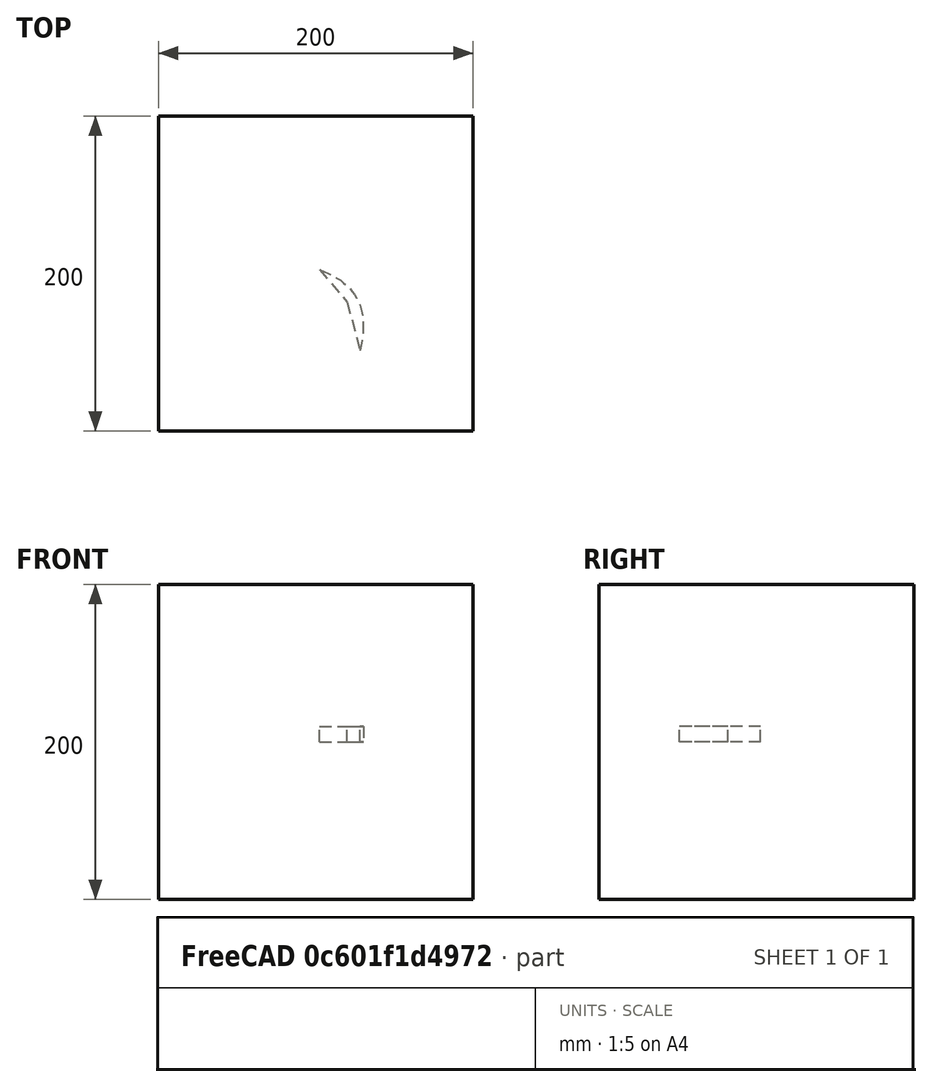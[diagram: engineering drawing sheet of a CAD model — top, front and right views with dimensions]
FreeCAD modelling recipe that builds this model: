
FCSTD DOCUMENT  (FreeCAD 1.0R39109 (Git))
Label: extrudedParabola-2
License: All rights reserved
LicenseURL: http://en.wikipedia.org/wiki/All_rights_reserved
objects: App::DocumentObjectGroupPython×1248, App::Part×2, Part::FeaturePython×1, Sketcher::SketchObject×1, Part::Extrusion×1
note: 4 computed .brp shape members not serialized (recipe doc carries the construction recipe); baked Part::Feature solids carry a one-line shape summary decoded from their .brp

FEATURE [App::DocumentObjectGroupPython] HALFPI  # scripted group (container) (typed FeaturePython)
  name = HALFPI
  value = pi/2.
FEATURE [App::DocumentObjectGroupPython] PI  # scripted group (container) (typed FeaturePython)
  name = PI
  value = 1.*pi
FEATURE [App::DocumentObjectGroupPython] TWOPI  # scripted group (container) (typed FeaturePython)
  name = TWOPI
  value = 2.*pi
FEATURE [App::DocumentObjectGroupPython] Constants  # scripted group (container) (typed FeaturePython)
  Group = -> [HALFPI,PI,TWOPI]
FEATURE [App::DocumentObjectGroupPython] Variables  # scripted group (container) (typed FeaturePython)
FEATURE [App::DocumentObjectGroupPython] Quantities  # scripted group (container) (typed FeaturePython)
FEATURE [App::DocumentObjectGroupPython] Isotopes  # scripted group (container) (typed FeaturePython)
FEATURE [App::DocumentObjectGroupPython] Elements  # scripted group (container) (typed FeaturePython)
FEATURE [App::DocumentObjectGroupPython] G4Isotopes  # scripted group (container) (typed FeaturePython)
FEATURE [App::DocumentObjectGroupPython] H_element  # scripted group (container) (typed FeaturePython)
  Z = 1
  atom_value = 1.008
  formula = H
  name = H_element
FEATURE [App::DocumentObjectGroupPython] He_element  # scripted group (container) (typed FeaturePython)
  Z = 2
  atom_value = 4.0026
  formula = He
  name = He_element
FEATURE [App::DocumentObjectGroupPython] Li_element  # scripted group (container) (typed FeaturePython)
  Z = 3
  atom_value = 6.94
  formula = Li
  name = Li_element
FEATURE [App::DocumentObjectGroupPython] Be_element  # scripted group (container) (typed FeaturePython)
  Z = 4
  atom_value = 9.01218
  formula = Be
  name = Be_element
FEATURE [App::DocumentObjectGroupPython] B_element  # scripted group (container) (typed FeaturePython)
  Z = 5
  atom_value = 10.81
  formula = B
  name = B_element
FEATURE [App::DocumentObjectGroupPython] C_element  # scripted group (container) (typed FeaturePython)
  Z = 6
  atom_value = 12.011
  formula = C
  name = C_element
FEATURE [App::DocumentObjectGroupPython] N_element  # scripted group (container) (typed FeaturePython)
  Z = 7
  atom_value = 14.007
  formula = N
  name = N_element
FEATURE [App::DocumentObjectGroupPython] O_element  # scripted group (container) (typed FeaturePython)
  Z = 8
  atom_value = 15.999
  formula = O
  name = O_element
FEATURE [App::DocumentObjectGroupPython] F_element  # scripted group (container) (typed FeaturePython)
  Z = 9
  atom_value = 18.9984
  formula = F
  name = F_element
FEATURE [App::DocumentObjectGroupPython] Ne_element  # scripted group (container) (typed FeaturePython)
  Z = 10
  atom_value = 20.1797
  formula = Ne
  name = Ne_element
FEATURE [App::DocumentObjectGroupPython] Na_element  # scripted group (container) (typed FeaturePython)
  Z = 11
  atom_value = 22.9898
  formula = Na
  name = Na_element
FEATURE [App::DocumentObjectGroupPython] Mg_element  # scripted group (container) (typed FeaturePython)
  Z = 12
  atom_value = 24.305
  formula = Mg
  name = Mg_element
FEATURE [App::DocumentObjectGroupPython] Al_element  # scripted group (container) (typed FeaturePython)
  Z = 13
  atom_value = 26.9815
  formula = Al
  name = Al_element
FEATURE [App::DocumentObjectGroupPython] Si_element  # scripted group (container) (typed FeaturePython)
  Z = 14
  atom_value = 28.085
  formula = Si
  name = Si_element
FEATURE [App::DocumentObjectGroupPython] P_element  # scripted group (container) (typed FeaturePython)
  Z = 15
  atom_value = 30.9738
  formula = P
  name = P_element
FEATURE [App::DocumentObjectGroupPython] S_element  # scripted group (container) (typed FeaturePython)
  Z = 16
  atom_value = 32.06
  formula = S
  name = S_element
FEATURE [App::DocumentObjectGroupPython] Cl_element  # scripted group (container) (typed FeaturePython)
  Z = 17
  atom_value = 35.45
  formula = Cl
  name = Cl_element
FEATURE [App::DocumentObjectGroupPython] Ar_element  # scripted group (container) (typed FeaturePython)
  Z = 18
  atom_value = 39.95
  formula = Ar
  name = Ar_element
FEATURE [App::DocumentObjectGroupPython] K_element  # scripted group (container) (typed FeaturePython)
  Z = 19
  atom_value = 39.0983
  formula = K
  name = K_element
FEATURE [App::DocumentObjectGroupPython] Ca_element  # scripted group (container) (typed FeaturePython)
  Z = 20
  atom_value = 40.078
  formula = Ca
  name = Ca_element
FEATURE [App::DocumentObjectGroupPython] Sc_element  # scripted group (container) (typed FeaturePython)
  Z = 21
  atom_value = 44.9559
  formula = Sc
  name = Sc_element
FEATURE [App::DocumentObjectGroupPython] Ti_element  # scripted group (container) (typed FeaturePython)
  Z = 22
  atom_value = 47.867
  formula = Ti
  name = Ti_element
FEATURE [App::DocumentObjectGroupPython] V_element  # scripted group (container) (typed FeaturePython)
  Z = 23
  atom_value = 50.9415
  formula = V
  name = V_element
FEATURE [App::DocumentObjectGroupPython] Cr_element  # scripted group (container) (typed FeaturePython)
  Z = 24
  atom_value = 51.9961
  formula = Cr
  name = Cr_element
FEATURE [App::DocumentObjectGroupPython] Mn_element  # scripted group (container) (typed FeaturePython)
  Z = 25
  atom_value = 54.938
  formula = Mn
  name = Mn_element
FEATURE [App::DocumentObjectGroupPython] Fe_element  # scripted group (container) (typed FeaturePython)
  Z = 26
  atom_value = 55.845
  formula = Fe
  name = Fe_element
FEATURE [App::DocumentObjectGroupPython] Co_element  # scripted group (container) (typed FeaturePython)
  Z = 27
  atom_value = 58.9332
  formula = Co
  name = Co_element
FEATURE [App::DocumentObjectGroupPython] Ni_element  # scripted group (container) (typed FeaturePython)
  Z = 28
  atom_value = 58.6934
  formula = Ni
  name = Ni_element
FEATURE [App::DocumentObjectGroupPython] Cu_element  # scripted group (container) (typed FeaturePython)
  Z = 29
  atom_value = 63.546
  formula = Cu
  name = Cu_element
FEATURE [App::DocumentObjectGroupPython] Zn_element  # scripted group (container) (typed FeaturePython)
  Z = 30
  atom_value = 65.38
  formula = Zn
  name = Zn_element
FEATURE [App::DocumentObjectGroupPython] Ga_element  # scripted group (container) (typed FeaturePython)
  Z = 31
  atom_value = 69.723
  formula = Ga
  name = Ga_element
FEATURE [App::DocumentObjectGroupPython] Ge_element  # scripted group (container) (typed FeaturePython)
  Z = 32
  atom_value = 72.63
  formula = Ge
  name = Ge_element
FEATURE [App::DocumentObjectGroupPython] As_element  # scripted group (container) (typed FeaturePython)
  Z = 33
  atom_value = 74.9216
  formula = As
  name = As_element
FEATURE [App::DocumentObjectGroupPython] Se_element  # scripted group (container) (typed FeaturePython)
  Z = 34
  atom_value = 78.971
  formula = Se
  name = Se_element
FEATURE [App::DocumentObjectGroupPython] Br_element  # scripted group (container) (typed FeaturePython)
  Z = 35
  atom_value = 79.904
  formula = Br
  name = Br_element
FEATURE [App::DocumentObjectGroupPython] Kr_element  # scripted group (container) (typed FeaturePython)
  Z = 36
  atom_value = 83.798
  formula = Kr
  name = Kr_element
FEATURE [App::DocumentObjectGroupPython] Rb_element  # scripted group (container) (typed FeaturePython)
  Z = 37
  atom_value = 85.4678
  formula = Rb
  name = Rb_element
FEATURE [App::DocumentObjectGroupPython] Sr_element  # scripted group (container) (typed FeaturePython)
  Z = 38
  atom_value = 87.62
  formula = Sr
  name = Sr_element
FEATURE [App::DocumentObjectGroupPython] Y_element  # scripted group (container) (typed FeaturePython)
  Z = 39
  atom_value = 88.9058
  formula = Y
  name = Y_element
FEATURE [App::DocumentObjectGroupPython] Zr_element  # scripted group (container) (typed FeaturePython)
  Z = 40
  atom_value = 91.224
  formula = Zr
  name = Zr_element
FEATURE [App::DocumentObjectGroupPython] Nb_element  # scripted group (container) (typed FeaturePython)
  Z = 41
  atom_value = 92.9064
  formula = Nb
  name = Nb_element
FEATURE [App::DocumentObjectGroupPython] Mo_element  # scripted group (container) (typed FeaturePython)
  Z = 42
  atom_value = 95.95
  formula = Mo
  name = Mo_element
FEATURE [App::DocumentObjectGroupPython] Tc_element  # scripted group (container) (typed FeaturePython)
  Z = 43
  atom_value = 97
  formula = Tc
  name = Tc_element
FEATURE [App::DocumentObjectGroupPython] Ru_element  # scripted group (container) (typed FeaturePython)
  Z = 44
  atom_value = 101.07
  formula = Ru
  name = Ru_element
FEATURE [App::DocumentObjectGroupPython] Rh_element  # scripted group (container) (typed FeaturePython)
  Z = 45
  atom_value = 102.905
  formula = Rh
  name = Rh_element
FEATURE [App::DocumentObjectGroupPython] Pd_element  # scripted group (container) (typed FeaturePython)
  Z = 46
  atom_value = 106.42
  formula = Pd
  name = Pd_element
FEATURE [App::DocumentObjectGroupPython] Ag_element  # scripted group (container) (typed FeaturePython)
  Z = 47
  atom_value = 107.868
  formula = Ag
  name = Ag_element
FEATURE [App::DocumentObjectGroupPython] Cd_element  # scripted group (container) (typed FeaturePython)
  Z = 48
  atom_value = 112.414
  formula = Cd
  name = Cd_element
FEATURE [App::DocumentObjectGroupPython] In_element  # scripted group (container) (typed FeaturePython)
  Z = 49
  atom_value = 114.818
  formula = In
  name = In_element
FEATURE [App::DocumentObjectGroupPython] Sn_element  # scripted group (container) (typed FeaturePython)
  Z = 50
  atom_value = 118.71
  formula = Sn
  name = Sn_element
FEATURE [App::DocumentObjectGroupPython] Sb_element  # scripted group (container) (typed FeaturePython)
  Z = 51
  atom_value = 121.76
  formula = Sb
  name = Sb_element
FEATURE [App::DocumentObjectGroupPython] Te_element  # scripted group (container) (typed FeaturePython)
  Z = 52
  atom_value = 127.6
  formula = Te
  name = Te_element
FEATURE [App::DocumentObjectGroupPython] I_element  # scripted group (container) (typed FeaturePython)
  Z = 53
  atom_value = 126.904
  formula = I
  name = I_element
FEATURE [App::DocumentObjectGroupPython] Xe_element  # scripted group (container) (typed FeaturePython)
  Z = 54
  atom_value = 131.293
  formula = Xe
  name = Xe_element
FEATURE [App::DocumentObjectGroupPython] Cs_element  # scripted group (container) (typed FeaturePython)
  Z = 55
  atom_value = 132.905
  formula = Cs
  name = Cs_element
FEATURE [App::DocumentObjectGroupPython] Ba_element  # scripted group (container) (typed FeaturePython)
  Z = 56
  atom_value = 137.327
  formula = Ba
  name = Ba_element
FEATURE [App::DocumentObjectGroupPython] La_element  # scripted group (container) (typed FeaturePython)
  Z = 57
  atom_value = 138.905
  formula = La
  name = La_element
FEATURE [App::DocumentObjectGroupPython] Ce_element  # scripted group (container) (typed FeaturePython)
  Z = 58
  atom_value = 140.116
  formula = Ce
  name = Ce_element
FEATURE [App::DocumentObjectGroupPython] Pr_element  # scripted group (container) (typed FeaturePython)
  Z = 59
  atom_value = 140.908
  formula = Pr
  name = Pr_element
FEATURE [App::DocumentObjectGroupPython] Nd_element  # scripted group (container) (typed FeaturePython)
  Z = 60
  atom_value = 144.242
  formula = Nd
  name = Nd_element
FEATURE [App::DocumentObjectGroupPython] Pm_element  # scripted group (container) (typed FeaturePython)
  Z = 61
  atom_value = 145
  formula = Pm
  name = Pm_element
FEATURE [App::DocumentObjectGroupPython] Sm_element  # scripted group (container) (typed FeaturePython)
  Z = 62
  atom_value = 150.36
  formula = Sm
  name = Sm_element
FEATURE [App::DocumentObjectGroupPython] Eu_element  # scripted group (container) (typed FeaturePython)
  Z = 63
  atom_value = 151.964
  formula = Eu
  name = Eu_element
FEATURE [App::DocumentObjectGroupPython] Gd_element  # scripted group (container) (typed FeaturePython)
  Z = 64
  atom_value = 157.25
  formula = Gd
  name = Gd_element
FEATURE [App::DocumentObjectGroupPython] Tb_element  # scripted group (container) (typed FeaturePython)
  Z = 65
  atom_value = 158.925
  formula = Tb
  name = Tb_element
FEATURE [App::DocumentObjectGroupPython] Dy_element  # scripted group (container) (typed FeaturePython)
  Z = 66
  atom_value = 162.5
  formula = Dy
  name = Dy_element
FEATURE [App::DocumentObjectGroupPython] Ho_element  # scripted group (container) (typed FeaturePython)
  Z = 67
  atom_value = 164.93
  formula = Ho
  name = Ho_element
FEATURE [App::DocumentObjectGroupPython] Er_element  # scripted group (container) (typed FeaturePython)
  Z = 68
  atom_value = 167.259
  formula = Er
  name = Er_element
FEATURE [App::DocumentObjectGroupPython] Tm_element  # scripted group (container) (typed FeaturePython)
  Z = 69
  atom_value = 168.934
  formula = Tm
  name = Tm_element
FEATURE [App::DocumentObjectGroupPython] Yb_element  # scripted group (container) (typed FeaturePython)
  Z = 70
  atom_value = 173.045
  formula = Yb
  name = Yb_element
FEATURE [App::DocumentObjectGroupPython] Lu_element  # scripted group (container) (typed FeaturePython)
  Z = 71
  atom_value = 174.967
  formula = Lu
  name = Lu_element
FEATURE [App::DocumentObjectGroupPython] Hf_element  # scripted group (container) (typed FeaturePython)
  Z = 72
  atom_value = 178.49
  formula = Hf
  name = Hf_element
FEATURE [App::DocumentObjectGroupPython] Ta_element  # scripted group (container) (typed FeaturePython)
  Z = 73
  atom_value = 180.948
  formula = Ta
  name = Ta_element
FEATURE [App::DocumentObjectGroupPython] W_element  # scripted group (container) (typed FeaturePython)
  Z = 74
  atom_value = 183.84
  formula = W
  name = W_element
FEATURE [App::DocumentObjectGroupPython] Re_element  # scripted group (container) (typed FeaturePython)
  Z = 75
  atom_value = 186.207
  formula = Re
  name = Re_element
FEATURE [App::DocumentObjectGroupPython] Os_element  # scripted group (container) (typed FeaturePython)
  Z = 76
  atom_value = 190.23
  formula = Os
  name = Os_element
FEATURE [App::DocumentObjectGroupPython] Ir_element  # scripted group (container) (typed FeaturePython)
  Z = 77
  atom_value = 192.217
  formula = Ir
  name = Ir_element
FEATURE [App::DocumentObjectGroupPython] Pt_element  # scripted group (container) (typed FeaturePython)
  Z = 78
  atom_value = 195.084
  formula = Pt
  name = Pt_element
FEATURE [App::DocumentObjectGroupPython] Au_element  # scripted group (container) (typed FeaturePython)
  Z = 79
  atom_value = 196.967
  formula = Au
  name = Au_element
FEATURE [App::DocumentObjectGroupPython] Hg_element  # scripted group (container) (typed FeaturePython)
  Z = 80
  atom_value = 200.592
  formula = Hg
  name = Hg_element
FEATURE [App::DocumentObjectGroupPython] Tl_element  # scripted group (container) (typed FeaturePython)
  Z = 81
  atom_value = 204.38
  formula = Tl
  name = Tl_element
FEATURE [App::DocumentObjectGroupPython] Pb_element  # scripted group (container) (typed FeaturePython)
  Z = 82
  atom_value = 207.2
  formula = Pb
  name = Pb_element
FEATURE [App::DocumentObjectGroupPython] Bi_element  # scripted group (container) (typed FeaturePython)
  Z = 83
  atom_value = 208.98
  formula = Bi
  name = Bi_element
FEATURE [App::DocumentObjectGroupPython] Po_element  # scripted group (container) (typed FeaturePython)
  Z = 84
  atom_value = 209
  formula = Po
  name = Po_element
FEATURE [App::DocumentObjectGroupPython] At_element  # scripted group (container) (typed FeaturePython)
  Z = 85
  atom_value = 210
  formula = At
  name = At_element
FEATURE [App::DocumentObjectGroupPython] Rn_element  # scripted group (container) (typed FeaturePython)
  Z = 86
  atom_value = 222
  formula = Rn
  name = Rn_element
FEATURE [App::DocumentObjectGroupPython] Fr_element  # scripted group (container) (typed FeaturePython)
  Z = 87
  atom_value = 223
  formula = Fr
  name = Fr_element
FEATURE [App::DocumentObjectGroupPython] Ra_element  # scripted group (container) (typed FeaturePython)
  Z = 88
  atom_value = 226
  formula = Ra
  name = Ra_element
FEATURE [App::DocumentObjectGroupPython] Ac_element  # scripted group (container) (typed FeaturePython)
  Z = 89
  atom_value = 227
  formula = Ac
  name = Ac_element
FEATURE [App::DocumentObjectGroupPython] Th_element  # scripted group (container) (typed FeaturePython)
  Z = 90
  atom_value = 232.038
  formula = Th
  name = Th_element
FEATURE [App::DocumentObjectGroupPython] Pa_element  # scripted group (container) (typed FeaturePython)
  Z = 91
  atom_value = 231.036
  formula = Pa
  name = Pa_element
FEATURE [App::DocumentObjectGroupPython] U_element  # scripted group (container) (typed FeaturePython)
  Z = 92
  atom_value = 238.029
  formula = U
  name = U_element
FEATURE [App::DocumentObjectGroupPython] Np_element  # scripted group (container) (typed FeaturePython)
  Z = 93
  atom_value = 237
  formula = Np
  name = Np_element
FEATURE [App::DocumentObjectGroupPython] Pu_element  # scripted group (container) (typed FeaturePython)
  Z = 94
  atom_value = 244
  formula = Pu
  name = Pu_element
FEATURE [App::DocumentObjectGroupPython] Am_element  # scripted group (container) (typed FeaturePython)
  Z = 95
  atom_value = 243
  formula = Am
  name = Am_element
FEATURE [App::DocumentObjectGroupPython] Cm_element  # scripted group (container) (typed FeaturePython)
  Z = 96
  atom_value = 247
  formula = Cm
  name = Cm_element
FEATURE [App::DocumentObjectGroupPython] Bk_element  # scripted group (container) (typed FeaturePython)
  Z = 97
  atom_value = 247
  formula = Bk
  name = Bk_element
FEATURE [App::DocumentObjectGroupPython] Cf_element  # scripted group (container) (typed FeaturePython)
  Z = 98
  atom_value = 251
  formula = Cf
  name = Cf_element
FEATURE [App::DocumentObjectGroupPython] G4Elements  # scripted group (container) (typed FeaturePython)
  Group = -> [H_element,He_element,Li_element,Be_element,B_element,C_element,N_element,O_element,F_element,Ne_element,Na_element,Mg_element,Al_element,Si_element,P_element,S_element,Cl_element,Ar_element,K_element,Ca_element,Sc_element,Ti_element,V_element,Cr_element,Mn_element,Fe_element,Co_element,Ni_element,Cu_element,Zn_element,Ga_element,Ge_element,As_element,Se_element,Br_element,Kr_element,Rb_element,+61 more]
FEATURE [App::DocumentObjectGroupPython] H_element001  label="H_element : 0.101"  # scripted group (container) (typed FeaturePython)
  n = 0.101327
FEATURE [App::DocumentObjectGroupPython] C_element001  label="C_element : 0.775"  # scripted group (container) (typed FeaturePython)
  n = 0.7755
FEATURE [App::DocumentObjectGroupPython] N_element001  label="N_element : 0.035"  # scripted group (container) (typed FeaturePython)
  n = 0.035057
FEATURE [App::DocumentObjectGroupPython] O_element001  label="O_element : 0.052"  # scripted group (container) (typed FeaturePython)
  n = 0.0523159
FEATURE [App::DocumentObjectGroupPython] F_element001  label="F_element : 0.017"  # scripted group (container) (typed FeaturePython)
  n = 0.017422
FEATURE [App::DocumentObjectGroupPython] Ca_element001  label="Ca_element : 0.018"  # scripted group (container) (typed FeaturePython)
  n = 0.018378
FEATURE [App::DocumentObjectGroupPython] G4_A_150_TISSUE  label="G4_A-150_TISSUE"  # scripted group (container) (typed FeaturePython)
  Dunit = g/cm3
  Dvalue = 1.127
  Group = -> [H_element001,C_element001,N_element001,O_element001,F_element001,Ca_element001]
  conduct = 2
  density = 1
  expand = 3
  formula = G4_A-150_TISSUE
  name = G4_A-150_TISSUE
  specific = 4
FEATURE [App::DocumentObjectGroupPython] C_element002  label="C_element : 3"  # scripted group (container) (typed FeaturePython)
  n = 3
  ref = C_element
FEATURE [App::DocumentObjectGroupPython] H_element002  label="H_element : 6"  # scripted group (container) (typed FeaturePython)
  n = 6
  ref = H_element
FEATURE [App::DocumentObjectGroupPython] O_element002  label="O_element : 1"  # scripted group (container) (typed FeaturePython)
  n = 1
  ref = O_element
FEATURE [App::DocumentObjectGroupPython] G4_ACETONE  # scripted group (container) (typed FeaturePython)
  Dunit = g/cm3
  Dvalue = 0.7899
  Group = -> [C_element002,H_element002,O_element002]
  conduct = 2
  density = 1
  expand = 3
  formula = G4_ACETONE
  name = G4_ACETONE
  specific = 4
FEATURE [App::DocumentObjectGroupPython] C_element003  label="C_element : 2"  # scripted group (container) (typed FeaturePython)
  n = 2
  ref = C_element
FEATURE [App::DocumentObjectGroupPython] H_element003  label="H_element : 2"  # scripted group (container) (typed FeaturePython)
  n = 2
  ref = H_element
FEATURE [App::DocumentObjectGroupPython] G4_ACETYLENE  # scripted group (container) (typed FeaturePython)
  Dunit = g/cm3
  Dvalue = 0.0010967
  Group = -> [C_element003,H_element003]
  conduct = 2
  density = 1
  expand = 3
  formula = G4_ACETYLENE
  name = G4_ACETYLENE
  specific = 4
FEATURE [App::DocumentObjectGroupPython] C_element004  label="C_element : 5"  # scripted group (container) (typed FeaturePython)
  n = 5
  ref = C_element
FEATURE [App::DocumentObjectGroupPython] H_element004  label="H_element : 5"  # scripted group (container) (typed FeaturePython)
  n = 5
  ref = H_element
FEATURE [App::DocumentObjectGroupPython] N_element002  label="N_element : 5"  # scripted group (container) (typed FeaturePython)
  n = 5
  ref = N_element
FEATURE [App::DocumentObjectGroupPython] G4_ADENINE  # scripted group (container) (typed FeaturePython)
  Dunit = g/cm3
  Dvalue = 1.6
  Group = -> [C_element004,H_element004,N_element002]
  conduct = 2
  density = 1
  expand = 3
  formula = G4_ADENINE
  name = G4_ADENINE
  specific = 4
FEATURE [App::DocumentObjectGroupPython] H_element005  label="H_element : 0.114"  # scripted group (container) (typed FeaturePython)
  n = 0.114
FEATURE [App::DocumentObjectGroupPython] C_element005  label="C_element : 0.598"  # scripted group (container) (typed FeaturePython)
  n = 0.598
FEATURE [App::DocumentObjectGroupPython] N_element003  label="N_element : 0.007"  # scripted group (container) (typed FeaturePython)
  n = 0.007
FEATURE [App::DocumentObjectGroupPython] O_element003  label="O_element : 0.278"  # scripted group (container) (typed FeaturePython)
  n = 0.278
FEATURE [App::DocumentObjectGroupPython] Na_element001  label="Na_element : 0.001"  # scripted group (container) (typed FeaturePython)
  n = 0.001
FEATURE [App::DocumentObjectGroupPython] S_element001  label="S_element : 0.001"  # scripted group (container) (typed FeaturePython)
  n = 0.001
FEATURE [App::DocumentObjectGroupPython] Cl_element001  label="Cl_element : 0.001"  # scripted group (container) (typed FeaturePython)
  n = 0.001
FEATURE [App::DocumentObjectGroupPython] G4_ADIPOSE_TISSUE_ICRP  # scripted group (container) (typed FeaturePython)
  Dunit = g/cm3
  Dvalue = 0.95
  Group = -> [H_element005,C_element005,N_element003,O_element003,Na_element001,S_element001,Cl_element001]
  conduct = 2
  density = 1
  expand = 3
  formula = G4_ADIPOSE_TISSUE_ICRP
  name = G4_ADIPOSE_TISSUE_ICRP
  specific = 4
FEATURE [App::DocumentObjectGroupPython] C_element006  label="C_element : 0.000"  # scripted group (container) (typed FeaturePython)
  n = 0.000124
FEATURE [App::DocumentObjectGroupPython] N_element004  label="N_element : 0.755"  # scripted group (container) (typed FeaturePython)
  n = 0.755268
FEATURE [App::DocumentObjectGroupPython] O_element004  label="O_element : 0.232"  # scripted group (container) (typed FeaturePython)
  n = 0.231781
FEATURE [App::DocumentObjectGroupPython] Ar_element001  label="Ar_element : 0.013"  # scripted group (container) (typed FeaturePython)
  n = 0.012827
FEATURE [App::DocumentObjectGroupPython] G4_AIR  # scripted group (container) (typed FeaturePython)
  Dunit = g/cm3
  Dvalue = 0.00120479
  Group = -> [C_element006,N_element004,O_element004,Ar_element001]
  conduct = 2
  density = 1
  expand = 3
  formula = G4_AIR
  name = G4_AIR
  specific = 4
FEATURE [App::DocumentObjectGroupPython] C_element007  label="C_element : 006"  # scripted group (container) (typed FeaturePython)
  n = 3
  ref = C_element
FEATURE [App::DocumentObjectGroupPython] H_element006  label="H_element : 7"  # scripted group (container) (typed FeaturePython)
  n = 7
  ref = H_element
FEATURE [App::DocumentObjectGroupPython] N_element005  label="N_element : 1"  # scripted group (container) (typed FeaturePython)
  n = 1
  ref = N_element
FEATURE [App::DocumentObjectGroupPython] O_element005  label="O_element : 2"  # scripted group (container) (typed FeaturePython)
  n = 2
  ref = O_element
FEATURE [App::DocumentObjectGroupPython] G4_ALANINE  # scripted group (container) (typed FeaturePython)
  Dunit = g/cm3
  Dvalue = 1.42
  Group = -> [C_element007,H_element006,N_element005,O_element005]
  conduct = 2
  density = 1
  expand = 3
  formula = G4_ALANINE
  name = G4_ALANINE
  specific = 4
FEATURE [App::DocumentObjectGroupPython] Al_element001  label="Al_element : 2"  # scripted group (container) (typed FeaturePython)
  n = 2
  ref = Al_element
FEATURE [App::DocumentObjectGroupPython] O_element006  label="O_element : 3"  # scripted group (container) (typed FeaturePython)
  n = 3
  ref = O_element
FEATURE [App::DocumentObjectGroupPython] G4_ALUMINUM_OXIDE  # scripted group (container) (typed FeaturePython)
  Dunit = g/cm3
  Dvalue = 3.97
  Group = -> [Al_element001,O_element006]
  conduct = 2
  density = 1
  expand = 3
  formula = G4_ALUMINUM_OXIDE
  name = G4_ALUMINUM_OXIDE
  specific = 4
FEATURE [App::DocumentObjectGroupPython] H_element007  label="H_element : 0.106"  # scripted group (container) (typed FeaturePython)
  n = 0.10593
FEATURE [App::DocumentObjectGroupPython] C_element008  label="C_element : 0.789"  # scripted group (container) (typed FeaturePython)
  n = 0.788974
FEATURE [App::DocumentObjectGroupPython] O_element007  label="O_element : 0.105"  # scripted group (container) (typed FeaturePython)
  n = 0.105096
FEATURE [App::DocumentObjectGroupPython] G4_AMBER  # scripted group (container) (typed FeaturePython)
  Dunit = g/cm3
  Dvalue = 1.1
  Group = -> [H_element007,C_element008,O_element007]
  conduct = 2
  density = 1
  expand = 3
  formula = G4_AMBER
  name = G4_AMBER
  specific = 4
FEATURE [App::DocumentObjectGroupPython] N_element006  label="N_element : 006"  # scripted group (container) (typed FeaturePython)
  n = 1
  ref = N_element
FEATURE [App::DocumentObjectGroupPython] H_element008  label="H_element : 3"  # scripted group (container) (typed FeaturePython)
  n = 3
  ref = H_element
FEATURE [App::DocumentObjectGroupPython] G4_AMMONIA  # scripted group (container) (typed FeaturePython)
  Dunit = g/cm3
  Dvalue = 0.000826019
  Group = -> [N_element006,H_element008]
  conduct = 2
  density = 1
  expand = 3
  formula = G4_AMMONIA
  name = G4_AMMONIA
  specific = 4
FEATURE [App::DocumentObjectGroupPython] C_element009  label="C_element : 6"  # scripted group (container) (typed FeaturePython)
  n = 6
  ref = C_element
FEATURE [App::DocumentObjectGroupPython] H_element009  label="H_element : 008"  # scripted group (container) (typed FeaturePython)
  n = 7
  ref = H_element
FEATURE [App::DocumentObjectGroupPython] N_element007  label="N_element : 007"  # scripted group (container) (typed FeaturePython)
  n = 1
  ref = N_element
FEATURE [App::DocumentObjectGroupPython] G4_ANILINE  # scripted group (container) (typed FeaturePython)
  Dunit = g/cm3
  Dvalue = 1.0235
  Group = -> [C_element009,H_element009,N_element007]
  conduct = 2
  density = 1
  expand = 3
  formula = G4_ANILINE
  name = G4_ANILINE
  specific = 4
FEATURE [App::DocumentObjectGroupPython] C_element010  label="C_element : 14"  # scripted group (container) (typed FeaturePython)
  n = 14
  ref = C_element
FEATURE [App::DocumentObjectGroupPython] H_element010  label="H_element : 10"  # scripted group (container) (typed FeaturePython)
  n = 10
  ref = H_element
FEATURE [App::DocumentObjectGroupPython] G4_ANTHRACENE  # scripted group (container) (typed FeaturePython)
  Dunit = g/cm3
  Dvalue = 1.283
  Group = -> [C_element010,H_element010]
  conduct = 2
  density = 1
  expand = 3
  formula = G4_ANTHRACENE
  name = G4_ANTHRACENE
  specific = 4
FEATURE [App::DocumentObjectGroupPython] H_element011  label="H_element : 0.065"  # scripted group (container) (typed FeaturePython)
  n = 0.0654709
FEATURE [App::DocumentObjectGroupPython] C_element011  label="C_element : 0.537"  # scripted group (container) (typed FeaturePython)
  n = 0.536944
FEATURE [App::DocumentObjectGroupPython] N_element008  label="N_element : 0.021"  # scripted group (container) (typed FeaturePython)
  n = 0.0215
FEATURE [App::DocumentObjectGroupPython] O_element008  label="O_element : 0.032"  # scripted group (container) (typed FeaturePython)
  n = 0.032085
FEATURE [App::DocumentObjectGroupPython] F_element002  label="F_element : 0.167"  # scripted group (container) (typed FeaturePython)
  n = 0.167411
FEATURE [App::DocumentObjectGroupPython] Ca_element002  label="Ca_element : 0.177"  # scripted group (container) (typed FeaturePython)
  n = 0.176589
FEATURE [App::DocumentObjectGroupPython] G4_B_100_BONE  label="G4_B-100_BONE"  # scripted group (container) (typed FeaturePython)
  Dunit = g/cm3
  Dvalue = 1.45
  Group = -> [H_element011,C_element011,N_element008,O_element008,F_element002,Ca_element002]
  conduct = 2
  density = 1
  expand = 3
  formula = G4_B-100_BONE
  name = G4_B-100_BONE
  specific = 4
FEATURE [App::DocumentObjectGroupPython] H_element012  label="H_element : 0.057"  # scripted group (container) (typed FeaturePython)
  n = 0.057441
FEATURE [App::DocumentObjectGroupPython] C_element012  label="C_element : 0.790"  # scripted group (container) (typed FeaturePython)
  n = 0.774591
FEATURE [App::DocumentObjectGroupPython] O_element009  label="O_element : 0.168"  # scripted group (container) (typed FeaturePython)
  n = 0.167968
FEATURE [App::DocumentObjectGroupPython] G4_BAKELITE  # scripted group (container) (typed FeaturePython)
  Dunit = g/cm3
  Dvalue = 1.25
  Group = -> [H_element012,C_element012,O_element009]
  conduct = 2
  density = 1
  expand = 3
  formula = G4_BAKELITE
  name = G4_BAKELITE
  specific = 4
FEATURE [App::DocumentObjectGroupPython] Ba_element001  label="Ba_element : 1"  # scripted group (container) (typed FeaturePython)
  n = 1
  ref = Ba_element
FEATURE [App::DocumentObjectGroupPython] F_element003  label="F_element : 2"  # scripted group (container) (typed FeaturePython)
  n = 2
  ref = F_element
FEATURE [App::DocumentObjectGroupPython] G4_BARIUM_FLUORIDE  # scripted group (container) (typed FeaturePython)
  Dunit = g/cm3
  Dvalue = 4.89
  Group = -> [Ba_element001,F_element003]
  conduct = 2
  density = 1
  expand = 3
  formula = G4_BARIUM_FLUORIDE
  name = G4_BARIUM_FLUORIDE
  specific = 4
FEATURE [App::DocumentObjectGroupPython] Ba_element002  label="Ba_element : 002"  # scripted group (container) (typed FeaturePython)
  n = 1
  ref = Ba_element
FEATURE [App::DocumentObjectGroupPython] S_element002  label="S_element : 1"  # scripted group (container) (typed FeaturePython)
  n = 1
  ref = S_element
FEATURE [App::DocumentObjectGroupPython] O_element010  label="O_element : 4"  # scripted group (container) (typed FeaturePython)
  n = 4
  ref = O_element
FEATURE [App::DocumentObjectGroupPython] G4_BARIUM_SULFATE  # scripted group (container) (typed FeaturePython)
  Dunit = g/cm3
  Dvalue = 4.5
  Group = -> [Ba_element002,S_element002,O_element010]
  conduct = 2
  density = 1
  expand = 3
  formula = G4_BARIUM_SULFATE
  name = G4_BARIUM_SULFATE
  specific = 4
FEATURE [App::DocumentObjectGroupPython] C_element013  label="C_element : 007"  # scripted group (container) (typed FeaturePython)
  n = 6
  ref = C_element
FEATURE [App::DocumentObjectGroupPython] H_element013  label="H_element : 009"  # scripted group (container) (typed FeaturePython)
  n = 6
  ref = H_element
FEATURE [App::DocumentObjectGroupPython] G4_BENZENE  # scripted group (container) (typed FeaturePython)
  Dunit = g/cm3
  Dvalue = 0.87865
  Group = -> [C_element013,H_element013]
  conduct = 2
  density = 1
  expand = 3
  formula = G4_BENZENE
  name = G4_BENZENE
  specific = 4
FEATURE [App::DocumentObjectGroupPython] Be_element001  label="Be_element : 1"  # scripted group (container) (typed FeaturePython)
  n = 1
  ref = Be_element
FEATURE [App::DocumentObjectGroupPython] O_element011  label="O_element : 005"  # scripted group (container) (typed FeaturePython)
  n = 1
  ref = O_element
FEATURE [App::DocumentObjectGroupPython] G4_BERYLLIUM_OXIDE  # scripted group (container) (typed FeaturePython)
  Dunit = g/cm3
  Dvalue = 3.01
  Group = -> [Be_element001,O_element011]
  conduct = 2
  density = 1
  expand = 3
  formula = G4_BERYLLIUM_OXIDE
  name = G4_BERYLLIUM_OXIDE
  specific = 4
FEATURE [App::DocumentObjectGroupPython] Bi_element001  label="Bi_element : 4"  # scripted group (container) (typed FeaturePython)
  n = 4
  ref = Bi_element
FEATURE [App::DocumentObjectGroupPython] Ge_element001  label="Ge_element : 3"  # scripted group (container) (typed FeaturePython)
  n = 3
  ref = Ge_element
FEATURE [App::DocumentObjectGroupPython] O_element012  label="O_element : 12"  # scripted group (container) (typed FeaturePython)
  n = 12
  ref = O_element
FEATURE [App::DocumentObjectGroupPython] G4_BGO  # scripted group (container) (typed FeaturePython)
  Dunit = g/cm3
  Dvalue = 7.13
  Group = -> [Bi_element001,Ge_element001,O_element012]
  conduct = 2
  density = 1
  expand = 3
  formula = G4_BGO
  name = G4_BGO
  specific = 4
FEATURE [App::DocumentObjectGroupPython] H_element014  label="H_element : 0.102"  # scripted group (container) (typed FeaturePython)
  n = 0.102
FEATURE [App::DocumentObjectGroupPython] C_element014  label="C_element : 0.110"  # scripted group (container) (typed FeaturePython)
  n = 0.11
FEATURE [App::DocumentObjectGroupPython] N_element009  label="N_element : 0.033"  # scripted group (container) (typed FeaturePython)
  n = 0.033
FEATURE [App::DocumentObjectGroupPython] O_element013  label="O_element : 0.745"  # scripted group (container) (typed FeaturePython)
  n = 0.745
FEATURE [App::DocumentObjectGroupPython] Na_element002  label="Na_element : 0.002"  # scripted group (container) (typed FeaturePython)
  n = 0.001
FEATURE [App::DocumentObjectGroupPython] P_element001  label="P_element : 0.001"  # scripted group (container) (typed FeaturePython)
  n = 0.001
FEATURE [App::DocumentObjectGroupPython] S_element003  label="S_element : 0.002"  # scripted group (container) (typed FeaturePython)
  n = 0.002
FEATURE [App::DocumentObjectGroupPython] Cl_element002  label="Cl_element : 0.003"  # scripted group (container) (typed FeaturePython)
  n = 0.003
FEATURE [App::DocumentObjectGroupPython] K_element001  label="K_element : 0.002"  # scripted group (container) (typed FeaturePython)
  n = 0.002
FEATURE [App::DocumentObjectGroupPython] Fe_element001  label="Fe_element : 0.001"  # scripted group (container) (typed FeaturePython)
  n = 0.001
FEATURE [App::DocumentObjectGroupPython] G4_BLOOD_ICRP  # scripted group (container) (typed FeaturePython)
  Dunit = g/cm3
  Dvalue = 1.06
  Group = -> [H_element014,C_element014,N_element009,O_element013,Na_element002,P_element001,S_element003,Cl_element002,K_element001,Fe_element001]
  conduct = 2
  density = 1
  expand = 3
  formula = G4_BLOOD_ICRP
  name = G4_BLOOD_ICRP
  specific = 4
FEATURE [App::DocumentObjectGroupPython] H_element015  label="H_element : 0.064"  # scripted group (container) (typed FeaturePython)
  n = 0.064
FEATURE [App::DocumentObjectGroupPython] C_element015  label="C_element : 0.278"  # scripted group (container) (typed FeaturePython)
  n = 0.278
FEATURE [App::DocumentObjectGroupPython] N_element010  label="N_element : 0.027"  # scripted group (container) (typed FeaturePython)
  n = 0.027
FEATURE [App::DocumentObjectGroupPython] O_element014  label="O_element : 0.410"  # scripted group (container) (typed FeaturePython)
  n = 0.41
FEATURE [App::DocumentObjectGroupPython] Mg_element001  label="Mg_element : 0.002"  # scripted group (container) (typed FeaturePython)
  n = 0.002
FEATURE [App::DocumentObjectGroupPython] P_element002  label="P_element : 0.070"  # scripted group (container) (typed FeaturePython)
  n = 0.07
FEATURE [App::DocumentObjectGroupPython] S_element004  label="S_element : 0.003"  # scripted group (container) (typed FeaturePython)
  n = 0.002
FEATURE [App::DocumentObjectGroupPython] Ca_element003  label="Ca_element : 0.147"  # scripted group (container) (typed FeaturePython)
  n = 0.147
FEATURE [App::DocumentObjectGroupPython] G4_BONE_COMPACT_ICRU  # scripted group (container) (typed FeaturePython)
  Dunit = g/cm3
  Dvalue = 1.85
  Group = -> [H_element015,C_element015,N_element010,O_element014,Mg_element001,P_element002,S_element004,Ca_element003]
  conduct = 2
  density = 1
  expand = 3
  formula = G4_BONE_COMPACT_ICRU
  name = G4_BONE_COMPACT_ICRU
  specific = 4
FEATURE [App::DocumentObjectGroupPython] H_element016  label="H_element : 0.034"  # scripted group (container) (typed FeaturePython)
  n = 0.034
FEATURE [App::DocumentObjectGroupPython] C_element016  label="C_element : 0.155"  # scripted group (container) (typed FeaturePython)
  n = 0.155
FEATURE [App::DocumentObjectGroupPython] N_element011  label="N_element : 0.042"  # scripted group (container) (typed FeaturePython)
  n = 0.042
FEATURE [App::DocumentObjectGroupPython] O_element015  label="O_element : 0.435"  # scripted group (container) (typed FeaturePython)
  n = 0.435
FEATURE [App::DocumentObjectGroupPython] Na_element003  label="Na_element : 0.003"  # scripted group (container) (typed FeaturePython)
  n = 0.001
FEATURE [App::DocumentObjectGroupPython] Mg_element002  label="Mg_element : 0.003"  # scripted group (container) (typed FeaturePython)
  n = 0.002
FEATURE [App::DocumentObjectGroupPython] P_element003  label="P_element : 0.103"  # scripted group (container) (typed FeaturePython)
  n = 0.103
FEATURE [App::DocumentObjectGroupPython] S_element005  label="S_element : 0.004"  # scripted group (container) (typed FeaturePython)
  n = 0.003
FEATURE [App::DocumentObjectGroupPython] Ca_element004  label="Ca_element : 0.225"  # scripted group (container) (typed FeaturePython)
  n = 0.225
FEATURE [App::DocumentObjectGroupPython] G4_BONE_CORTICAL_ICRP  # scripted group (container) (typed FeaturePython)
  Dunit = g/cm3
  Dvalue = 1.92
  Group = -> [H_element016,C_element016,N_element011,O_element015,Na_element003,Mg_element002,P_element003,S_element005,Ca_element004]
  conduct = 2
  density = 1
  expand = 3
  formula = G4_BONE_CORTICAL_ICRP
  name = G4_BONE_CORTICAL_ICRP
  specific = 4
FEATURE [App::DocumentObjectGroupPython] B_element001  label="B_element : 4"  # scripted group (container) (typed FeaturePython)
  n = 4
  ref = B_element
FEATURE [App::DocumentObjectGroupPython] C_element017  label="C_element : 1"  # scripted group (container) (typed FeaturePython)
  n = 1
  ref = C_element
FEATURE [App::DocumentObjectGroupPython] G4_BORON_CARBIDE  # scripted group (container) (typed FeaturePython)
  Dunit = g/cm3
  Dvalue = 2.52
  Group = -> [B_element001,C_element017]
  conduct = 2
  density = 1
  expand = 3
  formula = G4_BORON_CARBIDE
  name = G4_BORON_CARBIDE
  specific = 4
FEATURE [App::DocumentObjectGroupPython] B_element002  label="B_element : 2"  # scripted group (container) (typed FeaturePython)
  n = 2
  ref = B_element
FEATURE [App::DocumentObjectGroupPython] O_element016  label="O_element : 006"  # scripted group (container) (typed FeaturePython)
  n = 3
  ref = O_element
FEATURE [App::DocumentObjectGroupPython] G4_BORON_OXIDE  # scripted group (container) (typed FeaturePython)
  Dunit = g/cm3
  Dvalue = 1.812
  Group = -> [B_element002,O_element016]
  conduct = 2
  density = 1
  expand = 3
  formula = G4_BORON_OXIDE
  name = G4_BORON_OXIDE
  specific = 4
FEATURE [App::DocumentObjectGroupPython] H_element017  label="H_element : 0.107"  # scripted group (container) (typed FeaturePython)
  n = 0.107
FEATURE [App::DocumentObjectGroupPython] C_element018  label="C_element : 0.145"  # scripted group (container) (typed FeaturePython)
  n = 0.145
FEATURE [App::DocumentObjectGroupPython] N_element012  label="N_element : 0.022"  # scripted group (container) (typed FeaturePython)
  n = 0.022
FEATURE [App::DocumentObjectGroupPython] O_element017  label="O_element : 0.712"  # scripted group (container) (typed FeaturePython)
  n = 0.712
FEATURE [App::DocumentObjectGroupPython] Na_element004  label="Na_element : 0.004"  # scripted group (container) (typed FeaturePython)
  n = 0.002
FEATURE [App::DocumentObjectGroupPython] P_element004  label="P_element : 0.004"  # scripted group (container) (typed FeaturePython)
  n = 0.004
FEATURE [App::DocumentObjectGroupPython] S_element006  label="S_element : 0.005"  # scripted group (container) (typed FeaturePython)
  n = 0.002
FEATURE [App::DocumentObjectGroupPython] Cl_element003  label="Cl_element : 0.004"  # scripted group (container) (typed FeaturePython)
  n = 0.003
FEATURE [App::DocumentObjectGroupPython] K_element002  label="K_element : 0.003"  # scripted group (container) (typed FeaturePython)
  n = 0.003
FEATURE [App::DocumentObjectGroupPython] G4_BRAIN_ICRP  # scripted group (container) (typed FeaturePython)
  Dunit = g/cm3
  Dvalue = 1.04
  Group = -> [H_element017,C_element018,N_element012,O_element017,Na_element004,P_element004,S_element006,Cl_element003,K_element002]
  conduct = 2
  density = 1
  expand = 3
  formula = G4_BRAIN_ICRP
  name = G4_BRAIN_ICRP
  specific = 4
FEATURE [App::DocumentObjectGroupPython] C_element019  label="C_element : 4"  # scripted group (container) (typed FeaturePython)
  n = 4
  ref = C_element
FEATURE [App::DocumentObjectGroupPython] H_element018  label="H_element : 010"  # scripted group (container) (typed FeaturePython)
  n = 10
  ref = H_element
FEATURE [App::DocumentObjectGroupPython] G4_BUTANE  # scripted group (container) (typed FeaturePython)
  Dunit = g/cm3
  Dvalue = 0.00249343
  Group = -> [C_element019,H_element018]
  conduct = 2
  density = 1
  expand = 3
  formula = G4_BUTANE
  name = G4_BUTANE
  specific = 4
FEATURE [App::DocumentObjectGroupPython] C_element020  label="C_element : 008"  # scripted group (container) (typed FeaturePython)
  n = 4
  ref = C_element
FEATURE [App::DocumentObjectGroupPython] H_element019  label="H_element : 011"  # scripted group (container) (typed FeaturePython)
  n = 10
  ref = H_element
FEATURE [App::DocumentObjectGroupPython] O_element018  label="O_element : 007"  # scripted group (container) (typed FeaturePython)
  n = 1
  ref = O_element
FEATURE [App::DocumentObjectGroupPython] G4_N_BUTYL_ALCOHOL  label="G4_N-BUTYL_ALCOHOL"  # scripted group (container) (typed FeaturePython)
  Dunit = g/cm3
  Dvalue = 0.8098
  Group = -> [C_element020,H_element019,O_element018]
  conduct = 2
  density = 1
  expand = 3
  formula = G4_N-BUTYL_ALCOHOL
  name = G4_N-BUTYL_ALCOHOL
  specific = 4
FEATURE [App::DocumentObjectGroupPython] H_element020  label="H_element : 0.025"  # scripted group (container) (typed FeaturePython)
  n = 0.02468
FEATURE [App::DocumentObjectGroupPython] C_element021  label="C_element : 0.502"  # scripted group (container) (typed FeaturePython)
  n = 0.501611
FEATURE [App::DocumentObjectGroupPython] O_element019  label="O_element : 0.005"  # scripted group (container) (typed FeaturePython)
  n = 0.004527
FEATURE [App::DocumentObjectGroupPython] F_element004  label="F_element : 0.465"  # scripted group (container) (typed FeaturePython)
  n = 0.465209
FEATURE [App::DocumentObjectGroupPython] Si_element001  label="Si_element : 0.004"  # scripted group (container) (typed FeaturePython)
  n = 0.003973
FEATURE [App::DocumentObjectGroupPython] G4_C_552  label="G4_C-552"  # scripted group (container) (typed FeaturePython)
  Dunit = g/cm3
  Dvalue = 1.76
  Group = -> [H_element020,C_element021,O_element019,F_element004,Si_element001]
  conduct = 2
  density = 1
  expand = 3
  formula = G4_C-552
  name = G4_C-552
  specific = 4
FEATURE [App::DocumentObjectGroupPython] Cd_element001  label="Cd_element : 1"  # scripted group (container) (typed FeaturePython)
  n = 1
  ref = Cd_element
FEATURE [App::DocumentObjectGroupPython] Te_element001  label="Te_element : 1"  # scripted group (container) (typed FeaturePython)
  n = 1
  ref = Te_element
FEATURE [App::DocumentObjectGroupPython] G4_CADMIUM_TELLURIDE  # scripted group (container) (typed FeaturePython)
  Dunit = g/cm3
  Dvalue = 6.2
  Group = -> [Cd_element001,Te_element001]
  conduct = 2
  density = 1
  expand = 3
  formula = G4_CADMIUM_TELLURIDE
  name = G4_CADMIUM_TELLURIDE
  specific = 4
FEATURE [App::DocumentObjectGroupPython] Cd_element002  label="Cd_element : 002"  # scripted group (container) (typed FeaturePython)
  n = 1
  ref = Cd_element
FEATURE [App::DocumentObjectGroupPython] W_element001  label="W_element : 1"  # scripted group (container) (typed FeaturePython)
  n = 1
  ref = W_element
FEATURE [App::DocumentObjectGroupPython] O_element020  label="O_element : 008"  # scripted group (container) (typed FeaturePython)
  n = 4
  ref = O_element
FEATURE [App::DocumentObjectGroupPython] G4_CADMIUM_TUNGSTATE  # scripted group (container) (typed FeaturePython)
  Dunit = g/cm3
  Dvalue = 7.9
  Group = -> [Cd_element002,W_element001,O_element020]
  conduct = 2
  density = 1
  expand = 3
  formula = G4_CADMIUM_TUNGSTATE
  name = G4_CADMIUM_TUNGSTATE
  specific = 4
FEATURE [App::DocumentObjectGroupPython] Ca_element005  label="Ca_element : 1"  # scripted group (container) (typed FeaturePython)
  n = 1
  ref = Ca_element
FEATURE [App::DocumentObjectGroupPython] C_element022  label="C_element : 009"  # scripted group (container) (typed FeaturePython)
  n = 1
  ref = C_element
FEATURE [App::DocumentObjectGroupPython] O_element021  label="O_element : 009"  # scripted group (container) (typed FeaturePython)
  n = 3
  ref = O_element
FEATURE [App::DocumentObjectGroupPython] G4_CALCIUM_CARBONATE  # scripted group (container) (typed FeaturePython)
  Dunit = g/cm3
  Dvalue = 2.8
  Group = -> [Ca_element005,C_element022,O_element021]
  conduct = 2
  density = 1
  expand = 3
  formula = G4_CALCIUM_CARBONATE
  name = G4_CALCIUM_CARBONATE
  specific = 4
FEATURE [App::DocumentObjectGroupPython] Ca_element006  label="Ca_element : 002"  # scripted group (container) (typed FeaturePython)
  n = 1
  ref = Ca_element
FEATURE [App::DocumentObjectGroupPython] F_element005  label="F_element : 003"  # scripted group (container) (typed FeaturePython)
  n = 2
  ref = F_element
FEATURE [App::DocumentObjectGroupPython] G4_CALCIUM_FLUORIDE  # scripted group (container) (typed FeaturePython)
  Dunit = g/cm3
  Dvalue = 3.18
  Group = -> [Ca_element006,F_element005]
  conduct = 2
  density = 1
  expand = 3
  formula = G4_CALCIUM_FLUORIDE
  name = G4_CALCIUM_FLUORIDE
  specific = 4
FEATURE [App::DocumentObjectGroupPython] Ca_element007  label="Ca_element : 003"  # scripted group (container) (typed FeaturePython)
  n = 1
  ref = Ca_element
FEATURE [App::DocumentObjectGroupPython] O_element022  label="O_element : 010"  # scripted group (container) (typed FeaturePython)
  n = 1
  ref = O_element
FEATURE [App::DocumentObjectGroupPython] G4_CALCIUM_OXIDE  # scripted group (container) (typed FeaturePython)
  Dunit = g/cm3
  Dvalue = 3.3
  Group = -> [Ca_element007,O_element022]
  conduct = 2
  density = 1
  expand = 3
  formula = G4_CALCIUM_OXIDE
  name = G4_CALCIUM_OXIDE
  specific = 4
FEATURE [App::DocumentObjectGroupPython] Ca_element008  label="Ca_element : 004"  # scripted group (container) (typed FeaturePython)
  n = 1
  ref = Ca_element
FEATURE [App::DocumentObjectGroupPython] S_element007  label="S_element : 002"  # scripted group (container) (typed FeaturePython)
  n = 1
  ref = S_element
FEATURE [App::DocumentObjectGroupPython] O_element023  label="O_element : 011"  # scripted group (container) (typed FeaturePython)
  n = 4
  ref = O_element
FEATURE [App::DocumentObjectGroupPython] G4_CALCIUM_SULFATE  # scripted group (container) (typed FeaturePython)
  Dunit = g/cm3
  Dvalue = 2.96
  Group = -> [Ca_element008,S_element007,O_element023]
  conduct = 2
  density = 1
  expand = 3
  formula = G4_CALCIUM_SULFATE
  name = G4_CALCIUM_SULFATE
  specific = 4
FEATURE [App::DocumentObjectGroupPython] Ca_element009  label="Ca_element : 005"  # scripted group (container) (typed FeaturePython)
  n = 1
  ref = Ca_element
FEATURE [App::DocumentObjectGroupPython] W_element002  label="W_element : 002"  # scripted group (container) (typed FeaturePython)
  n = 1
  ref = W_element
FEATURE [App::DocumentObjectGroupPython] O_element024  label="O_element : 012"  # scripted group (container) (typed FeaturePython)
  n = 4
  ref = O_element
FEATURE [App::DocumentObjectGroupPython] G4_CALCIUM_TUNGSTATE  # scripted group (container) (typed FeaturePython)
  Dunit = g/cm3
  Dvalue = 6.062
  Group = -> [Ca_element009,W_element002,O_element024]
  conduct = 2
  density = 1
  expand = 3
  formula = G4_CALCIUM_TUNGSTATE
  name = G4_CALCIUM_TUNGSTATE
  specific = 4
FEATURE [App::DocumentObjectGroupPython] C_element023  label="C_element : 010"  # scripted group (container) (typed FeaturePython)
  n = 1
  ref = C_element
FEATURE [App::DocumentObjectGroupPython] O_element025  label="O_element : 013"  # scripted group (container) (typed FeaturePython)
  n = 2
  ref = O_element
FEATURE [App::DocumentObjectGroupPython] G4_CARBON_DIOXIDE  # scripted group (container) (typed FeaturePython)
  Dunit = g/cm3
  Dvalue = 0.00184212
  Group = -> [C_element023,O_element025]
  conduct = 2
  density = 1
  expand = 3
  formula = G4_CARBON_DIOXIDE
  name = G4_CARBON_DIOXIDE
  specific = 4
FEATURE [App::DocumentObjectGroupPython] C_element024  label="C_element : 011"  # scripted group (container) (typed FeaturePython)
  n = 1
  ref = C_element
FEATURE [App::DocumentObjectGroupPython] Cl_element004  label="Cl_element : 4"  # scripted group (container) (typed FeaturePython)
  n = 4
  ref = Cl_element
FEATURE [App::DocumentObjectGroupPython] G4_CARBON_TETRACHLORIDE  # scripted group (container) (typed FeaturePython)
  Dunit = g/cm3
  Dvalue = 1.594
  Group = -> [C_element024,Cl_element004]
  conduct = 2
  density = 1
  expand = 3
  formula = G4_CARBON_TETRACHLORIDE
  name = G4_CARBON_TETRACHLORIDE
  specific = 4
FEATURE [App::DocumentObjectGroupPython] C_element025  label="C_element : 012"  # scripted group (container) (typed FeaturePython)
  n = 6
  ref = C_element
FEATURE [App::DocumentObjectGroupPython] H_element021  label="H_element : 012"  # scripted group (container) (typed FeaturePython)
  n = 10
  ref = H_element
FEATURE [App::DocumentObjectGroupPython] O_element026  label="O_element : 5"  # scripted group (container) (typed FeaturePython)
  n = 5
  ref = O_element
FEATURE [App::DocumentObjectGroupPython] G4_CELLULOSE_CELLOPHANE  # scripted group (container) (typed FeaturePython)
  Dunit = g/cm3
  Dvalue = 1.42
  Group = -> [C_element025,H_element021,O_element026]
  conduct = 2
  density = 1
  expand = 3
  formula = G4_CELLULOSE_CELLOPHANE
  name = G4_CELLULOSE_CELLOPHANE
  specific = 4
FEATURE [App::DocumentObjectGroupPython] H_element022  label="H_element : 0.067"  # scripted group (container) (typed FeaturePython)
  n = 0.067125
FEATURE [App::DocumentObjectGroupPython] C_element026  label="C_element : 0.545"  # scripted group (container) (typed FeaturePython)
  n = 0.545403
FEATURE [App::DocumentObjectGroupPython] O_element027  label="O_element : 0.387"  # scripted group (container) (typed FeaturePython)
  n = 0.387472
FEATURE [App::DocumentObjectGroupPython] G4_CELLULOSE_BUTYRATE  # scripted group (container) (typed FeaturePython)
  Dunit = g/cm3
  Dvalue = 1.2
  Group = -> [H_element022,C_element026,O_element027]
  conduct = 2
  density = 1
  expand = 3
  formula = G4_CELLULOSE_BUTYRATE
  name = G4_CELLULOSE_BUTYRATE
  specific = 4
FEATURE [App::DocumentObjectGroupPython] H_element023  label="H_element : 0.029"  # scripted group (container) (typed FeaturePython)
  n = 0.029216
FEATURE [App::DocumentObjectGroupPython] C_element027  label="C_element : 0.271"  # scripted group (container) (typed FeaturePython)
  n = 0.271296
FEATURE [App::DocumentObjectGroupPython] N_element013  label="N_element : 0.121"  # scripted group (container) (typed FeaturePython)
  n = 0.121276
FEATURE [App::DocumentObjectGroupPython] O_element028  label="O_element : 0.578"  # scripted group (container) (typed FeaturePython)
  n = 0.578212
FEATURE [App::DocumentObjectGroupPython] G4_CELLULOSE_NITRATE  # scripted group (container) (typed FeaturePython)
  Dunit = g/cm3
  Dvalue = 1.49
  Group = -> [H_element023,C_element027,N_element013,O_element028]
  conduct = 2
  density = 1
  expand = 3
  formula = G4_CELLULOSE_NITRATE
  name = G4_CELLULOSE_NITRATE
  specific = 4
FEATURE [App::DocumentObjectGroupPython] H_element024  label="H_element : 0.108"  # scripted group (container) (typed FeaturePython)
  n = 0.107596
FEATURE [App::DocumentObjectGroupPython] N_element014  label="N_element : 0.001"  # scripted group (container) (typed FeaturePython)
  n = 0.0008
FEATURE [App::DocumentObjectGroupPython] O_element029  label="O_element : 0.875"  # scripted group (container) (typed FeaturePython)
  n = 0.874976
FEATURE [App::DocumentObjectGroupPython] S_element008  label="S_element : 0.015"  # scripted group (container) (typed FeaturePython)
  n = 0.014627
FEATURE [App::DocumentObjectGroupPython] Ce_element001  label="Ce_element : 0.002"  # scripted group (container) (typed FeaturePython)
  n = 0.002001
FEATURE [App::DocumentObjectGroupPython] G4_CERIC_SULFATE  # scripted group (container) (typed FeaturePython)
  Dunit = g/cm3
  Dvalue = 1.03
  Group = -> [H_element024,N_element014,O_element029,S_element008,Ce_element001]
  conduct = 2
  density = 1
  expand = 3
  formula = G4_CERIC_SULFATE
  name = G4_CERIC_SULFATE
  specific = 4
FEATURE [App::DocumentObjectGroupPython] Cs_element001  label="Cs_element : 1"  # scripted group (container) (typed FeaturePython)
  n = 1
  ref = Cs_element
FEATURE [App::DocumentObjectGroupPython] F_element006  label="F_element : 1"  # scripted group (container) (typed FeaturePython)
  n = 1
  ref = F_element
FEATURE [App::DocumentObjectGroupPython] G4_CESIUM_FLUORIDE  # scripted group (container) (typed FeaturePython)
  Dunit = g/cm3
  Dvalue = 4.115
  Group = -> [Cs_element001,F_element006]
  conduct = 2
  density = 1
  expand = 3
  formula = G4_CESIUM_FLUORIDE
  name = G4_CESIUM_FLUORIDE
  specific = 4
FEATURE [App::DocumentObjectGroupPython] Cs_element002  label="Cs_element : 002"  # scripted group (container) (typed FeaturePython)
  n = 1
  ref = Cs_element
FEATURE [App::DocumentObjectGroupPython] I_element001  label="I_element : 1"  # scripted group (container) (typed FeaturePython)
  n = 1
  ref = I_element
FEATURE [App::DocumentObjectGroupPython] G4_CESIUM_IODIDE  # scripted group (container) (typed FeaturePython)
  Dunit = g/cm3
  Dvalue = 4.51
  Group = -> [Cs_element002,I_element001]
  conduct = 2
  density = 1
  expand = 3
  formula = G4_CESIUM_IODIDE
  name = G4_CESIUM_IODIDE
  specific = 4
FEATURE [App::DocumentObjectGroupPython] C_element028  label="C_element : 013"  # scripted group (container) (typed FeaturePython)
  n = 6
  ref = C_element
FEATURE [App::DocumentObjectGroupPython] H_element025  label="H_element : 013"  # scripted group (container) (typed FeaturePython)
  n = 5
  ref = H_element
FEATURE [App::DocumentObjectGroupPython] Cl_element005  label="Cl_element : 1"  # scripted group (container) (typed FeaturePython)
  n = 1
  ref = Cl_element
FEATURE [App::DocumentObjectGroupPython] G4_CHLOROBENZENE  # scripted group (container) (typed FeaturePython)
  Dunit = g/cm3
  Dvalue = 1.1058
  Group = -> [C_element028,H_element025,Cl_element005]
  conduct = 2
  density = 1
  expand = 3
  formula = G4_CHLOROBENZENE
  name = G4_CHLOROBENZENE
  specific = 4
FEATURE [App::DocumentObjectGroupPython] C_element029  label="C_element : 014"  # scripted group (container) (typed FeaturePython)
  n = 1
  ref = C_element
FEATURE [App::DocumentObjectGroupPython] H_element026  label="H_element : 1"  # scripted group (container) (typed FeaturePython)
  n = 1
  ref = H_element
FEATURE [App::DocumentObjectGroupPython] Cl_element006  label="Cl_element : 3"  # scripted group (container) (typed FeaturePython)
  n = 3
  ref = Cl_element
FEATURE [App::DocumentObjectGroupPython] G4_CHLOROFORM  # scripted group (container) (typed FeaturePython)
  Dunit = g/cm3
  Dvalue = 1.4832
  Group = -> [C_element029,H_element026,Cl_element006]
  conduct = 2
  density = 1
  expand = 3
  formula = G4_CHLOROFORM
  name = G4_CHLOROFORM
  specific = 4
FEATURE [App::DocumentObjectGroupPython] H_element027  label="H_element : 0.010"  # scripted group (container) (typed FeaturePython)
  n = 0.01
FEATURE [App::DocumentObjectGroupPython] C_element030  label="C_element : 0.001"  # scripted group (container) (typed FeaturePython)
  n = 0.001
FEATURE [App::DocumentObjectGroupPython] O_element030  label="O_element : 0.529"  # scripted group (container) (typed FeaturePython)
  n = 0.529107
FEATURE [App::DocumentObjectGroupPython] Na_element005  label="Na_element : 0.016"  # scripted group (container) (typed FeaturePython)
  n = 0.016
FEATURE [App::DocumentObjectGroupPython] Mg_element003  label="Mg_element : 0.004"  # scripted group (container) (typed FeaturePython)
  n = 0.002
FEATURE [App::DocumentObjectGroupPython] Al_element002  label="Al_element : 0.034"  # scripted group (container) (typed FeaturePython)
  n = 0.033872
FEATURE [App::DocumentObjectGroupPython] Si_element002  label="Si_element : 0.337"  # scripted group (container) (typed FeaturePython)
  n = 0.337021
FEATURE [App::DocumentObjectGroupPython] K_element003  label="K_element : 0.013"  # scripted group (container) (typed FeaturePython)
  n = 0.013
FEATURE [App::DocumentObjectGroupPython] Ca_element010  label="Ca_element : 0.044"  # scripted group (container) (typed FeaturePython)
  n = 0.044
FEATURE [App::DocumentObjectGroupPython] Fe_element002  label="Fe_element : 0.014"  # scripted group (container) (typed FeaturePython)
  n = 0.014
FEATURE [App::DocumentObjectGroupPython] G4_CONCRETE  # scripted group (container) (typed FeaturePython)
  Dunit = g/cm3
  Dvalue = 2.3
  Group = -> [H_element027,C_element030,O_element030,Na_element005,Mg_element003,Al_element002,Si_element002,K_element003,Ca_element010,Fe_element002]
  conduct = 2
  density = 1
  expand = 3
  formula = G4_CONCRETE
  name = G4_CONCRETE
  specific = 4
FEATURE [App::DocumentObjectGroupPython] C_element031  label="C_element : 015"  # scripted group (container) (typed FeaturePython)
  n = 6
  ref = C_element
FEATURE [App::DocumentObjectGroupPython] H_element028  label="H_element : 12"  # scripted group (container) (typed FeaturePython)
  n = 12
  ref = H_element
FEATURE [App::DocumentObjectGroupPython] G4_CYCLOHEXANE  # scripted group (container) (typed FeaturePython)
  Dunit = g/cm3
  Dvalue = 0.779
  Group = -> [C_element031,H_element028]
  conduct = 2
  density = 1
  expand = 3
  formula = G4_CYCLOHEXANE
  name = G4_CYCLOHEXANE
  specific = 4
FEATURE [App::DocumentObjectGroupPython] C_element032  label="C_element : 016"  # scripted group (container) (typed FeaturePython)
  n = 6
  ref = C_element
FEATURE [App::DocumentObjectGroupPython] H_element029  label="H_element : 4"  # scripted group (container) (typed FeaturePython)
  n = 4
  ref = H_element
FEATURE [App::DocumentObjectGroupPython] Cl_element007  label="Cl_element : 2"  # scripted group (container) (typed FeaturePython)
  n = 2
  ref = Cl_element
FEATURE [App::DocumentObjectGroupPython] G4_1_2_DICHLOROBENZENE  label="G4_1.2-DICHLOROBENZENE"  # scripted group (container) (typed FeaturePython)
  Dunit = g/cm3
  Dvalue = 1.3048
  Group = -> [C_element032,H_element029,Cl_element007]
  conduct = 2
  density = 1
  expand = 3
  formula = G4_1.2-DICHLOROBENZENE
  name = G4_1.2-DICHLOROBENZENE
  specific = 4
FEATURE [App::DocumentObjectGroupPython] C_element033  label="C_element : 017"  # scripted group (container) (typed FeaturePython)
  n = 4
  ref = C_element
FEATURE [App::DocumentObjectGroupPython] H_element030  label="H_element : 8"  # scripted group (container) (typed FeaturePython)
  n = 8
  ref = H_element
FEATURE [App::DocumentObjectGroupPython] O_element031  label="O_element : 014"  # scripted group (container) (typed FeaturePython)
  n = 1
  ref = O_element
FEATURE [App::DocumentObjectGroupPython] Cl_element008  label="Cl_element : 005"  # scripted group (container) (typed FeaturePython)
  n = 2
  ref = Cl_element
FEATURE [App::DocumentObjectGroupPython] G4_DICHLORODIETHYL_ETHER  # scripted group (container) (typed FeaturePython)
  Dunit = g/cm3
  Dvalue = 1.2199
  Group = -> [C_element033,H_element030,O_element031,Cl_element008]
  conduct = 2
  density = 1
  expand = 3
  formula = G4_DICHLORODIETHYL_ETHER
  name = G4_DICHLORODIETHYL_ETHER
  specific = 4
FEATURE [App::DocumentObjectGroupPython] C_element034  label="C_element : 018"  # scripted group (container) (typed FeaturePython)
  n = 2
  ref = C_element
FEATURE [App::DocumentObjectGroupPython] H_element031  label="H_element : 014"  # scripted group (container) (typed FeaturePython)
  n = 4
  ref = H_element
FEATURE [App::DocumentObjectGroupPython] Cl_element009  label="Cl_element : 006"  # scripted group (container) (typed FeaturePython)
  n = 2
  ref = Cl_element
FEATURE [App::DocumentObjectGroupPython] G4_1_2_DICHLOROETHANE  label="G4_1.2-DICHLOROETHANE"  # scripted group (container) (typed FeaturePython)
  Dunit = g/cm3
  Dvalue = 1.2351
  Group = -> [C_element034,H_element031,Cl_element009]
  conduct = 2
  density = 1
  expand = 3
  formula = G4_1.2-DICHLOROETHANE
  name = G4_1.2-DICHLOROETHANE
  specific = 4
FEATURE [App::DocumentObjectGroupPython] C_element035  label="C_element : 019"  # scripted group (container) (typed FeaturePython)
  n = 4
  ref = C_element
FEATURE [App::DocumentObjectGroupPython] H_element032  label="H_element : 015"  # scripted group (container) (typed FeaturePython)
  n = 10
  ref = H_element
FEATURE [App::DocumentObjectGroupPython] O_element032  label="O_element : 015"  # scripted group (container) (typed FeaturePython)
  n = 1
  ref = O_element
FEATURE [App::DocumentObjectGroupPython] G4_DIETHYL_ETHER  # scripted group (container) (typed FeaturePython)
  Dunit = g/cm3
  Dvalue = 0.71378
  Group = -> [C_element035,H_element032,O_element032]
  conduct = 2
  density = 1
  expand = 3
  formula = G4_DIETHYL_ETHER
  name = G4_DIETHYL_ETHER
  specific = 4
FEATURE [App::DocumentObjectGroupPython] C_element036  label="C_element : 020"  # scripted group (container) (typed FeaturePython)
  n = 3
  ref = C_element
FEATURE [App::DocumentObjectGroupPython] H_element033  label="H_element : 016"  # scripted group (container) (typed FeaturePython)
  n = 7
  ref = H_element
FEATURE [App::DocumentObjectGroupPython] N_element015  label="N_element : 008"  # scripted group (container) (typed FeaturePython)
  n = 1
  ref = N_element
FEATURE [App::DocumentObjectGroupPython] O_element033  label="O_element : 016"  # scripted group (container) (typed FeaturePython)
  n = 1
  ref = O_element
FEATURE [App::DocumentObjectGroupPython] G4_N_N_DIMETHYL_FORMAMIDE  label="G4_N.N-DIMETHYL_FORMAMIDE"  # scripted group (container) (typed FeaturePython)
  Dunit = g/cm3
  Dvalue = 0.9487
  Group = -> [C_element036,H_element033,N_element015,O_element033]
  conduct = 2
  density = 1
  expand = 3
  formula = G4_N.N-DIMETHYL_FORMAMIDE
  name = G4_N.N-DIMETHYL_FORMAMIDE
  specific = 4
FEATURE [App::DocumentObjectGroupPython] C_element037  label="C_element : 021"  # scripted group (container) (typed FeaturePython)
  n = 2
  ref = C_element
FEATURE [App::DocumentObjectGroupPython] H_element034  label="H_element : 017"  # scripted group (container) (typed FeaturePython)
  n = 6
  ref = H_element
FEATURE [App::DocumentObjectGroupPython] O_element034  label="O_element : 017"  # scripted group (container) (typed FeaturePython)
  n = 1
  ref = O_element
FEATURE [App::DocumentObjectGroupPython] S_element009  label="S_element : 003"  # scripted group (container) (typed FeaturePython)
  n = 1
  ref = S_element
FEATURE [App::DocumentObjectGroupPython] G4_DIMETHYL_SULFOXIDE  # scripted group (container) (typed FeaturePython)
  Dunit = g/cm3
  Dvalue = 1.1014
  Group = -> [C_element037,H_element034,O_element034,S_element009]
  conduct = 2
  density = 1
  expand = 3
  formula = G4_DIMETHYL_SULFOXIDE
  name = G4_DIMETHYL_SULFOXIDE
  specific = 4
FEATURE [App::DocumentObjectGroupPython] C_element038  label="C_element : 022"  # scripted group (container) (typed FeaturePython)
  n = 2
  ref = C_element
FEATURE [App::DocumentObjectGroupPython] H_element035  label="H_element : 018"  # scripted group (container) (typed FeaturePython)
  n = 6
  ref = H_element
FEATURE [App::DocumentObjectGroupPython] G4_ETHANE  # scripted group (container) (typed FeaturePython)
  Dunit = g/cm3
  Dvalue = 0.00125324
  Group = -> [C_element038,H_element035]
  conduct = 2
  density = 1
  expand = 3
  formula = G4_ETHANE
  name = G4_ETHANE
  specific = 4
FEATURE [App::DocumentObjectGroupPython] C_element039  label="C_element : 023"  # scripted group (container) (typed FeaturePython)
  n = 2
  ref = C_element
FEATURE [App::DocumentObjectGroupPython] H_element036  label="H_element : 019"  # scripted group (container) (typed FeaturePython)
  n = 6
  ref = H_element
FEATURE [App::DocumentObjectGroupPython] O_element035  label="O_element : 018"  # scripted group (container) (typed FeaturePython)
  n = 1
  ref = O_element
FEATURE [App::DocumentObjectGroupPython] G4_ETHYL_ALCOHOL  # scripted group (container) (typed FeaturePython)
  Dunit = g/cm3
  Dvalue = 0.7893
  Group = -> [C_element039,H_element036,O_element035]
  conduct = 2
  density = 1
  expand = 3
  formula = G4_ETHYL_ALCOHOL
  name = G4_ETHYL_ALCOHOL
  specific = 4
FEATURE [App::DocumentObjectGroupPython] H_element037  label="H_element : 0.090"  # scripted group (container) (typed FeaturePython)
  n = 0.090027
FEATURE [App::DocumentObjectGroupPython] C_element040  label="C_element : 0.585"  # scripted group (container) (typed FeaturePython)
  n = 0.585182
FEATURE [App::DocumentObjectGroupPython] O_element036  label="O_element : 0.325"  # scripted group (container) (typed FeaturePython)
  n = 0.324791
FEATURE [App::DocumentObjectGroupPython] G4_ETHYL_CELLULOSE  # scripted group (container) (typed FeaturePython)
  Dunit = g/cm3
  Dvalue = 1.13
  Group = -> [H_element037,C_element040,O_element036]
  conduct = 2
  density = 1
  expand = 3
  formula = G4_ETHYL_CELLULOSE
  name = G4_ETHYL_CELLULOSE
  specific = 4
FEATURE [App::DocumentObjectGroupPython] C_element041  label="C_element : 024"  # scripted group (container) (typed FeaturePython)
  n = 2
  ref = C_element
FEATURE [App::DocumentObjectGroupPython] H_element038  label="H_element : 020"  # scripted group (container) (typed FeaturePython)
  n = 4
  ref = H_element
FEATURE [App::DocumentObjectGroupPython] G4_ETHYLENE  # scripted group (container) (typed FeaturePython)
  Dunit = g/cm3
  Dvalue = 0.00117497
  Group = -> [C_element041,H_element038]
  conduct = 2
  density = 1
  expand = 3
  formula = G4_ETHYLENE
  name = G4_ETHYLENE
  specific = 4
FEATURE [App::DocumentObjectGroupPython] H_element039  label="H_element : 0.096"  # scripted group (container) (typed FeaturePython)
  n = 0.096
FEATURE [App::DocumentObjectGroupPython] C_element042  label="C_element : 0.195"  # scripted group (container) (typed FeaturePython)
  n = 0.195
FEATURE [App::DocumentObjectGroupPython] N_element016  label="N_element : 0.057"  # scripted group (container) (typed FeaturePython)
  n = 0.057
FEATURE [App::DocumentObjectGroupPython] O_element037  label="O_element : 0.646"  # scripted group (container) (typed FeaturePython)
  n = 0.646
FEATURE [App::DocumentObjectGroupPython] Na_element006  label="Na_element : 0.017"  # scripted group (container) (typed FeaturePython)
  n = 0.001
FEATURE [App::DocumentObjectGroupPython] P_element005  label="P_element : 0.104"  # scripted group (container) (typed FeaturePython)
  n = 0.001
FEATURE [App::DocumentObjectGroupPython] S_element010  label="S_element : 0.016"  # scripted group (container) (typed FeaturePython)
  n = 0.003
FEATURE [App::DocumentObjectGroupPython] Cl_element010  label="Cl_element : 0.005"  # scripted group (container) (typed FeaturePython)
  n = 0.001
FEATURE [App::DocumentObjectGroupPython] G4_EYE_LENS_ICRP  # scripted group (container) (typed FeaturePython)
  Dunit = g/cm3
  Dvalue = 1.07
  Group = -> [H_element039,C_element042,N_element016,O_element037,Na_element006,P_element005,S_element010,Cl_element010]
  conduct = 2
  density = 1
  expand = 3
  formula = G4_EYE_LENS_ICRP
  name = G4_EYE_LENS_ICRP
  specific = 4
FEATURE [App::DocumentObjectGroupPython] Fe_element003  label="Fe_element : 2"  # scripted group (container) (typed FeaturePython)
  n = 2
  ref = Fe_element
FEATURE [App::DocumentObjectGroupPython] O_element038  label="O_element : 019"  # scripted group (container) (typed FeaturePython)
  n = 3
  ref = O_element
FEATURE [App::DocumentObjectGroupPython] G4_FERRIC_OXIDE  # scripted group (container) (typed FeaturePython)
  Dunit = g/cm3
  Dvalue = 5.2
  Group = -> [Fe_element003,O_element038]
  conduct = 2
  density = 1
  expand = 3
  formula = G4_FERRIC_OXIDE
  name = G4_FERRIC_OXIDE
  specific = 4
FEATURE [App::DocumentObjectGroupPython] Fe_element004  label="Fe_element : 1"  # scripted group (container) (typed FeaturePython)
  n = 1
  ref = Fe_element
FEATURE [App::DocumentObjectGroupPython] B_element003  label="B_element : 1"  # scripted group (container) (typed FeaturePython)
  n = 1
  ref = B_element
FEATURE [App::DocumentObjectGroupPython] G4_FERROBORIDE  # scripted group (container) (typed FeaturePython)
  Dunit = g/cm3
  Dvalue = 7.15
  Group = -> [Fe_element004,B_element003]
  conduct = 2
  density = 1
  expand = 3
  formula = G4_FERROBORIDE
  name = G4_FERROBORIDE
  specific = 4
FEATURE [App::DocumentObjectGroupPython] Fe_element005  label="Fe_element : 003"  # scripted group (container) (typed FeaturePython)
  n = 1
  ref = Fe_element
FEATURE [App::DocumentObjectGroupPython] O_element039  label="O_element : 020"  # scripted group (container) (typed FeaturePython)
  n = 1
  ref = O_element
FEATURE [App::DocumentObjectGroupPython] G4_FERROUS_OXIDE  # scripted group (container) (typed FeaturePython)
  Dunit = g/cm3
  Dvalue = 5.7
  Group = -> [Fe_element005,O_element039]
  conduct = 2
  density = 1
  expand = 3
  formula = G4_FERROUS_OXIDE
  name = G4_FERROUS_OXIDE
  specific = 4
FEATURE [App::DocumentObjectGroupPython] H_element040  label="H_element : 0.115"  # scripted group (container) (typed FeaturePython)
  n = 0.108259
FEATURE [App::DocumentObjectGroupPython] N_element017  label="N_element : 0.000"  # scripted group (container) (typed FeaturePython)
  n = 2.7e-05
FEATURE [App::DocumentObjectGroupPython] O_element040  label="O_element : 0.879"  # scripted group (container) (typed FeaturePython)
  n = 0.878636
FEATURE [App::DocumentObjectGroupPython] Na_element007  label="Na_element : 0.000"  # scripted group (container) (typed FeaturePython)
  n = 2.2e-05
FEATURE [App::DocumentObjectGroupPython] S_element011  label="S_element : 0.013"  # scripted group (container) (typed FeaturePython)
  n = 0.012968
FEATURE [App::DocumentObjectGroupPython] Cl_element011  label="Cl_element : 0.000"  # scripted group (container) (typed FeaturePython)
  n = 3.4e-05
FEATURE [App::DocumentObjectGroupPython] Fe_element006  label="Fe_element : 0.000"  # scripted group (container) (typed FeaturePython)
  n = 5.4e-05
FEATURE [App::DocumentObjectGroupPython] G4_FERROUS_SULFATE  # scripted group (container) (typed FeaturePython)
  Dunit = g/cm3
  Dvalue = 1.024
  Group = -> [H_element040,N_element017,O_element040,Na_element007,S_element011,Cl_element011,Fe_element006]
  conduct = 2
  density = 1
  expand = 3
  formula = G4_FERROUS_SULFATE
  name = G4_FERROUS_SULFATE
  specific = 4
FEATURE [App::DocumentObjectGroupPython] C_element043  label="C_element : 0.099"  # scripted group (container) (typed FeaturePython)
  n = 0.099335
FEATURE [App::DocumentObjectGroupPython] F_element007  label="F_element : 0.314"  # scripted group (container) (typed FeaturePython)
  n = 0.314247
FEATURE [App::DocumentObjectGroupPython] Cl_element012  label="Cl_element : 0.586"  # scripted group (container) (typed FeaturePython)
  n = 0.586418
FEATURE [App::DocumentObjectGroupPython] G4_FREON_12  label="G4_FREON-12"  # scripted group (container) (typed FeaturePython)
  Dunit = g/cm3
  Dvalue = 1.12
  Group = -> [C_element043,F_element007,Cl_element012]
  conduct = 2
  density = 1
  expand = 3
  formula = G4_FREON-12
  name = G4_FREON-12
  specific = 4
FEATURE [App::DocumentObjectGroupPython] C_element044  label="C_element : 0.057"  # scripted group (container) (typed FeaturePython)
  n = 0.057245
FEATURE [App::DocumentObjectGroupPython] F_element008  label="F_element : 0.181"  # scripted group (container) (typed FeaturePython)
  n = 0.181096
FEATURE [App::DocumentObjectGroupPython] Br_element001  label="Br_element : 0.762"  # scripted group (container) (typed FeaturePython)
  n = 0.761659
FEATURE [App::DocumentObjectGroupPython] G4_FREON_12B2  label="G4_FREON-12B2"  # scripted group (container) (typed FeaturePython)
  Dunit = g/cm3
  Dvalue = 1.8
  Group = -> [C_element044,F_element008,Br_element001]
  conduct = 2
  density = 1
  expand = 3
  formula = G4_FREON-12B2
  name = G4_FREON-12B2
  specific = 4
FEATURE [App::DocumentObjectGroupPython] C_element045  label="C_element : 0.115"  # scripted group (container) (typed FeaturePython)
  n = 0.114983
FEATURE [App::DocumentObjectGroupPython] F_element009  label="F_element : 0.546"  # scripted group (container) (typed FeaturePython)
  n = 0.545621
FEATURE [App::DocumentObjectGroupPython] Cl_element013  label="Cl_element : 0.339"  # scripted group (container) (typed FeaturePython)
  n = 0.339396
FEATURE [App::DocumentObjectGroupPython] G4_FREON_13  label="G4_FREON-13"  # scripted group (container) (typed FeaturePython)
  Dunit = g/cm3
  Dvalue = 0.95
  Group = -> [C_element045,F_element009,Cl_element013]
  conduct = 2
  density = 1
  expand = 3
  formula = G4_FREON-13
  name = G4_FREON-13
  specific = 4
FEATURE [App::DocumentObjectGroupPython] C_element046  label="C_element : 025"  # scripted group (container) (typed FeaturePython)
  n = 1
  ref = C_element
FEATURE [App::DocumentObjectGroupPython] F_element010  label="F_element : 3"  # scripted group (container) (typed FeaturePython)
  n = 3
  ref = F_element
FEATURE [App::DocumentObjectGroupPython] Br_element002  label="Br_element : 1"  # scripted group (container) (typed FeaturePython)
  n = 1
  ref = Br_element
FEATURE [App::DocumentObjectGroupPython] G4_FREON_13B1  label="G4_FREON-13B1"  # scripted group (container) (typed FeaturePython)
  Dunit = g/cm3
  Dvalue = 1.5
  Group = -> [C_element046,F_element010,Br_element002]
  conduct = 2
  density = 1
  expand = 3
  formula = G4_FREON-13B1
  name = G4_FREON-13B1
  specific = 4
FEATURE [App::DocumentObjectGroupPython] C_element047  label="C_element : 0.061"  # scripted group (container) (typed FeaturePython)
  n = 0.061309
FEATURE [App::DocumentObjectGroupPython] F_element011  label="F_element : 0.291"  # scripted group (container) (typed FeaturePython)
  n = 0.290924
FEATURE [App::DocumentObjectGroupPython] I_element002  label="I_element : 0.648"  # scripted group (container) (typed FeaturePython)
  n = 0.647767
FEATURE [App::DocumentObjectGroupPython] G4_FREON_13I1  label="G4_FREON-13I1"  # scripted group (container) (typed FeaturePython)
  Dunit = g/cm3
  Dvalue = 1.8
  Group = -> [C_element047,F_element011,I_element002]
  conduct = 2
  density = 1
  expand = 3
  formula = G4_FREON-13I1
  name = G4_FREON-13I1
  specific = 4
FEATURE [App::DocumentObjectGroupPython] Gd_element001  label="Gd_element : 2"  # scripted group (container) (typed FeaturePython)
  n = 2
  ref = Gd_element
FEATURE [App::DocumentObjectGroupPython] O_element041  label="O_element : 021"  # scripted group (container) (typed FeaturePython)
  n = 2
  ref = O_element
FEATURE [App::DocumentObjectGroupPython] S_element012  label="S_element : 004"  # scripted group (container) (typed FeaturePython)
  n = 1
  ref = S_element
FEATURE [App::DocumentObjectGroupPython] G4_GADOLINIUM_OXYSULFIDE  # scripted group (container) (typed FeaturePython)
  Dunit = g/cm3
  Dvalue = 7.44
  Group = -> [Gd_element001,O_element041,S_element012]
  conduct = 2
  density = 1
  expand = 3
  formula = G4_GADOLINIUM_OXYSULFIDE
  name = G4_GADOLINIUM_OXYSULFIDE
  specific = 4
FEATURE [App::DocumentObjectGroupPython] Ga_element001  label="Ga_element : 1"  # scripted group (container) (typed FeaturePython)
  n = 1
  ref = Ga_element
FEATURE [App::DocumentObjectGroupPython] As_element001  label="As_element : 1"  # scripted group (container) (typed FeaturePython)
  n = 1
  ref = As_element
FEATURE [App::DocumentObjectGroupPython] G4_GALLIUM_ARSENIDE  # scripted group (container) (typed FeaturePython)
  Dunit = g/cm3
  Dvalue = 5.31
  Group = -> [Ga_element001,As_element001]
  conduct = 2
  density = 1
  expand = 3
  formula = G4_GALLIUM_ARSENIDE
  name = G4_GALLIUM_ARSENIDE
  specific = 4
FEATURE [App::DocumentObjectGroupPython] H_element041  label="H_element : 0.081"  # scripted group (container) (typed FeaturePython)
  n = 0.08118
FEATURE [App::DocumentObjectGroupPython] C_element048  label="C_element : 0.416"  # scripted group (container) (typed FeaturePython)
  n = 0.41606
FEATURE [App::DocumentObjectGroupPython] N_element018  label="N_element : 0.111"  # scripted group (container) (typed FeaturePython)
  n = 0.11124
FEATURE [App::DocumentObjectGroupPython] O_element042  label="O_element : 0.381"  # scripted group (container) (typed FeaturePython)
  n = 0.38064
FEATURE [App::DocumentObjectGroupPython] S_element013  label="S_element : 0.011"  # scripted group (container) (typed FeaturePython)
  n = 0.01088
FEATURE [App::DocumentObjectGroupPython] G4_GEL_PHOTO_EMULSION  # scripted group (container) (typed FeaturePython)
  Dunit = g/cm3
  Dvalue = 1.2914
  Group = -> [H_element041,C_element048,N_element018,O_element042,S_element013]
  conduct = 2
  density = 1
  expand = 3
  formula = G4_GEL_PHOTO_EMULSION
  name = G4_GEL_PHOTO_EMULSION
  specific = 4
FEATURE [App::DocumentObjectGroupPython] B_element004  label="B_element : 0.040"  # scripted group (container) (typed FeaturePython)
  n = 0.0400639
FEATURE [App::DocumentObjectGroupPython] O_element043  label="O_element : 0.540"  # scripted group (container) (typed FeaturePython)
  n = 0.539561
FEATURE [App::DocumentObjectGroupPython] Na_element008  label="Na_element : 0.028"  # scripted group (container) (typed FeaturePython)
  n = 0.0281909
FEATURE [App::DocumentObjectGroupPython] Al_element003  label="Al_element : 0.012"  # scripted group (container) (typed FeaturePython)
  n = 0.011644
FEATURE [App::DocumentObjectGroupPython] Si_element003  label="Si_element : 0.377"  # scripted group (container) (typed FeaturePython)
  n = 0.377219
FEATURE [App::DocumentObjectGroupPython] K_element004  label="K_element : 0.014"  # scripted group (container) (typed FeaturePython)
  n = 0.00332099
FEATURE [App::DocumentObjectGroupPython] G4_Pyrex_Glass  # scripted group (container) (typed FeaturePython)
  Dunit = g/cm3
  Dvalue = 2.23
  Group = -> [B_element004,O_element043,Na_element008,Al_element003,Si_element003,K_element004]
  conduct = 2
  density = 1
  expand = 3
  formula = G4_Pyrex_Glass
  name = G4_Pyrex_Glass
  specific = 4
FEATURE [App::DocumentObjectGroupPython] O_element044  label="O_element : 0.156"  # scripted group (container) (typed FeaturePython)
  n = 0.156453
FEATURE [App::DocumentObjectGroupPython] Si_element004  label="Si_element : 0.081"  # scripted group (container) (typed FeaturePython)
  n = 0.080866
FEATURE [App::DocumentObjectGroupPython] Ti_element001  label="Ti_element : 0.008"  # scripted group (container) (typed FeaturePython)
  n = 0.008092
FEATURE [App::DocumentObjectGroupPython] As_element002  label="As_element : 0.003"  # scripted group (container) (typed FeaturePython)
  n = 0.002651
FEATURE [App::DocumentObjectGroupPython] Pb_element001  label="Pb_element : 0.752"  # scripted group (container) (typed FeaturePython)
  n = 0.751938
FEATURE [App::DocumentObjectGroupPython] G4_GLASS_LEAD  # scripted group (container) (typed FeaturePython)
  Dunit = g/cm3
  Dvalue = 6.22
  Group = -> [O_element044,Si_element004,Ti_element001,As_element002,Pb_element001]
  conduct = 2
  density = 1
  expand = 3
  formula = G4_GLASS_LEAD
  name = G4_GLASS_LEAD
  specific = 4
FEATURE [App::DocumentObjectGroupPython] O_element045  label="O_element : 0.460"  # scripted group (container) (typed FeaturePython)
  n = 0.4598
FEATURE [App::DocumentObjectGroupPython] Na_element009  label="Na_element : 0.096"  # scripted group (container) (typed FeaturePython)
  n = 0.0964411
FEATURE [App::DocumentObjectGroupPython] Si_element005  label="Si_element : 0.378"  # scripted group (container) (typed FeaturePython)
  n = 0.336553
FEATURE [App::DocumentObjectGroupPython] Ca_element011  label="Ca_element : 0.107"  # scripted group (container) (typed FeaturePython)
  n = 0.107205
FEATURE [App::DocumentObjectGroupPython] G4_GLASS_PLATE  # scripted group (container) (typed FeaturePython)
  Dunit = g/cm3
  Dvalue = 2.4
  Group = -> [O_element045,Na_element009,Si_element005,Ca_element011]
  conduct = 2
  density = 1
  expand = 3
  formula = G4_GLASS_PLATE
  name = G4_GLASS_PLATE
  specific = 4
FEATURE [App::DocumentObjectGroupPython] C_element049  label="C_element : 026"  # scripted group (container) (typed FeaturePython)
  n = 5
  ref = C_element
FEATURE [App::DocumentObjectGroupPython] H_element042  label="H_element : 021"  # scripted group (container) (typed FeaturePython)
  n = 10
  ref = H_element
FEATURE [App::DocumentObjectGroupPython] N_element019  label="N_element : 2"  # scripted group (container) (typed FeaturePython)
  n = 2
  ref = N_element
FEATURE [App::DocumentObjectGroupPython] O_element046  label="O_element : 022"  # scripted group (container) (typed FeaturePython)
  n = 3
  ref = O_element
FEATURE [App::DocumentObjectGroupPython] G4_GLUTAMINE  # scripted group (container) (typed FeaturePython)
  Dunit = g/cm3
  Dvalue = 1.46
  Group = -> [C_element049,H_element042,N_element019,O_element046]
  conduct = 2
  density = 1
  expand = 3
  formula = G4_GLUTAMINE
  name = G4_GLUTAMINE
  specific = 4
FEATURE [App::DocumentObjectGroupPython] C_element050  label="C_element : 027"  # scripted group (container) (typed FeaturePython)
  n = 3
  ref = C_element
FEATURE [App::DocumentObjectGroupPython] H_element043  label="H_element : 022"  # scripted group (container) (typed FeaturePython)
  n = 8
  ref = H_element
FEATURE [App::DocumentObjectGroupPython] O_element047  label="O_element : 023"  # scripted group (container) (typed FeaturePython)
  n = 3
  ref = O_element
FEATURE [App::DocumentObjectGroupPython] G4_GLYCEROL  # scripted group (container) (typed FeaturePython)
  Dunit = g/cm3
  Dvalue = 1.2613
  Group = -> [C_element050,H_element043,O_element047]
  conduct = 2
  density = 1
  expand = 3
  formula = G4_GLYCEROL
  name = G4_GLYCEROL
  specific = 4
FEATURE [App::DocumentObjectGroupPython] C_element051  label="C_element : 028"  # scripted group (container) (typed FeaturePython)
  n = 5
  ref = C_element
FEATURE [App::DocumentObjectGroupPython] H_element044  label="H_element : 023"  # scripted group (container) (typed FeaturePython)
  n = 5
  ref = H_element
FEATURE [App::DocumentObjectGroupPython] N_element020  label="N_element : 009"  # scripted group (container) (typed FeaturePython)
  n = 5
  ref = N_element
FEATURE [App::DocumentObjectGroupPython] O_element048  label="O_element : 024"  # scripted group (container) (typed FeaturePython)
  n = 1
  ref = O_element
FEATURE [App::DocumentObjectGroupPython] G4_GUANINE  # scripted group (container) (typed FeaturePython)
  Dunit = g/cm3
  Dvalue = 2.2
  Group = -> [C_element051,H_element044,N_element020,O_element048]
  conduct = 2
  density = 1
  expand = 3
  formula = G4_GUANINE
  name = G4_GUANINE
  specific = 4
FEATURE [App::DocumentObjectGroupPython] Ca_element012  label="Ca_element : 006"  # scripted group (container) (typed FeaturePython)
  n = 1
  ref = Ca_element
FEATURE [App::DocumentObjectGroupPython] S_element014  label="S_element : 005"  # scripted group (container) (typed FeaturePython)
  n = 1
  ref = S_element
FEATURE [App::DocumentObjectGroupPython] O_element049  label="O_element : 6"  # scripted group (container) (typed FeaturePython)
  n = 6
  ref = O_element
FEATURE [App::DocumentObjectGroupPython] H_element045  label="H_element : 024"  # scripted group (container) (typed FeaturePython)
  n = 4
  ref = H_element
FEATURE [App::DocumentObjectGroupPython] G4_GYPSUM  # scripted group (container) (typed FeaturePython)
  Dunit = g/cm3
  Dvalue = 2.32
  Group = -> [Ca_element012,S_element014,O_element049,H_element045]
  conduct = 2
  density = 1
  expand = 3
  formula = G4_GYPSUM
  name = G4_GYPSUM
  specific = 4
FEATURE [App::DocumentObjectGroupPython] C_element052  label="C_element : 7"  # scripted group (container) (typed FeaturePython)
  n = 7
  ref = C_element
FEATURE [App::DocumentObjectGroupPython] H_element046  label="H_element : 16"  # scripted group (container) (typed FeaturePython)
  n = 16
  ref = H_element
FEATURE [App::DocumentObjectGroupPython] G4_N_HEPTANE  label="G4_N-HEPTANE"  # scripted group (container) (typed FeaturePython)
  Dunit = g/cm3
  Dvalue = 0.68376
  Group = -> [C_element052,H_element046]
  conduct = 2
  density = 1
  expand = 3
  formula = G4_N-HEPTANE
  name = G4_N-HEPTANE
  specific = 4
FEATURE [App::DocumentObjectGroupPython] C_element053  label="C_element : 029"  # scripted group (container) (typed FeaturePython)
  n = 6
  ref = C_element
FEATURE [App::DocumentObjectGroupPython] H_element047  label="H_element : 14"  # scripted group (container) (typed FeaturePython)
  n = 14
  ref = H_element
FEATURE [App::DocumentObjectGroupPython] G4_N_HEXANE  label="G4_N-HEXANE"  # scripted group (container) (typed FeaturePython)
  Dunit = g/cm3
  Dvalue = 0.6603
  Group = -> [C_element053,H_element047]
  conduct = 2
  density = 1
  expand = 3
  formula = G4_N-HEXANE
  name = G4_N-HEXANE
  specific = 4
FEATURE [App::DocumentObjectGroupPython] C_element054  label="C_element : 22"  # scripted group (container) (typed FeaturePython)
  n = 22
  ref = C_element
FEATURE [App::DocumentObjectGroupPython] H_element048  label="H_element : 025"  # scripted group (container) (typed FeaturePython)
  n = 10
  ref = H_element
FEATURE [App::DocumentObjectGroupPython] N_element021  label="N_element : 010"  # scripted group (container) (typed FeaturePython)
  n = 2
  ref = N_element
FEATURE [App::DocumentObjectGroupPython] O_element050  label="O_element : 025"  # scripted group (container) (typed FeaturePython)
  n = 5
  ref = O_element
FEATURE [App::DocumentObjectGroupPython] G4_KAPTON  # scripted group (container) (typed FeaturePython)
  Dunit = g/cm3
  Dvalue = 1.42
  Group = -> [C_element054,H_element048,N_element021,O_element050]
  conduct = 2
  density = 1
  expand = 3
  formula = G4_KAPTON
  name = G4_KAPTON
  specific = 4
FEATURE [App::DocumentObjectGroupPython] La_element001  label="La_element : 1"  # scripted group (container) (typed FeaturePython)
  n = 1
  ref = La_element
FEATURE [App::DocumentObjectGroupPython] Br_element003  label="Br_element : 002"  # scripted group (container) (typed FeaturePython)
  n = 1
  ref = Br_element
FEATURE [App::DocumentObjectGroupPython] O_element051  label="O_element : 026"  # scripted group (container) (typed FeaturePython)
  n = 1
  ref = O_element
FEATURE [App::DocumentObjectGroupPython] G4_LANTHANUM_OXYBROMIDE  # scripted group (container) (typed FeaturePython)
  Dunit = g/cm3
  Dvalue = 6.28
  Group = -> [La_element001,Br_element003,O_element051]
  conduct = 2
  density = 1
  expand = 3
  formula = G4_LANTHANUM_OXYBROMIDE
  name = G4_LANTHANUM_OXYBROMIDE
  specific = 4
FEATURE [App::DocumentObjectGroupPython] La_element002  label="La_element : 2"  # scripted group (container) (typed FeaturePython)
  n = 2
  ref = La_element
FEATURE [App::DocumentObjectGroupPython] O_element052  label="O_element : 027"  # scripted group (container) (typed FeaturePython)
  n = 2
  ref = O_element
FEATURE [App::DocumentObjectGroupPython] S_element015  label="S_element : 006"  # scripted group (container) (typed FeaturePython)
  n = 1
  ref = S_element
FEATURE [App::DocumentObjectGroupPython] G4_LANTHANUM_OXYSULFIDE  # scripted group (container) (typed FeaturePython)
  Dunit = g/cm3
  Dvalue = 5.86
  Group = -> [La_element002,O_element052,S_element015]
  conduct = 2
  density = 1
  expand = 3
  formula = G4_LANTHANUM_OXYSULFIDE
  name = G4_LANTHANUM_OXYSULFIDE
  specific = 4
FEATURE [App::DocumentObjectGroupPython] O_element053  label="O_element : 0.072"  # scripted group (container) (typed FeaturePython)
  n = 0.071682
FEATURE [App::DocumentObjectGroupPython] Pb_element002  label="Pb_element : 0.928"  # scripted group (container) (typed FeaturePython)
  n = 0.928318
FEATURE [App::DocumentObjectGroupPython] G4_LEAD_OXIDE  # scripted group (container) (typed FeaturePython)
  Dunit = g/cm3
  Dvalue = 9.53
  Group = -> [O_element053,Pb_element002]
  conduct = 2
  density = 1
  expand = 3
  formula = G4_LEAD_OXIDE
  name = G4_LEAD_OXIDE
  specific = 4
FEATURE [App::DocumentObjectGroupPython] Li_element001  label="Li_element : 1"  # scripted group (container) (typed FeaturePython)
  n = 1
  ref = Li_element
FEATURE [App::DocumentObjectGroupPython] N_element022  label="N_element : 011"  # scripted group (container) (typed FeaturePython)
  n = 1
  ref = N_element
FEATURE [App::DocumentObjectGroupPython] H_element049  label="H_element : 026"  # scripted group (container) (typed FeaturePython)
  n = 2
  ref = H_element
FEATURE [App::DocumentObjectGroupPython] G4_LITHIUM_AMIDE  # scripted group (container) (typed FeaturePython)
  Dunit = g/cm3
  Dvalue = 1.178
  Group = -> [Li_element001,N_element022,H_element049]
  conduct = 2
  density = 1
  expand = 3
  formula = G4_LITHIUM_AMIDE
  name = G4_LITHIUM_AMIDE
  specific = 4
FEATURE [App::DocumentObjectGroupPython] Li_element002  label="Li_element : 2"  # scripted group (container) (typed FeaturePython)
  n = 2
  ref = Li_element
FEATURE [App::DocumentObjectGroupPython] C_element055  label="C_element : 030"  # scripted group (container) (typed FeaturePython)
  n = 1
  ref = C_element
FEATURE [App::DocumentObjectGroupPython] O_element054  label="O_element : 028"  # scripted group (container) (typed FeaturePython)
  n = 3
  ref = O_element
FEATURE [App::DocumentObjectGroupPython] G4_LITHIUM_CARBONATE  # scripted group (container) (typed FeaturePython)
  Dunit = g/cm3
  Dvalue = 2.11
  Group = -> [Li_element002,C_element055,O_element054]
  conduct = 2
  density = 1
  expand = 3
  formula = G4_LITHIUM_CARBONATE
  name = G4_LITHIUM_CARBONATE
  specific = 4
FEATURE [App::DocumentObjectGroupPython] Li_element003  label="Li_element : 003"  # scripted group (container) (typed FeaturePython)
  n = 1
  ref = Li_element
FEATURE [App::DocumentObjectGroupPython] F_element012  label="F_element : 004"  # scripted group (container) (typed FeaturePython)
  n = 1
  ref = F_element
FEATURE [App::DocumentObjectGroupPython] G4_LITHIUM_FLUORIDE  # scripted group (container) (typed FeaturePython)
  Dunit = g/cm3
  Dvalue = 2.635
  Group = -> [Li_element003,F_element012]
  conduct = 2
  density = 1
  expand = 3
  formula = G4_LITHIUM_FLUORIDE
  name = G4_LITHIUM_FLUORIDE
  specific = 4
FEATURE [App::DocumentObjectGroupPython] Li_element004  label="Li_element : 004"  # scripted group (container) (typed FeaturePython)
  n = 1
  ref = Li_element
FEATURE [App::DocumentObjectGroupPython] H_element050  label="H_element : 027"  # scripted group (container) (typed FeaturePython)
  n = 1
  ref = H_element
FEATURE [App::DocumentObjectGroupPython] G4_LITHIUM_HYDRIDE  # scripted group (container) (typed FeaturePython)
  Dunit = g/cm3
  Dvalue = 0.82
  Group = -> [Li_element004,H_element050]
  conduct = 2
  density = 1
  expand = 3
  formula = G4_LITHIUM_HYDRIDE
  name = G4_LITHIUM_HYDRIDE
  specific = 4
FEATURE [App::DocumentObjectGroupPython] Li_element005  label="Li_element : 005"  # scripted group (container) (typed FeaturePython)
  n = 1
  ref = Li_element
FEATURE [App::DocumentObjectGroupPython] I_element003  label="I_element : 002"  # scripted group (container) (typed FeaturePython)
  n = 1
  ref = I_element
FEATURE [App::DocumentObjectGroupPython] G4_LITHIUM_IODIDE  # scripted group (container) (typed FeaturePython)
  Dunit = g/cm3
  Dvalue = 3.494
  Group = -> [Li_element005,I_element003]
  conduct = 2
  density = 1
  expand = 3
  formula = G4_LITHIUM_IODIDE
  name = G4_LITHIUM_IODIDE
  specific = 4
FEATURE [App::DocumentObjectGroupPython] Li_element006  label="Li_element : 006"  # scripted group (container) (typed FeaturePython)
  n = 2
  ref = Li_element
FEATURE [App::DocumentObjectGroupPython] O_element055  label="O_element : 029"  # scripted group (container) (typed FeaturePython)
  n = 1
  ref = O_element
FEATURE [App::DocumentObjectGroupPython] G4_LITHIUM_OXIDE  # scripted group (container) (typed FeaturePython)
  Dunit = g/cm3
  Dvalue = 2.013
  Group = -> [Li_element006,O_element055]
  conduct = 2
  density = 1
  expand = 3
  formula = G4_LITHIUM_OXIDE
  name = G4_LITHIUM_OXIDE
  specific = 4
FEATURE [App::DocumentObjectGroupPython] Li_element007  label="Li_element : 007"  # scripted group (container) (typed FeaturePython)
  n = 2
  ref = Li_element
FEATURE [App::DocumentObjectGroupPython] B_element005  label="B_element : 005"  # scripted group (container) (typed FeaturePython)
  n = 4
  ref = B_element
FEATURE [App::DocumentObjectGroupPython] O_element056  label="O_element : 7"  # scripted group (container) (typed FeaturePython)
  n = 7
  ref = O_element
FEATURE [App::DocumentObjectGroupPython] G4_LITHIUM_TETRABORATE  # scripted group (container) (typed FeaturePython)
  Dunit = g/cm3
  Dvalue = 2.44
  Group = -> [Li_element007,B_element005,O_element056]
  conduct = 2
  density = 1
  expand = 3
  formula = G4_LITHIUM_TETRABORATE
  name = G4_LITHIUM_TETRABORATE
  specific = 4
FEATURE [App::DocumentObjectGroupPython] H_element051  label="H_element : 0.105"  # scripted group (container) (typed FeaturePython)
  n = 0.105
FEATURE [App::DocumentObjectGroupPython] C_element056  label="C_element : 0.083"  # scripted group (container) (typed FeaturePython)
  n = 0.083
FEATURE [App::DocumentObjectGroupPython] N_element023  label="N_element : 0.023"  # scripted group (container) (typed FeaturePython)
  n = 0.023
FEATURE [App::DocumentObjectGroupPython] O_element057  label="O_element : 0.779"  # scripted group (container) (typed FeaturePython)
  n = 0.779
FEATURE [App::DocumentObjectGroupPython] Na_element010  label="Na_element : 0.097"  # scripted group (container) (typed FeaturePython)
  n = 0.002
FEATURE [App::DocumentObjectGroupPython] P_element006  label="P_element : 0.105"  # scripted group (container) (typed FeaturePython)
  n = 0.001
FEATURE [App::DocumentObjectGroupPython] S_element016  label="S_element : 0.017"  # scripted group (container) (typed FeaturePython)
  n = 0.002
FEATURE [App::DocumentObjectGroupPython] Cl_element014  label="Cl_element : 0.587"  # scripted group (container) (typed FeaturePython)
  n = 0.003
FEATURE [App::DocumentObjectGroupPython] K_element005  label="K_element : 0.015"  # scripted group (container) (typed FeaturePython)
  n = 0.002
FEATURE [App::DocumentObjectGroupPython] G4_LUNG_ICRP  # scripted group (container) (typed FeaturePython)
  Dunit = g/cm3
  Dvalue = 1.04
  Group = -> [H_element051,C_element056,N_element023,O_element057,Na_element010,P_element006,S_element016,Cl_element014,K_element005]
  conduct = 2
  density = 1
  expand = 3
  formula = G4_LUNG_ICRP
  name = G4_LUNG_ICRP
  specific = 4
FEATURE [App::DocumentObjectGroupPython] H_element052  label="H_element : 0.116"  # scripted group (container) (typed FeaturePython)
  n = 0.114318
FEATURE [App::DocumentObjectGroupPython] C_element057  label="C_element : 0.656"  # scripted group (container) (typed FeaturePython)
  n = 0.655824
FEATURE [App::DocumentObjectGroupPython] O_element058  label="O_element : 0.092"  # scripted group (container) (typed FeaturePython)
  n = 0.0921831
FEATURE [App::DocumentObjectGroupPython] Mg_element004  label="Mg_element : 0.135"  # scripted group (container) (typed FeaturePython)
  n = 0.134792
FEATURE [App::DocumentObjectGroupPython] Ca_element013  label="Ca_element : 0.003"  # scripted group (container) (typed FeaturePython)
  n = 0.002883
FEATURE [App::DocumentObjectGroupPython] G4_M3_WAX  # scripted group (container) (typed FeaturePython)
  Dunit = g/cm3
  Dvalue = 1.05
  Group = -> [H_element052,C_element057,O_element058,Mg_element004,Ca_element013]
  conduct = 2
  density = 1
  expand = 3
  formula = G4_M3_WAX
  name = G4_M3_WAX
  specific = 4
FEATURE [App::DocumentObjectGroupPython] Mg_element005  label="Mg_element : 1"  # scripted group (container) (typed FeaturePython)
  n = 1
  ref = Mg_element
FEATURE [App::DocumentObjectGroupPython] C_element058  label="C_element : 031"  # scripted group (container) (typed FeaturePython)
  n = 1
  ref = C_element
FEATURE [App::DocumentObjectGroupPython] O_element059  label="O_element : 030"  # scripted group (container) (typed FeaturePython)
  n = 3
  ref = O_element
FEATURE [App::DocumentObjectGroupPython] G4_MAGNESIUM_CARBONATE  # scripted group (container) (typed FeaturePython)
  Dunit = g/cm3
  Dvalue = 2.958
  Group = -> [Mg_element005,C_element058,O_element059]
  conduct = 2
  density = 1
  expand = 3
  formula = G4_MAGNESIUM_CARBONATE
  name = G4_MAGNESIUM_CARBONATE
  specific = 4
FEATURE [App::DocumentObjectGroupPython] Mg_element006  label="Mg_element : 002"  # scripted group (container) (typed FeaturePython)
  n = 1
  ref = Mg_element
FEATURE [App::DocumentObjectGroupPython] F_element013  label="F_element : 005"  # scripted group (container) (typed FeaturePython)
  n = 2
  ref = F_element
FEATURE [App::DocumentObjectGroupPython] G4_MAGNESIUM_FLUORIDE  # scripted group (container) (typed FeaturePython)
  Dunit = g/cm3
  Dvalue = 3
  Group = -> [Mg_element006,F_element013]
  conduct = 2
  density = 1
  expand = 3
  formula = G4_MAGNESIUM_FLUORIDE
  name = G4_MAGNESIUM_FLUORIDE
  specific = 4
FEATURE [App::DocumentObjectGroupPython] Mg_element007  label="Mg_element : 003"  # scripted group (container) (typed FeaturePython)
  n = 1
  ref = Mg_element
FEATURE [App::DocumentObjectGroupPython] O_element060  label="O_element : 031"  # scripted group (container) (typed FeaturePython)
  n = 1
  ref = O_element
FEATURE [App::DocumentObjectGroupPython] G4_MAGNESIUM_OXIDE  # scripted group (container) (typed FeaturePython)
  Dunit = g/cm3
  Dvalue = 3.58
  Group = -> [Mg_element007,O_element060]
  conduct = 2
  density = 1
  expand = 3
  formula = G4_MAGNESIUM_OXIDE
  name = G4_MAGNESIUM_OXIDE
  specific = 4
FEATURE [App::DocumentObjectGroupPython] Mg_element008  label="Mg_element : 004"  # scripted group (container) (typed FeaturePython)
  n = 1
  ref = Mg_element
FEATURE [App::DocumentObjectGroupPython] B_element006  label="B_element : 006"  # scripted group (container) (typed FeaturePython)
  n = 4
  ref = B_element
FEATURE [App::DocumentObjectGroupPython] O_element061  label="O_element : 032"  # scripted group (container) (typed FeaturePython)
  n = 7
  ref = O_element
FEATURE [App::DocumentObjectGroupPython] G4_MAGNESIUM_TETRABORATE  # scripted group (container) (typed FeaturePython)
  Dunit = g/cm3
  Dvalue = 2.53
  Group = -> [Mg_element008,B_element006,O_element061]
  conduct = 2
  density = 1
  expand = 3
  formula = G4_MAGNESIUM_TETRABORATE
  name = G4_MAGNESIUM_TETRABORATE
  specific = 4
FEATURE [App::DocumentObjectGroupPython] Hg_element001  label="Hg_element : 1"  # scripted group (container) (typed FeaturePython)
  n = 1
  ref = Hg_element
FEATURE [App::DocumentObjectGroupPython] I_element004  label="I_element : 2"  # scripted group (container) (typed FeaturePython)
  n = 2
  ref = I_element
FEATURE [App::DocumentObjectGroupPython] G4_MERCURIC_IODIDE  # scripted group (container) (typed FeaturePython)
  Dunit = g/cm3
  Dvalue = 6.36
  Group = -> [Hg_element001,I_element004]
  conduct = 2
  density = 1
  expand = 3
  formula = G4_MERCURIC_IODIDE
  name = G4_MERCURIC_IODIDE
  specific = 4
FEATURE [App::DocumentObjectGroupPython] C_element059  label="C_element : 032"  # scripted group (container) (typed FeaturePython)
  n = 1
  ref = C_element
FEATURE [App::DocumentObjectGroupPython] H_element053  label="H_element : 028"  # scripted group (container) (typed FeaturePython)
  n = 4
  ref = H_element
FEATURE [App::DocumentObjectGroupPython] G4_METHANE  # scripted group (container) (typed FeaturePython)
  Dunit = g/cm3
  Dvalue = 0.000667151
  Group = -> [C_element059,H_element053]
  conduct = 2
  density = 1
  expand = 3
  formula = G4_METHANE
  name = G4_METHANE
  specific = 4
FEATURE [App::DocumentObjectGroupPython] C_element060  label="C_element : 033"  # scripted group (container) (typed FeaturePython)
  n = 1
  ref = C_element
FEATURE [App::DocumentObjectGroupPython] H_element054  label="H_element : 029"  # scripted group (container) (typed FeaturePython)
  n = 4
  ref = H_element
FEATURE [App::DocumentObjectGroupPython] O_element062  label="O_element : 033"  # scripted group (container) (typed FeaturePython)
  n = 1
  ref = O_element
FEATURE [App::DocumentObjectGroupPython] G4_METHANOL  # scripted group (container) (typed FeaturePython)
  Dunit = g/cm3
  Dvalue = 0.7914
  Group = -> [C_element060,H_element054,O_element062]
  conduct = 2
  density = 1
  expand = 3
  formula = G4_METHANOL
  name = G4_METHANOL
  specific = 4
FEATURE [App::DocumentObjectGroupPython] H_element055  label="H_element : 0.134"  # scripted group (container) (typed FeaturePython)
  n = 0.13404
FEATURE [App::DocumentObjectGroupPython] C_element061  label="C_element : 0.778"  # scripted group (container) (typed FeaturePython)
  n = 0.77796
FEATURE [App::DocumentObjectGroupPython] O_element063  label="O_element : 0.035"  # scripted group (container) (typed FeaturePython)
  n = 0.03502
FEATURE [App::DocumentObjectGroupPython] Mg_element009  label="Mg_element : 0.039"  # scripted group (container) (typed FeaturePython)
  n = 0.038594
FEATURE [App::DocumentObjectGroupPython] Ti_element002  label="Ti_element : 0.014"  # scripted group (container) (typed FeaturePython)
  n = 0.014386
FEATURE [App::DocumentObjectGroupPython] G4_MIX_D_WAX  # scripted group (container) (typed FeaturePython)
  Dunit = g/cm3
  Dvalue = 0.99
  Group = -> [H_element055,C_element061,O_element063,Mg_element009,Ti_element002]
  conduct = 2
  density = 1
  expand = 3
  formula = G4_MIX_D_WAX
  name = G4_MIX_D_WAX
  specific = 4
FEATURE [App::DocumentObjectGroupPython] H_element056  label="H_element : 0.135"  # scripted group (container) (typed FeaturePython)
  n = 0.081192
FEATURE [App::DocumentObjectGroupPython] C_element062  label="C_element : 0.583"  # scripted group (container) (typed FeaturePython)
  n = 0.583442
FEATURE [App::DocumentObjectGroupPython] N_element024  label="N_element : 0.018"  # scripted group (container) (typed FeaturePython)
  n = 0.017798
FEATURE [App::DocumentObjectGroupPython] O_element064  label="O_element : 0.186"  # scripted group (container) (typed FeaturePython)
  n = 0.186381
FEATURE [App::DocumentObjectGroupPython] Mg_element010  label="Mg_element : 0.130"  # scripted group (container) (typed FeaturePython)
  n = 0.130287
FEATURE [App::DocumentObjectGroupPython] Cl_element015  label="Cl_element : 0.588"  # scripted group (container) (typed FeaturePython)
  n = 0.0009
FEATURE [App::DocumentObjectGroupPython] G4_MS20_TISSUE  # scripted group (container) (typed FeaturePython)
  Dunit = g/cm3
  Dvalue = 1
  Group = -> [H_element056,C_element062,N_element024,O_element064,Mg_element010,Cl_element015]
  conduct = 2
  density = 1
  expand = 3
  formula = G4_MS20_TISSUE
  name = G4_MS20_TISSUE
  specific = 4
FEATURE [App::DocumentObjectGroupPython] H_element057  label="H_element : 0.136"  # scripted group (container) (typed FeaturePython)
  n = 0.102
FEATURE [App::DocumentObjectGroupPython] C_element063  label="C_element : 0.143"  # scripted group (container) (typed FeaturePython)
  n = 0.143
FEATURE [App::DocumentObjectGroupPython] N_element025  label="N_element : 0.034"  # scripted group (container) (typed FeaturePython)
  n = 0.034
FEATURE [App::DocumentObjectGroupPython] O_element065  label="O_element : 0.710"  # scripted group (container) (typed FeaturePython)
  n = 0.71
FEATURE [App::DocumentObjectGroupPython] Na_element011  label="Na_element : 0.098"  # scripted group (container) (typed FeaturePython)
  n = 0.001
FEATURE [App::DocumentObjectGroupPython] P_element007  label="P_element : 0.002"  # scripted group (container) (typed FeaturePython)
  n = 0.002
FEATURE [App::DocumentObjectGroupPython] S_element017  label="S_element : 0.018"  # scripted group (container) (typed FeaturePython)
  n = 0.003
FEATURE [App::DocumentObjectGroupPython] Cl_element016  label="Cl_element : 0.589"  # scripted group (container) (typed FeaturePython)
  n = 0.001
FEATURE [App::DocumentObjectGroupPython] K_element006  label="K_element : 0.004"  # scripted group (container) (typed FeaturePython)
  n = 0.004
FEATURE [App::DocumentObjectGroupPython] G4_MUSCLE_SKELETAL_ICRP  # scripted group (container) (typed FeaturePython)
  Dunit = g/cm3
  Dvalue = 1.05
  Group = -> [H_element057,C_element063,N_element025,O_element065,Na_element011,P_element007,S_element017,Cl_element016,K_element006]
  conduct = 2
  density = 1
  expand = 3
  formula = G4_MUSCLE_SKELETAL_ICRP
  name = G4_MUSCLE_SKELETAL_ICRP
  specific = 4
FEATURE [App::DocumentObjectGroupPython] H_element058  label="H_element : 0.137"  # scripted group (container) (typed FeaturePython)
  n = 0.102102
FEATURE [App::DocumentObjectGroupPython] C_element064  label="C_element : 0.123"  # scripted group (container) (typed FeaturePython)
  n = 0.123123
FEATURE [App::DocumentObjectGroupPython] N_element026  label="N_element : 0.756"  # scripted group (container) (typed FeaturePython)
  n = 0.035035
FEATURE [App::DocumentObjectGroupPython] O_element066  label="O_element : 0.730"  # scripted group (container) (typed FeaturePython)
  n = 0.72973
FEATURE [App::DocumentObjectGroupPython] Na_element012  label="Na_element : 0.099"  # scripted group (container) (typed FeaturePython)
  n = 0.001001
FEATURE [App::DocumentObjectGroupPython] P_element008  label="P_element : 0.106"  # scripted group (container) (typed FeaturePython)
  n = 0.002002
FEATURE [App::DocumentObjectGroupPython] S_element018  label="S_element : 0.019"  # scripted group (container) (typed FeaturePython)
  n = 0.004004
FEATURE [App::DocumentObjectGroupPython] K_element007  label="K_element : 0.016"  # scripted group (container) (typed FeaturePython)
  n = 0.003003
FEATURE [App::DocumentObjectGroupPython] G4_MUSCLE_STRIATED_ICRU  # scripted group (container) (typed FeaturePython)
  Dunit = g/cm3
  Dvalue = 1.04
  Group = -> [H_element058,C_element064,N_element026,O_element066,Na_element012,P_element008,S_element018,K_element007]
  conduct = 2
  density = 1
  expand = 3
  formula = G4_MUSCLE_STRIATED_ICRU
  name = G4_MUSCLE_STRIATED_ICRU
  specific = 4
FEATURE [App::DocumentObjectGroupPython] H_element059  label="H_element : 0.098"  # scripted group (container) (typed FeaturePython)
  n = 0.0982341
FEATURE [App::DocumentObjectGroupPython] C_element065  label="C_element : 0.156"  # scripted group (container) (typed FeaturePython)
  n = 0.156214
FEATURE [App::DocumentObjectGroupPython] N_element027  label="N_element : 0.757"  # scripted group (container) (typed FeaturePython)
  n = 0.035451
FEATURE [App::DocumentObjectGroupPython] O_element067  label="O_element : 0.880"  # scripted group (container) (typed FeaturePython)
  n = 0.710101
FEATURE [App::DocumentObjectGroupPython] G4_MUSCLE_WITH_SUCROSE  # scripted group (container) (typed FeaturePython)
  Dunit = g/cm3
  Dvalue = 1.11
  Group = -> [H_element059,C_element065,N_element027,O_element067]
  conduct = 2
  density = 1
  expand = 3
  formula = G4_MUSCLE_WITH_SUCROSE
  name = G4_MUSCLE_WITH_SUCROSE
  specific = 4
FEATURE [App::DocumentObjectGroupPython] H_element060  label="H_element : 0.138"  # scripted group (container) (typed FeaturePython)
  n = 0.101969
FEATURE [App::DocumentObjectGroupPython] C_element066  label="C_element : 0.120"  # scripted group (container) (typed FeaturePython)
  n = 0.120058
FEATURE [App::DocumentObjectGroupPython] N_element028  label="N_element : 0.758"  # scripted group (container) (typed FeaturePython)
  n = 0.035451
FEATURE [App::DocumentObjectGroupPython] O_element068  label="O_element : 0.743"  # scripted group (container) (typed FeaturePython)
  n = 0.742522
FEATURE [App::DocumentObjectGroupPython] G4_MUSCLE_WITHOUT_SUCROSE  # scripted group (container) (typed FeaturePython)
  Dunit = g/cm3
  Dvalue = 1.07
  Group = -> [H_element060,C_element066,N_element028,O_element068]
  conduct = 2
  density = 1
  expand = 3
  formula = G4_MUSCLE_WITHOUT_SUCROSE
  name = G4_MUSCLE_WITHOUT_SUCROSE
  specific = 4
FEATURE [App::DocumentObjectGroupPython] C_element067  label="C_element : 10"  # scripted group (container) (typed FeaturePython)
  n = 10
  ref = C_element
FEATURE [App::DocumentObjectGroupPython] H_element061  label="H_element : 030"  # scripted group (container) (typed FeaturePython)
  n = 8
  ref = H_element
FEATURE [App::DocumentObjectGroupPython] G4_NAPHTHALENE  # scripted group (container) (typed FeaturePython)
  Dunit = g/cm3
  Dvalue = 1.145
  Group = -> [C_element067,H_element061]
  conduct = 2
  density = 1
  expand = 3
  formula = G4_NAPHTHALENE
  name = G4_NAPHTHALENE
  specific = 4
FEATURE [App::DocumentObjectGroupPython] C_element068  label="C_element : 034"  # scripted group (container) (typed FeaturePython)
  n = 6
  ref = C_element
FEATURE [App::DocumentObjectGroupPython] H_element062  label="H_element : 031"  # scripted group (container) (typed FeaturePython)
  n = 5
  ref = H_element
FEATURE [App::DocumentObjectGroupPython] N_element029  label="N_element : 012"  # scripted group (container) (typed FeaturePython)
  n = 1
  ref = N_element
FEATURE [App::DocumentObjectGroupPython] O_element069  label="O_element : 034"  # scripted group (container) (typed FeaturePython)
  n = 2
  ref = O_element
FEATURE [App::DocumentObjectGroupPython] G4_NITROBENZENE  # scripted group (container) (typed FeaturePython)
  Dunit = g/cm3
  Dvalue = 1.19867
  Group = -> [C_element068,H_element062,N_element029,O_element069]
  conduct = 2
  density = 1
  expand = 3
  formula = G4_NITROBENZENE
  name = G4_NITROBENZENE
  specific = 4
FEATURE [App::DocumentObjectGroupPython] N_element030  label="N_element : 013"  # scripted group (container) (typed FeaturePython)
  n = 2
  ref = N_element
FEATURE [App::DocumentObjectGroupPython] O_element070  label="O_element : 035"  # scripted group (container) (typed FeaturePython)
  n = 1
  ref = O_element
FEATURE [App::DocumentObjectGroupPython] G4_NITROUS_OXIDE  # scripted group (container) (typed FeaturePython)
  Dunit = g/cm3
  Dvalue = 0.00183094
  Group = -> [N_element030,O_element070]
  conduct = 2
  density = 1
  expand = 3
  formula = G4_NITROUS_OXIDE
  name = G4_NITROUS_OXIDE
  specific = 4
FEATURE [App::DocumentObjectGroupPython] H_element063  label="H_element : 0.104"  # scripted group (container) (typed FeaturePython)
  n = 0.103509
FEATURE [App::DocumentObjectGroupPython] C_element069  label="C_element : 0.648"  # scripted group (container) (typed FeaturePython)
  n = 0.648416
FEATURE [App::DocumentObjectGroupPython] N_element031  label="N_element : 0.100"  # scripted group (container) (typed FeaturePython)
  n = 0.0995361
FEATURE [App::DocumentObjectGroupPython] O_element071  label="O_element : 0.149"  # scripted group (container) (typed FeaturePython)
  n = 0.148539
FEATURE [App::DocumentObjectGroupPython] G4_NYLON_8062  label="G4_NYLON-8062"  # scripted group (container) (typed FeaturePython)
  Dunit = g/cm3
  Dvalue = 1.08
  Group = -> [H_element063,C_element069,N_element031,O_element071]
  conduct = 2
  density = 1
  expand = 3
  formula = G4_NYLON-8062
  name = G4_NYLON-8062
  specific = 4
FEATURE [App::DocumentObjectGroupPython] C_element070  label="C_element : 035"  # scripted group (container) (typed FeaturePython)
  n = 6
  ref = C_element
FEATURE [App::DocumentObjectGroupPython] H_element064  label="H_element : 11"  # scripted group (container) (typed FeaturePython)
  n = 11
  ref = H_element
FEATURE [App::DocumentObjectGroupPython] N_element032  label="N_element : 014"  # scripted group (container) (typed FeaturePython)
  n = 1
  ref = N_element
FEATURE [App::DocumentObjectGroupPython] O_element072  label="O_element : 036"  # scripted group (container) (typed FeaturePython)
  n = 1
  ref = O_element
FEATURE [App::DocumentObjectGroupPython] G4_NYLON_6_6  label="G4_NYLON-6-6"  # scripted group (container) (typed FeaturePython)
  Dunit = g/cm3
  Dvalue = 1.14
  Group = -> [C_element070,H_element064,N_element032,O_element072]
  conduct = 2
  density = 1
  expand = 3
  formula = G4_NYLON-6-6
  name = G4_NYLON-6-6
  specific = 4
FEATURE [App::DocumentObjectGroupPython] H_element065  label="H_element : 0.139"  # scripted group (container) (typed FeaturePython)
  n = 0.107062
FEATURE [App::DocumentObjectGroupPython] C_element071  label="C_element : 0.680"  # scripted group (container) (typed FeaturePython)
  n = 0.680449
FEATURE [App::DocumentObjectGroupPython] N_element033  label="N_element : 0.099"  # scripted group (container) (typed FeaturePython)
  n = 0.099189
FEATURE [App::DocumentObjectGroupPython] O_element073  label="O_element : 0.113"  # scripted group (container) (typed FeaturePython)
  n = 0.1133
FEATURE [App::DocumentObjectGroupPython] G4_NYLON_6_10  label="G4_NYLON-6-10"  # scripted group (container) (typed FeaturePython)
  Dunit = g/cm3
  Dvalue = 1.14
  Group = -> [H_element065,C_element071,N_element033,O_element073]
  conduct = 2
  density = 1
  expand = 3
  formula = G4_NYLON-6-10
  name = G4_NYLON-6-10
  specific = 4
FEATURE [App::DocumentObjectGroupPython] H_element066  label="H_element : 0.140"  # scripted group (container) (typed FeaturePython)
  n = 0.115476
FEATURE [App::DocumentObjectGroupPython] C_element072  label="C_element : 0.721"  # scripted group (container) (typed FeaturePython)
  n = 0.720818
FEATURE [App::DocumentObjectGroupPython] N_element034  label="N_element : 0.076"  # scripted group (container) (typed FeaturePython)
  n = 0.0764169
FEATURE [App::DocumentObjectGroupPython] O_element074  label="O_element : 0.087"  # scripted group (container) (typed FeaturePython)
  n = 0.0872889
FEATURE [App::DocumentObjectGroupPython] G4_NYLON_11_RILSAN  label="G4_NYLON-11_RILSAN"  # scripted group (container) (typed FeaturePython)
  Dunit = g/cm3
  Dvalue = 1.425
  Group = -> [H_element066,C_element072,N_element034,O_element074]
  conduct = 2
  density = 1
  expand = 3
  formula = G4_NYLON-11_RILSAN
  name = G4_NYLON-11_RILSAN
  specific = 4
FEATURE [App::DocumentObjectGroupPython] C_element073  label="C_element : 8"  # scripted group (container) (typed FeaturePython)
  n = 8
  ref = C_element
FEATURE [App::DocumentObjectGroupPython] H_element067  label="H_element : 18"  # scripted group (container) (typed FeaturePython)
  n = 18
  ref = H_element
FEATURE [App::DocumentObjectGroupPython] G4_OCTANE  # scripted group (container) (typed FeaturePython)
  Dunit = g/cm3
  Dvalue = 0.7026
  Group = -> [C_element073,H_element067]
  conduct = 2
  density = 1
  expand = 3
  formula = G4_OCTANE
  name = G4_OCTANE
  specific = 4
FEATURE [App::DocumentObjectGroupPython] C_element074  label="C_element : 25"  # scripted group (container) (typed FeaturePython)
  n = 25
  ref = C_element
FEATURE [App::DocumentObjectGroupPython] H_element068  label="H_element : 52"  # scripted group (container) (typed FeaturePython)
  n = 52
  ref = H_element
FEATURE [App::DocumentObjectGroupPython] G4_PARAFFIN  # scripted group (container) (typed FeaturePython)
  Dunit = g/cm3
  Dvalue = 0.93
  Group = -> [C_element074,H_element068]
  conduct = 2
  density = 1
  expand = 3
  formula = G4_PARAFFIN
  name = G4_PARAFFIN
  specific = 4
FEATURE [App::DocumentObjectGroupPython] C_element075  label="C_element : 036"  # scripted group (container) (typed FeaturePython)
  n = 5
  ref = C_element
FEATURE [App::DocumentObjectGroupPython] H_element069  label="H_element : 032"  # scripted group (container) (typed FeaturePython)
  n = 12
  ref = H_element
FEATURE [App::DocumentObjectGroupPython] G4_N_PENTANE  label="G4_N-PENTANE"  # scripted group (container) (typed FeaturePython)
  Dunit = g/cm3
  Dvalue = 0.6262
  Group = -> [C_element075,H_element069]
  conduct = 2
  density = 1
  expand = 3
  formula = G4_N-PENTANE
  name = G4_N-PENTANE
  specific = 4
FEATURE [App::DocumentObjectGroupPython] H_element070  label="H_element : 0.014"  # scripted group (container) (typed FeaturePython)
  n = 0.0141
FEATURE [App::DocumentObjectGroupPython] C_element076  label="C_element : 0.072"  # scripted group (container) (typed FeaturePython)
  n = 0.072261
FEATURE [App::DocumentObjectGroupPython] N_element035  label="N_element : 0.019"  # scripted group (container) (typed FeaturePython)
  n = 0.01932
FEATURE [App::DocumentObjectGroupPython] O_element075  label="O_element : 0.066"  # scripted group (container) (typed FeaturePython)
  n = 0.066101
FEATURE [App::DocumentObjectGroupPython] S_element019  label="S_element : 0.020"  # scripted group (container) (typed FeaturePython)
  n = 0.00189
FEATURE [App::DocumentObjectGroupPython] Br_element004  label="Br_element : 0.349"  # scripted group (container) (typed FeaturePython)
  n = 0.349103
FEATURE [App::DocumentObjectGroupPython] Ag_element001  label="Ag_element : 0.474"  # scripted group (container) (typed FeaturePython)
  n = 0.474105
FEATURE [App::DocumentObjectGroupPython] I_element005  label="I_element : 0.003"  # scripted group (container) (typed FeaturePython)
  n = 0.00312
FEATURE [App::DocumentObjectGroupPython] G4_PHOTO_EMULSION  # scripted group (container) (typed FeaturePython)
  Dunit = g/cm3
  Dvalue = 3.815
  Group = -> [H_element070,C_element076,N_element035,O_element075,S_element019,Br_element004,Ag_element001,I_element005]
  conduct = 2
  density = 1
  expand = 3
  formula = G4_PHOTO_EMULSION
  name = G4_PHOTO_EMULSION
  specific = 4
FEATURE [App::DocumentObjectGroupPython] C_element077  label="C_element : 9"  # scripted group (container) (typed FeaturePython)
  n = 9
  ref = C_element
FEATURE [App::DocumentObjectGroupPython] H_element071  label="H_element : 033"  # scripted group (container) (typed FeaturePython)
  n = 10
  ref = H_element
FEATURE [App::DocumentObjectGroupPython] G4_PLASTIC_SC_VINYLTOLUENE  # scripted group (container) (typed FeaturePython)
  Dunit = g/cm3
  Dvalue = 1.032
  Group = -> [C_element077,H_element071]
  conduct = 2
  density = 1
  expand = 3
  formula = G4_PLASTIC_SC_VINYLTOLUENE
  name = G4_PLASTIC_SC_VINYLTOLUENE
  specific = 4
FEATURE [App::DocumentObjectGroupPython] Pu_element001  label="Pu_element : 1"  # scripted group (container) (typed FeaturePython)
  n = 1
  ref = Pu_element
FEATURE [App::DocumentObjectGroupPython] O_element076  label="O_element : 037"  # scripted group (container) (typed FeaturePython)
  n = 2
  ref = O_element
FEATURE [App::DocumentObjectGroupPython] G4_PLUTONIUM_DIOXIDE  # scripted group (container) (typed FeaturePython)
  Dunit = g/cm3
  Dvalue = 11.46
  Group = -> [Pu_element001,O_element076]
  conduct = 2
  density = 1
  expand = 3
  formula = G4_PLUTONIUM_DIOXIDE
  name = G4_PLUTONIUM_DIOXIDE
  specific = 4
FEATURE [App::DocumentObjectGroupPython] C_element078  label="C_element : 037"  # scripted group (container) (typed FeaturePython)
  n = 3
  ref = C_element
FEATURE [App::DocumentObjectGroupPython] H_element072  label="H_element : 034"  # scripted group (container) (typed FeaturePython)
  n = 3
  ref = H_element
FEATURE [App::DocumentObjectGroupPython] N_element036  label="N_element : 015"  # scripted group (container) (typed FeaturePython)
  n = 1
  ref = N_element
FEATURE [App::DocumentObjectGroupPython] G4_POLYACRYLONITRILE  # scripted group (container) (typed FeaturePython)
  Dunit = g/cm3
  Dvalue = 1.17
  Group = -> [C_element078,H_element072,N_element036]
  conduct = 2
  density = 1
  expand = 3
  formula = G4_POLYACRYLONITRILE
  name = G4_POLYACRYLONITRILE
  specific = 4
FEATURE [App::DocumentObjectGroupPython] C_element079  label="C_element : 16"  # scripted group (container) (typed FeaturePython)
  n = 16
  ref = C_element
FEATURE [App::DocumentObjectGroupPython] H_element073  label="H_element : 035"  # scripted group (container) (typed FeaturePython)
  n = 14
  ref = H_element
FEATURE [App::DocumentObjectGroupPython] O_element077  label="O_element : 038"  # scripted group (container) (typed FeaturePython)
  n = 3
  ref = O_element
FEATURE [App::DocumentObjectGroupPython] G4_POLYCARBONATE  # scripted group (container) (typed FeaturePython)
  Dunit = g/cm3
  Dvalue = 1.2
  Group = -> [C_element079,H_element073,O_element077]
  conduct = 2
  density = 1
  expand = 3
  formula = G4_POLYCARBONATE
  name = G4_POLYCARBONATE
  specific = 4
FEATURE [App::DocumentObjectGroupPython] C_element080  label="C_element : 038"  # scripted group (container) (typed FeaturePython)
  n = 8
  ref = C_element
FEATURE [App::DocumentObjectGroupPython] H_element074  label="H_element : 036"  # scripted group (container) (typed FeaturePython)
  n = 7
  ref = H_element
FEATURE [App::DocumentObjectGroupPython] Cl_element017  label="Cl_element : 007"  # scripted group (container) (typed FeaturePython)
  n = 1
  ref = Cl_element
FEATURE [App::DocumentObjectGroupPython] G4_POLYCHLOROSTYRENE  # scripted group (container) (typed FeaturePython)
  Dunit = g/cm3
  Dvalue = 1.3
  Group = -> [C_element080,H_element074,Cl_element017]
  conduct = 2
  density = 1
  expand = 3
  formula = G4_POLYCHLOROSTYRENE
  name = G4_POLYCHLOROSTYRENE
  specific = 4
FEATURE [App::DocumentObjectGroupPython] C_element081  label="C_element : 039"  # scripted group (container) (typed FeaturePython)
  n = 1
  ref = C_element
FEATURE [App::DocumentObjectGroupPython] H_element075  label="H_element : 037"  # scripted group (container) (typed FeaturePython)
  n = 2
  ref = H_element
FEATURE [App::DocumentObjectGroupPython] G4_POLYETHYLENE  # scripted group (container) (typed FeaturePython)
  Dunit = g/cm3
  Dvalue = 0.94
  Group = -> [C_element081,H_element075]
  conduct = 2
  density = 1
  expand = 3
  formula = G4_POLYETHYLENE
  name = G4_POLYETHYLENE
  specific = 4
FEATURE [App::DocumentObjectGroupPython] C_element082  label="C_element : 040"  # scripted group (container) (typed FeaturePython)
  n = 10
  ref = C_element
FEATURE [App::DocumentObjectGroupPython] H_element076  label="H_element : 038"  # scripted group (container) (typed FeaturePython)
  n = 8
  ref = H_element
FEATURE [App::DocumentObjectGroupPython] O_element078  label="O_element : 039"  # scripted group (container) (typed FeaturePython)
  n = 4
  ref = O_element
FEATURE [App::DocumentObjectGroupPython] G4_MYLAR  # scripted group (container) (typed FeaturePython)
  Dunit = g/cm3
  Dvalue = 1.4
  Group = -> [C_element082,H_element076,O_element078]
  conduct = 2
  density = 1
  expand = 3
  formula = G4_MYLAR
  name = G4_MYLAR
  specific = 4
FEATURE [App::DocumentObjectGroupPython] C_element083  label="C_element : 041"  # scripted group (container) (typed FeaturePython)
  n = 5
  ref = C_element
FEATURE [App::DocumentObjectGroupPython] H_element077  label="H_element : 039"  # scripted group (container) (typed FeaturePython)
  n = 8
  ref = H_element
FEATURE [App::DocumentObjectGroupPython] O_element079  label="O_element : 040"  # scripted group (container) (typed FeaturePython)
  n = 2
  ref = O_element
FEATURE [App::DocumentObjectGroupPython] G4_PLEXIGLASS  # scripted group (container) (typed FeaturePython)
  Dunit = g/cm3
  Dvalue = 1.19
  Group = -> [C_element083,H_element077,O_element079]
  conduct = 2
  density = 1
  expand = 3
  formula = G4_PLEXIGLASS
  name = G4_PLEXIGLASS
  specific = 4
FEATURE [App::DocumentObjectGroupPython] C_element084  label="C_element : 042"  # scripted group (container) (typed FeaturePython)
  n = 1
  ref = C_element
FEATURE [App::DocumentObjectGroupPython] H_element078  label="H_element : 040"  # scripted group (container) (typed FeaturePython)
  n = 2
  ref = H_element
FEATURE [App::DocumentObjectGroupPython] O_element080  label="O_element : 041"  # scripted group (container) (typed FeaturePython)
  n = 1
  ref = O_element
FEATURE [App::DocumentObjectGroupPython] G4_POLYOXYMETHYLENE  # scripted group (container) (typed FeaturePython)
  Dunit = g/cm3
  Dvalue = 1.425
  Group = -> [C_element084,H_element078,O_element080]
  conduct = 2
  density = 1
  expand = 3
  formula = G4_POLYOXYMETHYLENE
  name = G4_POLYOXYMETHYLENE
  specific = 4
FEATURE [App::DocumentObjectGroupPython] C_element085  label="C_element : 043"  # scripted group (container) (typed FeaturePython)
  n = 2
  ref = C_element
FEATURE [App::DocumentObjectGroupPython] H_element079  label="H_element : 041"  # scripted group (container) (typed FeaturePython)
  n = 4
  ref = H_element
FEATURE [App::DocumentObjectGroupPython] G4_POLYPROPYLENE  # scripted group (container) (typed FeaturePython)
  Dunit = g/cm3
  Dvalue = 0.9
  Group = -> [C_element085,H_element079]
  conduct = 2
  density = 1
  expand = 3
  formula = G4_POLYPROPYLENE
  name = G4_POLYPROPYLENE
  specific = 4
FEATURE [App::DocumentObjectGroupPython] C_element086  label="C_element : 044"  # scripted group (container) (typed FeaturePython)
  n = 8
  ref = C_element
FEATURE [App::DocumentObjectGroupPython] H_element080  label="H_element : 042"  # scripted group (container) (typed FeaturePython)
  n = 8
  ref = H_element
FEATURE [App::DocumentObjectGroupPython] G4_POLYSTYRENE  # scripted group (container) (typed FeaturePython)
  Dunit = g/cm3
  Dvalue = 1.06
  Group = -> [C_element086,H_element080]
  conduct = 2
  density = 1
  expand = 3
  formula = G4_POLYSTYRENE
  name = G4_POLYSTYRENE
  specific = 4
FEATURE [App::DocumentObjectGroupPython] C_element087  label="C_element : 045"  # scripted group (container) (typed FeaturePython)
  n = 2
  ref = C_element
FEATURE [App::DocumentObjectGroupPython] F_element014  label="F_element : 4"  # scripted group (container) (typed FeaturePython)
  n = 4
  ref = F_element
FEATURE [App::DocumentObjectGroupPython] G4_TEFLON  # scripted group (container) (typed FeaturePython)
  Dunit = g/cm3
  Dvalue = 2.2
  Group = -> [C_element087,F_element014]
  conduct = 2
  density = 1
  expand = 3
  formula = G4_TEFLON
  name = G4_TEFLON
  specific = 4
FEATURE [App::DocumentObjectGroupPython] C_element088  label="C_element : 046"  # scripted group (container) (typed FeaturePython)
  n = 2
  ref = C_element
FEATURE [App::DocumentObjectGroupPython] F_element015  label="F_element : 006"  # scripted group (container) (typed FeaturePython)
  n = 3
  ref = F_element
FEATURE [App::DocumentObjectGroupPython] Cl_element018  label="Cl_element : 008"  # scripted group (container) (typed FeaturePython)
  n = 1
  ref = Cl_element
FEATURE [App::DocumentObjectGroupPython] G4_POLYTRIFLUOROCHLOROETHYLENE  # scripted group (container) (typed FeaturePython)
  Dunit = g/cm3
  Dvalue = 2.1
  Group = -> [C_element088,F_element015,Cl_element018]
  conduct = 2
  density = 1
  expand = 3
  formula = G4_POLYTRIFLUOROCHLOROETHYLENE
  name = G4_POLYTRIFLUOROCHLOROETHYLENE
  specific = 4
FEATURE [App::DocumentObjectGroupPython] C_element089  label="C_element : 047"  # scripted group (container) (typed FeaturePython)
  n = 4
  ref = C_element
FEATURE [App::DocumentObjectGroupPython] H_element081  label="H_element : 043"  # scripted group (container) (typed FeaturePython)
  n = 6
  ref = H_element
FEATURE [App::DocumentObjectGroupPython] O_element081  label="O_element : 042"  # scripted group (container) (typed FeaturePython)
  n = 2
  ref = O_element
FEATURE [App::DocumentObjectGroupPython] G4_POLYVINYL_ACETATE  # scripted group (container) (typed FeaturePython)
  Dunit = g/cm3
  Dvalue = 1.19
  Group = -> [C_element089,H_element081,O_element081]
  conduct = 2
  density = 1
  expand = 3
  formula = G4_POLYVINYL_ACETATE
  name = G4_POLYVINYL_ACETATE
  specific = 4
FEATURE [App::DocumentObjectGroupPython] C_element090  label="C_element : 048"  # scripted group (container) (typed FeaturePython)
  n = 2
  ref = C_element
FEATURE [App::DocumentObjectGroupPython] H_element082  label="H_element : 044"  # scripted group (container) (typed FeaturePython)
  n = 4
  ref = H_element
FEATURE [App::DocumentObjectGroupPython] O_element082  label="O_element : 043"  # scripted group (container) (typed FeaturePython)
  n = 1
  ref = O_element
FEATURE [App::DocumentObjectGroupPython] G4_POLYVINYL_ALCOHOL  # scripted group (container) (typed FeaturePython)
  Dunit = g/cm3
  Dvalue = 1.3
  Group = -> [C_element090,H_element082,O_element082]
  conduct = 2
  density = 1
  expand = 3
  formula = G4_POLYVINYL_ALCOHOL
  name = G4_POLYVINYL_ALCOHOL
  specific = 4
FEATURE [App::DocumentObjectGroupPython] C_element091  label="C_element : 049"  # scripted group (container) (typed FeaturePython)
  n = 8
  ref = C_element
FEATURE [App::DocumentObjectGroupPython] H_element083  label="H_element : 045"  # scripted group (container) (typed FeaturePython)
  n = 14
  ref = H_element
FEATURE [App::DocumentObjectGroupPython] O_element083  label="O_element : 044"  # scripted group (container) (typed FeaturePython)
  n = 2
  ref = O_element
FEATURE [App::DocumentObjectGroupPython] G4_POLYVINYL_BUTYRAL  # scripted group (container) (typed FeaturePython)
  Dunit = g/cm3
  Dvalue = 1.12
  Group = -> [C_element091,H_element083,O_element083]
  conduct = 2
  density = 1
  expand = 3
  formula = G4_POLYVINYL_BUTYRAL
  name = G4_POLYVINYL_BUTYRAL
  specific = 4
FEATURE [App::DocumentObjectGroupPython] C_element092  label="C_element : 050"  # scripted group (container) (typed FeaturePython)
  n = 2
  ref = C_element
FEATURE [App::DocumentObjectGroupPython] H_element084  label="H_element : 046"  # scripted group (container) (typed FeaturePython)
  n = 3
  ref = H_element
FEATURE [App::DocumentObjectGroupPython] Cl_element019  label="Cl_element : 009"  # scripted group (container) (typed FeaturePython)
  n = 1
  ref = Cl_element
FEATURE [App::DocumentObjectGroupPython] G4_POLYVINYL_CHLORIDE  # scripted group (container) (typed FeaturePython)
  Dunit = g/cm3
  Dvalue = 1.3
  Group = -> [C_element092,H_element084,Cl_element019]
  conduct = 2
  density = 1
  expand = 3
  formula = G4_POLYVINYL_CHLORIDE
  name = G4_POLYVINYL_CHLORIDE
  specific = 4
FEATURE [App::DocumentObjectGroupPython] C_element093  label="C_element : 051"  # scripted group (container) (typed FeaturePython)
  n = 2
  ref = C_element
FEATURE [App::DocumentObjectGroupPython] H_element085  label="H_element : 047"  # scripted group (container) (typed FeaturePython)
  n = 2
  ref = H_element
FEATURE [App::DocumentObjectGroupPython] Cl_element020  label="Cl_element : 010"  # scripted group (container) (typed FeaturePython)
  n = 2
  ref = Cl_element
FEATURE [App::DocumentObjectGroupPython] G4_POLYVINYLIDENE_CHLORIDE  # scripted group (container) (typed FeaturePython)
  Dunit = g/cm3
  Dvalue = 1.7
  Group = -> [C_element093,H_element085,Cl_element020]
  conduct = 2
  density = 1
  expand = 3
  formula = G4_POLYVINYLIDENE_CHLORIDE
  name = G4_POLYVINYLIDENE_CHLORIDE
  specific = 4
FEATURE [App::DocumentObjectGroupPython] C_element094  label="C_element : 052"  # scripted group (container) (typed FeaturePython)
  n = 2
  ref = C_element
FEATURE [App::DocumentObjectGroupPython] H_element086  label="H_element : 048"  # scripted group (container) (typed FeaturePython)
  n = 2
  ref = H_element
FEATURE [App::DocumentObjectGroupPython] F_element016  label="F_element : 007"  # scripted group (container) (typed FeaturePython)
  n = 2
  ref = F_element
FEATURE [App::DocumentObjectGroupPython] G4_POLYVINYLIDENE_FLUORIDE  # scripted group (container) (typed FeaturePython)
  Dunit = g/cm3
  Dvalue = 1.76
  Group = -> [C_element094,H_element086,F_element016]
  conduct = 2
  density = 1
  expand = 3
  formula = G4_POLYVINYLIDENE_FLUORIDE
  name = G4_POLYVINYLIDENE_FLUORIDE
  specific = 4
FEATURE [App::DocumentObjectGroupPython] C_element095  label="C_element : 053"  # scripted group (container) (typed FeaturePython)
  n = 6
  ref = C_element
FEATURE [App::DocumentObjectGroupPython] H_element087  label="H_element : 9"  # scripted group (container) (typed FeaturePython)
  n = 9
  ref = H_element
FEATURE [App::DocumentObjectGroupPython] N_element037  label="N_element : 016"  # scripted group (container) (typed FeaturePython)
  n = 1
  ref = N_element
FEATURE [App::DocumentObjectGroupPython] O_element084  label="O_element : 045"  # scripted group (container) (typed FeaturePython)
  n = 1
  ref = O_element
FEATURE [App::DocumentObjectGroupPython] G4_POLYVINYL_PYRROLIDONE  # scripted group (container) (typed FeaturePython)
  Dunit = g/cm3
  Dvalue = 1.25
  Group = -> [C_element095,H_element087,N_element037,O_element084]
  conduct = 2
  density = 1
  expand = 3
  formula = G4_POLYVINYL_PYRROLIDONE
  name = G4_POLYVINYL_PYRROLIDONE
  specific = 4
FEATURE [App::DocumentObjectGroupPython] K_element008  label="K_element : 1"  # scripted group (container) (typed FeaturePython)
  n = 1
  ref = K_element
FEATURE [App::DocumentObjectGroupPython] I_element006  label="I_element : 003"  # scripted group (container) (typed FeaturePython)
  n = 1
  ref = I_element
FEATURE [App::DocumentObjectGroupPython] G4_POTASSIUM_IODIDE  # scripted group (container) (typed FeaturePython)
  Dunit = g/cm3
  Dvalue = 3.13
  Group = -> [K_element008,I_element006]
  conduct = 2
  density = 1
  expand = 3
  formula = G4_POTASSIUM_IODIDE
  name = G4_POTASSIUM_IODIDE
  specific = 4
FEATURE [App::DocumentObjectGroupPython] K_element009  label="K_element : 2"  # scripted group (container) (typed FeaturePython)
  n = 2
  ref = K_element
FEATURE [App::DocumentObjectGroupPython] O_element085  label="O_element : 046"  # scripted group (container) (typed FeaturePython)
  n = 1
  ref = O_element
FEATURE [App::DocumentObjectGroupPython] G4_POTASSIUM_OXIDE  # scripted group (container) (typed FeaturePython)
  Dunit = g/cm3
  Dvalue = 2.32
  Group = -> [K_element009,O_element085]
  conduct = 2
  density = 1
  expand = 3
  formula = G4_POTASSIUM_OXIDE
  name = G4_POTASSIUM_OXIDE
  specific = 4
FEATURE [App::DocumentObjectGroupPython] C_element096  label="C_element : 054"  # scripted group (container) (typed FeaturePython)
  n = 3
  ref = C_element
FEATURE [App::DocumentObjectGroupPython] H_element088  label="H_element : 049"  # scripted group (container) (typed FeaturePython)
  n = 8
  ref = H_element
FEATURE [App::DocumentObjectGroupPython] G4_PROPANE  # scripted group (container) (typed FeaturePython)
  Dunit = g/cm3
  Dvalue = 0.00187939
  Group = -> [C_element096,H_element088]
  conduct = 2
  density = 1
  expand = 3
  formula = G4_PROPANE
  name = G4_PROPANE
  specific = 4
FEATURE [App::DocumentObjectGroupPython] C_element097  label="C_element : 055"  # scripted group (container) (typed FeaturePython)
  n = 3
  ref = C_element
FEATURE [App::DocumentObjectGroupPython] H_element089  label="H_element : 050"  # scripted group (container) (typed FeaturePython)
  n = 8
  ref = H_element
FEATURE [App::DocumentObjectGroupPython] G4_lPROPANE  # scripted group (container) (typed FeaturePython)
  Dunit = g/cm3
  Dvalue = 0.43
  Group = -> [C_element097,H_element089]
  conduct = 2
  density = 1
  expand = 3
  formula = G4_lPROPANE
  name = G4_lPROPANE
  specific = 4
FEATURE [App::DocumentObjectGroupPython] C_element098  label="C_element : 056"  # scripted group (container) (typed FeaturePython)
  n = 3
  ref = C_element
FEATURE [App::DocumentObjectGroupPython] H_element090  label="H_element : 051"  # scripted group (container) (typed FeaturePython)
  n = 8
  ref = H_element
FEATURE [App::DocumentObjectGroupPython] O_element086  label="O_element : 047"  # scripted group (container) (typed FeaturePython)
  n = 1
  ref = O_element
FEATURE [App::DocumentObjectGroupPython] G4_N_PROPYL_ALCOHOL  label="G4_N-PROPYL_ALCOHOL"  # scripted group (container) (typed FeaturePython)
  Dunit = g/cm3
  Dvalue = 0.8035
  Group = -> [C_element098,H_element090,O_element086]
  conduct = 2
  density = 1
  expand = 3
  formula = G4_N-PROPYL_ALCOHOL
  name = G4_N-PROPYL_ALCOHOL
  specific = 4
FEATURE [App::DocumentObjectGroupPython] C_element099  label="C_element : 057"  # scripted group (container) (typed FeaturePython)
  n = 5
  ref = C_element
FEATURE [App::DocumentObjectGroupPython] H_element091  label="H_element : 052"  # scripted group (container) (typed FeaturePython)
  n = 5
  ref = H_element
FEATURE [App::DocumentObjectGroupPython] N_element038  label="N_element : 017"  # scripted group (container) (typed FeaturePython)
  n = 1
  ref = N_element
FEATURE [App::DocumentObjectGroupPython] G4_PYRIDINE  # scripted group (container) (typed FeaturePython)
  Dunit = g/cm3
  Dvalue = 0.9819
  Group = -> [C_element099,H_element091,N_element038]
  conduct = 2
  density = 1
  expand = 3
  formula = G4_PYRIDINE
  name = G4_PYRIDINE
  specific = 4
FEATURE [App::DocumentObjectGroupPython] H_element092  label="H_element : 0.144"  # scripted group (container) (typed FeaturePython)
  n = 0.143711
FEATURE [App::DocumentObjectGroupPython] C_element100  label="C_element : 0.856"  # scripted group (container) (typed FeaturePython)
  n = 0.856289
FEATURE [App::DocumentObjectGroupPython] G4_RUBBER_BUTYL  # scripted group (container) (typed FeaturePython)
  Dunit = g/cm3
  Dvalue = 0.92
  Group = -> [H_element092,C_element100]
  conduct = 2
  density = 1
  expand = 3
  formula = G4_RUBBER_BUTYL
  name = G4_RUBBER_BUTYL
  specific = 4
FEATURE [App::DocumentObjectGroupPython] H_element093  label="H_element : 0.118"  # scripted group (container) (typed FeaturePython)
  n = 0.118371
FEATURE [App::DocumentObjectGroupPython] C_element101  label="C_element : 0.882"  # scripted group (container) (typed FeaturePython)
  n = 0.881629
FEATURE [App::DocumentObjectGroupPython] G4_RUBBER_NATURAL  # scripted group (container) (typed FeaturePython)
  Dunit = g/cm3
  Dvalue = 0.92
  Group = -> [H_element093,C_element101]
  conduct = 2
  density = 1
  expand = 3
  formula = G4_RUBBER_NATURAL
  name = G4_RUBBER_NATURAL
  specific = 4
FEATURE [App::DocumentObjectGroupPython] H_element094  label="H_element : 0.145"  # scripted group (container) (typed FeaturePython)
  n = 0.05692
FEATURE [App::DocumentObjectGroupPython] C_element102  label="C_element : 0.543"  # scripted group (container) (typed FeaturePython)
  n = 0.542646
FEATURE [App::DocumentObjectGroupPython] Cl_element021  label="Cl_element : 0.400"  # scripted group (container) (typed FeaturePython)
  n = 0.400434
FEATURE [App::DocumentObjectGroupPython] G4_RUBBER_NEOPRENE  # scripted group (container) (typed FeaturePython)
  Dunit = g/cm3
  Dvalue = 1.23
  Group = -> [H_element094,C_element102,Cl_element021]
  conduct = 2
  density = 1
  expand = 3
  formula = G4_RUBBER_NEOPRENE
  name = G4_RUBBER_NEOPRENE
  specific = 4
FEATURE [App::DocumentObjectGroupPython] Si_element006  label="Si_element : 1"  # scripted group (container) (typed FeaturePython)
  n = 1
  ref = Si_element
FEATURE [App::DocumentObjectGroupPython] O_element087  label="O_element : 048"  # scripted group (container) (typed FeaturePython)
  n = 2
  ref = O_element
FEATURE [App::DocumentObjectGroupPython] G4_SILICON_DIOXIDE  # scripted group (container) (typed FeaturePython)
  Dunit = g/cm3
  Dvalue = 2.32
  Group = -> [Si_element006,O_element087]
  conduct = 2
  density = 1
  expand = 3
  formula = G4_SILICON_DIOXIDE
  name = G4_SILICON_DIOXIDE
  specific = 4
FEATURE [App::DocumentObjectGroupPython] Ag_element002  label="Ag_element : 1"  # scripted group (container) (typed FeaturePython)
  n = 1
  ref = Ag_element
FEATURE [App::DocumentObjectGroupPython] Br_element005  label="Br_element : 003"  # scripted group (container) (typed FeaturePython)
  n = 1
  ref = Br_element
FEATURE [App::DocumentObjectGroupPython] G4_SILVER_BROMIDE  # scripted group (container) (typed FeaturePython)
  Dunit = g/cm3
  Dvalue = 6.473
  Group = -> [Ag_element002,Br_element005]
  conduct = 2
  density = 1
  expand = 3
  formula = G4_SILVER_BROMIDE
  name = G4_SILVER_BROMIDE
  specific = 4
FEATURE [App::DocumentObjectGroupPython] Ag_element003  label="Ag_element : 002"  # scripted group (container) (typed FeaturePython)
  n = 1
  ref = Ag_element
FEATURE [App::DocumentObjectGroupPython] Cl_element022  label="Cl_element : 011"  # scripted group (container) (typed FeaturePython)
  n = 1
  ref = Cl_element
FEATURE [App::DocumentObjectGroupPython] G4_SILVER_CHLORIDE  # scripted group (container) (typed FeaturePython)
  Dunit = g/cm3
  Dvalue = 5.56
  Group = -> [Ag_element003,Cl_element022]
  conduct = 2
  density = 1
  expand = 3
  formula = G4_SILVER_CHLORIDE
  name = G4_SILVER_CHLORIDE
  specific = 4
FEATURE [App::DocumentObjectGroupPython] Br_element006  label="Br_element : 0.423"  # scripted group (container) (typed FeaturePython)
  n = 0.422895
FEATURE [App::DocumentObjectGroupPython] Ag_element004  label="Ag_element : 0.574"  # scripted group (container) (typed FeaturePython)
  n = 0.573748
FEATURE [App::DocumentObjectGroupPython] I_element007  label="I_element : 0.649"  # scripted group (container) (typed FeaturePython)
  n = 0.003357
FEATURE [App::DocumentObjectGroupPython] G4_SILVER_HALIDES  # scripted group (container) (typed FeaturePython)
  Dunit = g/cm3
  Dvalue = 6.47
  Group = -> [Br_element006,Ag_element004,I_element007]
  conduct = 2
  density = 1
  expand = 3
  formula = G4_SILVER_HALIDES
  name = G4_SILVER_HALIDES
  specific = 4
FEATURE [App::DocumentObjectGroupPython] Ag_element005  label="Ag_element : 003"  # scripted group (container) (typed FeaturePython)
  n = 1
  ref = Ag_element
FEATURE [App::DocumentObjectGroupPython] I_element008  label="I_element : 004"  # scripted group (container) (typed FeaturePython)
  n = 1
  ref = I_element
FEATURE [App::DocumentObjectGroupPython] G4_SILVER_IODIDE  # scripted group (container) (typed FeaturePython)
  Dunit = g/cm3
  Dvalue = 6.01
  Group = -> [Ag_element005,I_element008]
  conduct = 2
  density = 1
  expand = 3
  formula = G4_SILVER_IODIDE
  name = G4_SILVER_IODIDE
  specific = 4
FEATURE [App::DocumentObjectGroupPython] H_element095  label="H_element : 0.100"  # scripted group (container) (typed FeaturePython)
  n = 0.1
FEATURE [App::DocumentObjectGroupPython] C_element103  label="C_element : 0.204"  # scripted group (container) (typed FeaturePython)
  n = 0.204
FEATURE [App::DocumentObjectGroupPython] N_element039  label="N_element : 0.759"  # scripted group (container) (typed FeaturePython)
  n = 0.042
FEATURE [App::DocumentObjectGroupPython] O_element088  label="O_element : 0.645"  # scripted group (container) (typed FeaturePython)
  n = 0.645
FEATURE [App::DocumentObjectGroupPython] Na_element013  label="Na_element : 0.100"  # scripted group (container) (typed FeaturePython)
  n = 0.002
FEATURE [App::DocumentObjectGroupPython] P_element009  label="P_element : 0.107"  # scripted group (container) (typed FeaturePython)
  n = 0.001
FEATURE [App::DocumentObjectGroupPython] S_element020  label="S_element : 0.021"  # scripted group (container) (typed FeaturePython)
  n = 0.002
FEATURE [App::DocumentObjectGroupPython] Cl_element023  label="Cl_element : 0.590"  # scripted group (container) (typed FeaturePython)
  n = 0.003
FEATURE [App::DocumentObjectGroupPython] K_element010  label="K_element : 0.001"  # scripted group (container) (typed FeaturePython)
  n = 0.001
FEATURE [App::DocumentObjectGroupPython] G4_SKIN_ICRP  # scripted group (container) (typed FeaturePython)
  Dunit = g/cm3
  Dvalue = 1.09
  Group = -> [H_element095,C_element103,N_element039,O_element088,Na_element013,P_element009,S_element020,Cl_element023,K_element010]
  conduct = 2
  density = 1
  expand = 3
  formula = G4_SKIN_ICRP
  name = G4_SKIN_ICRP
  specific = 4
FEATURE [App::DocumentObjectGroupPython] Na_element014  label="Na_element : 2"  # scripted group (container) (typed FeaturePython)
  n = 2
  ref = Na_element
FEATURE [App::DocumentObjectGroupPython] C_element104  label="C_element : 058"  # scripted group (container) (typed FeaturePython)
  n = 1
  ref = C_element
FEATURE [App::DocumentObjectGroupPython] O_element089  label="O_element : 049"  # scripted group (container) (typed FeaturePython)
  n = 3
  ref = O_element
FEATURE [App::DocumentObjectGroupPython] G4_SODIUM_CARBONATE  # scripted group (container) (typed FeaturePython)
  Dunit = g/cm3
  Dvalue = 2.532
  Group = -> [Na_element014,C_element104,O_element089]
  conduct = 2
  density = 1
  expand = 3
  formula = G4_SODIUM_CARBONATE
  name = G4_SODIUM_CARBONATE
  specific = 4
FEATURE [App::DocumentObjectGroupPython] Na_element015  label="Na_element : 1"  # scripted group (container) (typed FeaturePython)
  n = 1
  ref = Na_element
FEATURE [App::DocumentObjectGroupPython] I_element009  label="I_element : 005"  # scripted group (container) (typed FeaturePython)
  n = 1
  ref = I_element
FEATURE [App::DocumentObjectGroupPython] G4_SODIUM_IODIDE  # scripted group (container) (typed FeaturePython)
  Dunit = g/cm3
  Dvalue = 3.667
  Group = -> [Na_element015,I_element009]
  conduct = 2
  density = 1
  expand = 3
  formula = G4_SODIUM_IODIDE
  name = G4_SODIUM_IODIDE
  specific = 4
FEATURE [App::DocumentObjectGroupPython] Na_element016  label="Na_element : 003"  # scripted group (container) (typed FeaturePython)
  n = 2
  ref = Na_element
FEATURE [App::DocumentObjectGroupPython] O_element090  label="O_element : 050"  # scripted group (container) (typed FeaturePython)
  n = 1
  ref = O_element
FEATURE [App::DocumentObjectGroupPython] G4_SODIUM_MONOXIDE  # scripted group (container) (typed FeaturePython)
  Dunit = g/cm3
  Dvalue = 2.27
  Group = -> [Na_element016,O_element090]
  conduct = 2
  density = 1
  expand = 3
  formula = G4_SODIUM_MONOXIDE
  name = G4_SODIUM_MONOXIDE
  specific = 4
FEATURE [App::DocumentObjectGroupPython] Na_element017  label="Na_element : 004"  # scripted group (container) (typed FeaturePython)
  n = 1
  ref = Na_element
FEATURE [App::DocumentObjectGroupPython] N_element040  label="N_element : 018"  # scripted group (container) (typed FeaturePython)
  n = 1
  ref = N_element
FEATURE [App::DocumentObjectGroupPython] O_element091  label="O_element : 051"  # scripted group (container) (typed FeaturePython)
  n = 3
  ref = O_element
FEATURE [App::DocumentObjectGroupPython] G4_SODIUM_NITRATE  # scripted group (container) (typed FeaturePython)
  Dunit = g/cm3
  Dvalue = 2.261
  Group = -> [Na_element017,N_element040,O_element091]
  conduct = 2
  density = 1
  expand = 3
  formula = G4_SODIUM_NITRATE
  name = G4_SODIUM_NITRATE
  specific = 4
FEATURE [App::DocumentObjectGroupPython] C_element105  label="C_element : 059"  # scripted group (container) (typed FeaturePython)
  n = 14
  ref = C_element
FEATURE [App::DocumentObjectGroupPython] H_element096  label="H_element : 053"  # scripted group (container) (typed FeaturePython)
  n = 12
  ref = H_element
FEATURE [App::DocumentObjectGroupPython] G4_STILBENE  # scripted group (container) (typed FeaturePython)
  Dunit = g/cm3
  Dvalue = 0.9707
  Group = -> [C_element105,H_element096]
  conduct = 2
  density = 1
  expand = 3
  formula = G4_STILBENE
  name = G4_STILBENE
  specific = 4
FEATURE [App::DocumentObjectGroupPython] C_element106  label="C_element : 12"  # scripted group (container) (typed FeaturePython)
  n = 12
  ref = C_element
FEATURE [App::DocumentObjectGroupPython] H_element097  label="H_element : 22"  # scripted group (container) (typed FeaturePython)
  n = 22
  ref = H_element
FEATURE [App::DocumentObjectGroupPython] O_element092  label="O_element : 11"  # scripted group (container) (typed FeaturePython)
  n = 11
  ref = O_element
FEATURE [App::DocumentObjectGroupPython] G4_SUCROSE  # scripted group (container) (typed FeaturePython)
  Dunit = g/cm3
  Dvalue = 1.5805
  Group = -> [C_element106,H_element097,O_element092]
  conduct = 2
  density = 1
  expand = 3
  formula = G4_SUCROSE
  name = G4_SUCROSE
  specific = 4
FEATURE [App::DocumentObjectGroupPython] C_element107  label="C_element : 18"  # scripted group (container) (typed FeaturePython)
  n = 18
  ref = C_element
FEATURE [App::DocumentObjectGroupPython] H_element098  label="H_element : 054"  # scripted group (container) (typed FeaturePython)
  n = 14
  ref = H_element
FEATURE [App::DocumentObjectGroupPython] G4_TERPHENYL  # scripted group (container) (typed FeaturePython)
  Dunit = g/cm3
  Dvalue = 1.24
  Group = -> [C_element107,H_element098]
  conduct = 2
  density = 1
  expand = 3
  formula = G4_TERPHENYL
  name = G4_TERPHENYL
  specific = 4
FEATURE [App::DocumentObjectGroupPython] H_element099  label="H_element : 0.146"  # scripted group (container) (typed FeaturePython)
  n = 0.106
FEATURE [App::DocumentObjectGroupPython] C_element108  label="C_element : 0.883"  # scripted group (container) (typed FeaturePython)
  n = 0.099
FEATURE [App::DocumentObjectGroupPython] N_element041  label="N_element : 0.020"  # scripted group (container) (typed FeaturePython)
  n = 0.02
FEATURE [App::DocumentObjectGroupPython] O_element093  label="O_element : 0.766"  # scripted group (container) (typed FeaturePython)
  n = 0.766
FEATURE [App::DocumentObjectGroupPython] Na_element018  label="Na_element : 0.101"  # scripted group (container) (typed FeaturePython)
  n = 0.002
FEATURE [App::DocumentObjectGroupPython] P_element010  label="P_element : 0.108"  # scripted group (container) (typed FeaturePython)
  n = 0.001
FEATURE [App::DocumentObjectGroupPython] S_element021  label="S_element : 0.022"  # scripted group (container) (typed FeaturePython)
  n = 0.002
FEATURE [App::DocumentObjectGroupPython] Cl_element024  label="Cl_element : 0.002"  # scripted group (container) (typed FeaturePython)
  n = 0.002
FEATURE [App::DocumentObjectGroupPython] K_element011  label="K_element : 0.017"  # scripted group (container) (typed FeaturePython)
  n = 0.002
FEATURE [App::DocumentObjectGroupPython] G4_TESTIS_ICRP  # scripted group (container) (typed FeaturePython)
  Dunit = g/cm3
  Dvalue = 1.04
  Group = -> [H_element099,C_element108,N_element041,O_element093,Na_element018,P_element010,S_element021,Cl_element024,K_element011]
  conduct = 2
  density = 1
  expand = 3
  formula = G4_TESTIS_ICRP
  name = G4_TESTIS_ICRP
  specific = 4
FEATURE [App::DocumentObjectGroupPython] C_element109  label="C_element : 060"  # scripted group (container) (typed FeaturePython)
  n = 2
  ref = C_element
FEATURE [App::DocumentObjectGroupPython] Cl_element025  label="Cl_element : 012"  # scripted group (container) (typed FeaturePython)
  n = 4
  ref = Cl_element
FEATURE [App::DocumentObjectGroupPython] G4_TETRACHLOROETHYLENE  # scripted group (container) (typed FeaturePython)
  Dunit = g/cm3
  Dvalue = 1.625
  Group = -> [C_element109,Cl_element025]
  conduct = 2
  density = 1
  expand = 3
  formula = G4_TETRACHLOROETHYLENE
  name = G4_TETRACHLOROETHYLENE
  specific = 4
FEATURE [App::DocumentObjectGroupPython] Tl_element001  label="Tl_element : 1"  # scripted group (container) (typed FeaturePython)
  n = 1
  ref = Tl_element
FEATURE [App::DocumentObjectGroupPython] Cl_element026  label="Cl_element : 013"  # scripted group (container) (typed FeaturePython)
  n = 1
  ref = Cl_element
FEATURE [App::DocumentObjectGroupPython] G4_THALLIUM_CHLORIDE  # scripted group (container) (typed FeaturePython)
  Dunit = g/cm3
  Dvalue = 7.004
  Group = -> [Tl_element001,Cl_element026]
  conduct = 2
  density = 1
  expand = 3
  formula = G4_THALLIUM_CHLORIDE
  name = G4_THALLIUM_CHLORIDE
  specific = 4
FEATURE [App::DocumentObjectGroupPython] H_element100  label="H_element : 0.147"  # scripted group (container) (typed FeaturePython)
  n = 0.105
FEATURE [App::DocumentObjectGroupPython] C_element110  label="C_element : 0.256"  # scripted group (container) (typed FeaturePython)
  n = 0.256
FEATURE [App::DocumentObjectGroupPython] N_element042  label="N_element : 0.760"  # scripted group (container) (typed FeaturePython)
  n = 0.027
FEATURE [App::DocumentObjectGroupPython] O_element094  label="O_element : 0.602"  # scripted group (container) (typed FeaturePython)
  n = 0.602
FEATURE [App::DocumentObjectGroupPython] Na_element019  label="Na_element : 0.102"  # scripted group (container) (typed FeaturePython)
  n = 0.001
FEATURE [App::DocumentObjectGroupPython] P_element011  label="P_element : 0.109"  # scripted group (container) (typed FeaturePython)
  n = 0.002
FEATURE [App::DocumentObjectGroupPython] S_element022  label="S_element : 0.023"  # scripted group (container) (typed FeaturePython)
  n = 0.003
FEATURE [App::DocumentObjectGroupPython] Cl_element027  label="Cl_element : 0.591"  # scripted group (container) (typed FeaturePython)
  n = 0.002
FEATURE [App::DocumentObjectGroupPython] K_element012  label="K_element : 0.018"  # scripted group (container) (typed FeaturePython)
  n = 0.002
FEATURE [App::DocumentObjectGroupPython] G4_TISSUE_SOFT_ICRP  # scripted group (container) (typed FeaturePython)
  Dunit = g/cm3
  Dvalue = 1.03
  Group = -> [H_element100,C_element110,N_element042,O_element094,Na_element019,P_element011,S_element022,Cl_element027,K_element012]
  conduct = 2
  density = 1
  expand = 3
  formula = G4_TISSUE_SOFT_ICRP
  name = G4_TISSUE_SOFT_ICRP
  specific = 4
FEATURE [App::DocumentObjectGroupPython] H_element101  label="H_element : 0.148"  # scripted group (container) (typed FeaturePython)
  n = 0.101
FEATURE [App::DocumentObjectGroupPython] C_element111  label="C_element : 0.111"  # scripted group (container) (typed FeaturePython)
  n = 0.111
FEATURE [App::DocumentObjectGroupPython] N_element043  label="N_element : 0.026"  # scripted group (container) (typed FeaturePython)
  n = 0.026
FEATURE [App::DocumentObjectGroupPython] O_element095  label="O_element : 0.762"  # scripted group (container) (typed FeaturePython)
  n = 0.762
FEATURE [App::DocumentObjectGroupPython] G4_TISSUE_SOFT_ICRU_4  label="G4_TISSUE_SOFT_ICRU-4"  # scripted group (container) (typed FeaturePython)
  Dunit = g/cm3
  Dvalue = 1
  Group = -> [H_element101,C_element111,N_element043,O_element095]
  conduct = 2
  density = 1
  expand = 3
  formula = G4_TISSUE_SOFT_ICRU-4
  name = G4_TISSUE_SOFT_ICRU-4
  specific = 4
FEATURE [App::DocumentObjectGroupPython] H_element102  label="H_element : 0.149"  # scripted group (container) (typed FeaturePython)
  n = 0.101869
FEATURE [App::DocumentObjectGroupPython] C_element112  label="C_element : 0.456"  # scripted group (container) (typed FeaturePython)
  n = 0.456179
FEATURE [App::DocumentObjectGroupPython] N_element044  label="N_element : 0.761"  # scripted group (container) (typed FeaturePython)
  n = 0.035172
FEATURE [App::DocumentObjectGroupPython] O_element096  label="O_element : 0.407"  # scripted group (container) (typed FeaturePython)
  n = 0.40678
FEATURE [App::DocumentObjectGroupPython] G4_TISSUE_METHANE  label="G4_TISSUE-METHANE"  # scripted group (container) (typed FeaturePython)
  Dunit = g/cm3
  Dvalue = 0.00106409
  Group = -> [H_element102,C_element112,N_element044,O_element096]
  conduct = 2
  density = 1
  expand = 3
  formula = G4_TISSUE-METHANE
  name = G4_TISSUE-METHANE
  specific = 4
FEATURE [App::DocumentObjectGroupPython] H_element103  label="H_element : 0.103"  # scripted group (container) (typed FeaturePython)
  n = 0.102672
FEATURE [App::DocumentObjectGroupPython] C_element113  label="C_element : 0.569"  # scripted group (container) (typed FeaturePython)
  n = 0.56894
FEATURE [App::DocumentObjectGroupPython] N_element045  label="N_element : 0.762"  # scripted group (container) (typed FeaturePython)
  n = 0.035022
FEATURE [App::DocumentObjectGroupPython] O_element097  label="O_element : 0.293"  # scripted group (container) (typed FeaturePython)
  n = 0.293366
FEATURE [App::DocumentObjectGroupPython] G4_TISSUE_PROPANE  label="G4_TISSUE-PROPANE"  # scripted group (container) (typed FeaturePython)
  Dunit = g/cm3
  Dvalue = 0.00182628
  Group = -> [H_element103,C_element113,N_element045,O_element097]
  conduct = 2
  density = 1
  expand = 3
  formula = G4_TISSUE-PROPANE
  name = G4_TISSUE-PROPANE
  specific = 4
FEATURE [App::DocumentObjectGroupPython] Ti_element003  label="Ti_element : 1"  # scripted group (container) (typed FeaturePython)
  n = 1
  ref = Ti_element
FEATURE [App::DocumentObjectGroupPython] O_element098  label="O_element : 052"  # scripted group (container) (typed FeaturePython)
  n = 2
  ref = O_element
FEATURE [App::DocumentObjectGroupPython] G4_TITANIUM_DIOXIDE  # scripted group (container) (typed FeaturePython)
  Dunit = g/cm3
  Dvalue = 4.26
  Group = -> [Ti_element003,O_element098]
  conduct = 2
  density = 1
  expand = 3
  formula = G4_TITANIUM_DIOXIDE
  name = G4_TITANIUM_DIOXIDE
  specific = 4
FEATURE [App::DocumentObjectGroupPython] C_element114  label="C_element : 061"  # scripted group (container) (typed FeaturePython)
  n = 7
  ref = C_element
FEATURE [App::DocumentObjectGroupPython] H_element104  label="H_element : 055"  # scripted group (container) (typed FeaturePython)
  n = 8
  ref = H_element
FEATURE [App::DocumentObjectGroupPython] G4_TOLUENE  # scripted group (container) (typed FeaturePython)
  Dunit = g/cm3
  Dvalue = 0.8669
  Group = -> [C_element114,H_element104]
  conduct = 2
  density = 1
  expand = 3
  formula = G4_TOLUENE
  name = G4_TOLUENE
  specific = 4
FEATURE [App::DocumentObjectGroupPython] C_element115  label="C_element : 062"  # scripted group (container) (typed FeaturePython)
  n = 2
  ref = C_element
FEATURE [App::DocumentObjectGroupPython] H_element105  label="H_element : 056"  # scripted group (container) (typed FeaturePython)
  n = 1
  ref = H_element
FEATURE [App::DocumentObjectGroupPython] Cl_element028  label="Cl_element : 014"  # scripted group (container) (typed FeaturePython)
  n = 3
  ref = Cl_element
FEATURE [App::DocumentObjectGroupPython] G4_TRICHLOROETHYLENE  # scripted group (container) (typed FeaturePython)
  Dunit = g/cm3
  Dvalue = 1.46
  Group = -> [C_element115,H_element105,Cl_element028]
  conduct = 2
  density = 1
  expand = 3
  formula = G4_TRICHLOROETHYLENE
  name = G4_TRICHLOROETHYLENE
  specific = 4
FEATURE [App::DocumentObjectGroupPython] C_element116  label="C_element : 063"  # scripted group (container) (typed FeaturePython)
  n = 6
  ref = C_element
FEATURE [App::DocumentObjectGroupPython] H_element106  label="H_element : 15"  # scripted group (container) (typed FeaturePython)
  n = 15
  ref = H_element
FEATURE [App::DocumentObjectGroupPython] O_element099  label="O_element : 053"  # scripted group (container) (typed FeaturePython)
  n = 4
  ref = O_element
FEATURE [App::DocumentObjectGroupPython] P_element012  label="P_element : 1"  # scripted group (container) (typed FeaturePython)
  n = 1
  ref = P_element
FEATURE [App::DocumentObjectGroupPython] G4_TRIETHYL_PHOSPHATE  # scripted group (container) (typed FeaturePython)
  Dunit = g/cm3
  Dvalue = 1.07
  Group = -> [C_element116,H_element106,O_element099,P_element012]
  conduct = 2
  density = 1
  expand = 3
  formula = G4_TRIETHYL_PHOSPHATE
  name = G4_TRIETHYL_PHOSPHATE
  specific = 4
FEATURE [App::DocumentObjectGroupPython] W_element003  label="W_element : 003"  # scripted group (container) (typed FeaturePython)
  n = 1
  ref = W_element
FEATURE [App::DocumentObjectGroupPython] F_element017  label="F_element : 6"  # scripted group (container) (typed FeaturePython)
  n = 6
  ref = F_element
FEATURE [App::DocumentObjectGroupPython] G4_TUNGSTEN_HEXAFLUORIDE  # scripted group (container) (typed FeaturePython)
  Dunit = g/cm3
  Dvalue = 2.4
  Group = -> [W_element003,F_element017]
  conduct = 2
  density = 1
  expand = 3
  formula = G4_TUNGSTEN_HEXAFLUORIDE
  name = G4_TUNGSTEN_HEXAFLUORIDE
  specific = 4
FEATURE [App::DocumentObjectGroupPython] U_element001  label="U_element : 1"  # scripted group (container) (typed FeaturePython)
  n = 1
  ref = U_element
FEATURE [App::DocumentObjectGroupPython] C_element117  label="C_element : 064"  # scripted group (container) (typed FeaturePython)
  n = 2
  ref = C_element
FEATURE [App::DocumentObjectGroupPython] G4_URANIUM_DICARBIDE  # scripted group (container) (typed FeaturePython)
  Dunit = g/cm3
  Dvalue = 11.28
  Group = -> [U_element001,C_element117]
  conduct = 2
  density = 1
  expand = 3
  formula = G4_URANIUM_DICARBIDE
  name = G4_URANIUM_DICARBIDE
  specific = 4
FEATURE [App::DocumentObjectGroupPython] U_element002  label="U_element : 002"  # scripted group (container) (typed FeaturePython)
  n = 1
  ref = U_element
FEATURE [App::DocumentObjectGroupPython] C_element118  label="C_element : 065"  # scripted group (container) (typed FeaturePython)
  n = 1
  ref = C_element
FEATURE [App::DocumentObjectGroupPython] G4_URANIUM_MONOCARBIDE  # scripted group (container) (typed FeaturePython)
  Dunit = g/cm3
  Dvalue = 13.63
  Group = -> [U_element002,C_element118]
  conduct = 2
  density = 1
  expand = 3
  formula = G4_URANIUM_MONOCARBIDE
  name = G4_URANIUM_MONOCARBIDE
  specific = 4
FEATURE [App::DocumentObjectGroupPython] U_element003  label="U_element : 003"  # scripted group (container) (typed FeaturePython)
  n = 1
  ref = U_element
FEATURE [App::DocumentObjectGroupPython] O_element100  label="O_element : 054"  # scripted group (container) (typed FeaturePython)
  n = 2
  ref = O_element
FEATURE [App::DocumentObjectGroupPython] G4_URANIUM_OXIDE  # scripted group (container) (typed FeaturePython)
  Dunit = g/cm3
  Dvalue = 10.96
  Group = -> [U_element003,O_element100]
  conduct = 2
  density = 1
  expand = 3
  formula = G4_URANIUM_OXIDE
  name = G4_URANIUM_OXIDE
  specific = 4
FEATURE [App::DocumentObjectGroupPython] C_element119  label="C_element : 066"  # scripted group (container) (typed FeaturePython)
  n = 1
  ref = C_element
FEATURE [App::DocumentObjectGroupPython] H_element107  label="H_element : 057"  # scripted group (container) (typed FeaturePython)
  n = 4
  ref = H_element
FEATURE [App::DocumentObjectGroupPython] N_element046  label="N_element : 019"  # scripted group (container) (typed FeaturePython)
  n = 2
  ref = N_element
FEATURE [App::DocumentObjectGroupPython] O_element101  label="O_element : 055"  # scripted group (container) (typed FeaturePython)
  n = 1
  ref = O_element
FEATURE [App::DocumentObjectGroupPython] G4_UREA  # scripted group (container) (typed FeaturePython)
  Dunit = g/cm3
  Dvalue = 1.323
  Group = -> [C_element119,H_element107,N_element046,O_element101]
  conduct = 2
  density = 1
  expand = 3
  formula = G4_UREA
  name = G4_UREA
  specific = 4
FEATURE [App::DocumentObjectGroupPython] C_element120  label="C_element : 067"  # scripted group (container) (typed FeaturePython)
  n = 5
  ref = C_element
FEATURE [App::DocumentObjectGroupPython] H_element108  label="H_element : 058"  # scripted group (container) (typed FeaturePython)
  n = 11
  ref = H_element
FEATURE [App::DocumentObjectGroupPython] N_element047  label="N_element : 020"  # scripted group (container) (typed FeaturePython)
  n = 1
  ref = N_element
FEATURE [App::DocumentObjectGroupPython] O_element102  label="O_element : 056"  # scripted group (container) (typed FeaturePython)
  n = 2
  ref = O_element
FEATURE [App::DocumentObjectGroupPython] G4_VALINE  # scripted group (container) (typed FeaturePython)
  Dunit = g/cm3
  Dvalue = 1.23
  Group = -> [C_element120,H_element108,N_element047,O_element102]
  conduct = 2
  density = 1
  expand = 3
  formula = G4_VALINE
  name = G4_VALINE
  specific = 4
FEATURE [App::DocumentObjectGroupPython] H_element109  label="H_element : 0.009"  # scripted group (container) (typed FeaturePython)
  n = 0.009417
FEATURE [App::DocumentObjectGroupPython] C_element121  label="C_element : 0.281"  # scripted group (container) (typed FeaturePython)
  n = 0.280555
FEATURE [App::DocumentObjectGroupPython] F_element018  label="F_element : 0.710"  # scripted group (container) (typed FeaturePython)
  n = 0.710028
FEATURE [App::DocumentObjectGroupPython] G4_VITON  # scripted group (container) (typed FeaturePython)
  Dunit = g/cm3
  Dvalue = 1.8
  Group = -> [H_element109,C_element121,F_element018]
  conduct = 2
  density = 1
  expand = 3
  formula = G4_VITON
  name = G4_VITON
  specific = 4
FEATURE [App::DocumentObjectGroupPython] H_element110  label="H_element : 059"  # scripted group (container) (typed FeaturePython)
  n = 2
  ref = H_element
FEATURE [App::DocumentObjectGroupPython] O_element103  label="O_element : 057"  # scripted group (container) (typed FeaturePython)
  n = 1
  ref = O_element
FEATURE [App::DocumentObjectGroupPython] G4_WATER  # scripted group (container) (typed FeaturePython)
  Dunit = g/cm3
  Dvalue = 1
  Group = -> [H_element110,O_element103]
  conduct = 2
  density = 1
  expand = 3
  formula = G4_WATER
  name = G4_WATER
  specific = 4
FEATURE [App::DocumentObjectGroupPython] H_element111  label="H_element : 060"  # scripted group (container) (typed FeaturePython)
  n = 2
  ref = H_element
FEATURE [App::DocumentObjectGroupPython] O_element104  label="O_element : 058"  # scripted group (container) (typed FeaturePython)
  n = 1
  ref = O_element
FEATURE [App::DocumentObjectGroupPython] G4_WATER_VAPOR  # scripted group (container) (typed FeaturePython)
  Dunit = g/cm3
  Dvalue = 0.000756182
  Group = -> [H_element111,O_element104]
  conduct = 2
  density = 1
  expand = 3
  formula = G4_WATER_VAPOR
  name = G4_WATER_VAPOR
  specific = 4
FEATURE [App::DocumentObjectGroupPython] C_element122  label="C_element : 068"  # scripted group (container) (typed FeaturePython)
  n = 8
  ref = C_element
FEATURE [App::DocumentObjectGroupPython] H_element112  label="H_element : 061"  # scripted group (container) (typed FeaturePython)
  n = 10
  ref = H_element
FEATURE [App::DocumentObjectGroupPython] G4_XYLENE  # scripted group (container) (typed FeaturePython)
  Dunit = g/cm3
  Dvalue = 0.87
  Group = -> [C_element122,H_element112]
  conduct = 2
  density = 1
  expand = 3
  formula = G4_XYLENE
  name = G4_XYLENE
  specific = 4
FEATURE [App::DocumentObjectGroupPython] C_element123  label="C_element : 069"  # scripted group (container) (typed FeaturePython)
  n = 1
  ref = C_element
FEATURE [App::DocumentObjectGroupPython] G4_GRAPHITE  # scripted group (container) (typed FeaturePython)
  Dunit = g/cm3
  Dvalue = 2.21
  Group = -> [C_element123]
  conduct = 2
  density = 1
  expand = 3
  formula = G4_GRAPHITE
  name = G4_GRAPHITE
  specific = 4
FEATURE [App::DocumentObjectGroupPython] NIST  # scripted group (container) (typed FeaturePython)
  Group = -> [G4_A_150_TISSUE,G4_ACETONE,G4_ACETYLENE,G4_ADENINE,G4_ADIPOSE_TISSUE_ICRP,G4_AIR,G4_ALANINE,G4_ALUMINUM_OXIDE,G4_AMBER,G4_AMMONIA,G4_ANILINE,G4_ANTHRACENE,G4_B_100_BONE,G4_BAKELITE,G4_BARIUM_FLUORIDE,G4_BARIUM_SULFATE,G4_BENZENE,G4_BERYLLIUM_OXIDE,G4_BGO,G4_BLOOD_ICRP,G4_BONE_COMPACT_ICRU,G4_BONE_CORTICAL_ICRP,G4_BORON_CARBIDE,G4_BORON_OXIDE,G4_BRAIN_ICRP,G4_BUTANE,G4_N_BUTYL_ALCOHOL,G4_C_552,+152 more]
FEATURE [App::DocumentObjectGroupPython] H_element113  label="H_element : 062"  # scripted group (container) (typed FeaturePython)
  n = 1
  ref = H_element
FEATURE [App::DocumentObjectGroupPython] G4_H  # scripted group (container) (typed FeaturePython)
  Dunit = g/cm3
  Dvalue = 8.3748e-05
  Group = -> [H_element113]
  conduct = 2
  density = 1
  expand = 3
  formula = H
  name = G4_H
  specific = 4
FEATURE [App::DocumentObjectGroupPython] He_element001  label="He_element : 1"  # scripted group (container) (typed FeaturePython)
  n = 1
  ref = He_element
FEATURE [App::DocumentObjectGroupPython] G4_He  # scripted group (container) (typed FeaturePython)
  Dunit = g/cm3
  Dvalue = 0.000166322
  Group = -> [He_element001]
  conduct = 2
  density = 1
  expand = 3
  formula = He
  name = G4_He
  specific = 4
FEATURE [App::DocumentObjectGroupPython] Li_element008  label="Li_element : 008"  # scripted group (container) (typed FeaturePython)
  n = 1
  ref = Li_element
FEATURE [App::DocumentObjectGroupPython] G4_Li  # scripted group (container) (typed FeaturePython)
  Dunit = g/cm3
  Dvalue = 0.534
  Group = -> [Li_element008]
  conduct = 2
  density = 1
  expand = 3
  formula = Li
  name = G4_Li
  specific = 4
FEATURE [App::DocumentObjectGroupPython] Be_element002  label="Be_element : 002"  # scripted group (container) (typed FeaturePython)
  n = 1
  ref = Be_element
FEATURE [App::DocumentObjectGroupPython] G4_Be  # scripted group (container) (typed FeaturePython)
  Dunit = g/cm3
  Dvalue = 1.848
  Group = -> [Be_element002]
  conduct = 2
  density = 1
  expand = 3
  formula = Be
  name = G4_Be
  specific = 4
FEATURE [App::DocumentObjectGroupPython] B_element007  label="B_element : 007"  # scripted group (container) (typed FeaturePython)
  n = 1
  ref = B_element
FEATURE [App::DocumentObjectGroupPython] G4_B  # scripted group (container) (typed FeaturePython)
  Dunit = g/cm3
  Dvalue = 2.37
  Group = -> [B_element007]
  conduct = 2
  density = 1
  expand = 3
  formula = B
  name = G4_B
  specific = 4
FEATURE [App::DocumentObjectGroupPython] C_element124  label="C_element : 070"  # scripted group (container) (typed FeaturePython)
  n = 1
  ref = C_element
FEATURE [App::DocumentObjectGroupPython] G4_C  # scripted group (container) (typed FeaturePython)
  Dunit = g/cm3
  Dvalue = 2
  Group = -> [C_element124]
  conduct = 2
  density = 1
  expand = 3
  formula = C
  name = G4_C
  specific = 4
FEATURE [App::DocumentObjectGroupPython] N_element048  label="N_element : 021"  # scripted group (container) (typed FeaturePython)
  n = 1
  ref = N_element
FEATURE [App::DocumentObjectGroupPython] G4_N  # scripted group (container) (typed FeaturePython)
  Dunit = g/cm3
  Dvalue = 0.0011652
  Group = -> [N_element048]
  conduct = 2
  density = 1
  expand = 3
  formula = N
  name = G4_N
  specific = 4
FEATURE [App::DocumentObjectGroupPython] O_element105  label="O_element : 059"  # scripted group (container) (typed FeaturePython)
  n = 1
  ref = O_element
FEATURE [App::DocumentObjectGroupPython] G4_O  # scripted group (container) (typed FeaturePython)
  Dunit = g/cm3
  Dvalue = 0.00133151
  Group = -> [O_element105]
  conduct = 2
  density = 1
  expand = 3
  formula = O
  name = G4_O
  specific = 4
FEATURE [App::DocumentObjectGroupPython] F_element019  label="F_element : 008"  # scripted group (container) (typed FeaturePython)
  n = 1
  ref = F_element
FEATURE [App::DocumentObjectGroupPython] G4_F  # scripted group (container) (typed FeaturePython)
  Dunit = g/cm3
  Dvalue = 0.00158029
  Group = -> [F_element019]
  conduct = 2
  density = 1
  expand = 3
  formula = F
  name = G4_F
  specific = 4
FEATURE [App::DocumentObjectGroupPython] Ne_element001  label="Ne_element : 1"  # scripted group (container) (typed FeaturePython)
  n = 1
  ref = Ne_element
FEATURE [App::DocumentObjectGroupPython] G4_Ne  # scripted group (container) (typed FeaturePython)
  Dunit = g/cm3
  Dvalue = 0.000838505
  Group = -> [Ne_element001]
  conduct = 2
  density = 1
  expand = 3
  formula = Ne
  name = G4_Ne
  specific = 4
FEATURE [App::DocumentObjectGroupPython] Na_element020  label="Na_element : 005"  # scripted group (container) (typed FeaturePython)
  n = 1
  ref = Na_element
FEATURE [App::DocumentObjectGroupPython] G4_Na  # scripted group (container) (typed FeaturePython)
  Dunit = g/cm3
  Dvalue = 0.971
  Group = -> [Na_element020]
  conduct = 2
  density = 1
  expand = 3
  formula = Na
  name = G4_Na
  specific = 4
FEATURE [App::DocumentObjectGroupPython] Mg_element011  label="Mg_element : 005"  # scripted group (container) (typed FeaturePython)
  n = 1
  ref = Mg_element
FEATURE [App::DocumentObjectGroupPython] G4_Mg  # scripted group (container) (typed FeaturePython)
  Dunit = g/cm3
  Dvalue = 1.74
  Group = -> [Mg_element011]
  conduct = 2
  density = 1
  expand = 3
  formula = Mg
  name = G4_Mg
  specific = 4
FEATURE [App::DocumentObjectGroupPython] Al_element004  label="Al_element : 1"  # scripted group (container) (typed FeaturePython)
  n = 1
  ref = Al_element
FEATURE [App::DocumentObjectGroupPython] G4_Al  # scripted group (container) (typed FeaturePython)
  Dunit = g/cm3
  Dvalue = 2.699
  Group = -> [Al_element004]
  conduct = 2
  density = 1
  expand = 3
  formula = Al
  name = G4_Al
  specific = 4
FEATURE [App::DocumentObjectGroupPython] Si_element007  label="Si_element : 002"  # scripted group (container) (typed FeaturePython)
  n = 1
  ref = Si_element
FEATURE [App::DocumentObjectGroupPython] G4_Si  # scripted group (container) (typed FeaturePython)
  Dunit = g/cm3
  Dvalue = 2.33
  Group = -> [Si_element007]
  conduct = 2
  density = 1
  expand = 3
  formula = Si
  name = G4_Si
  specific = 4
FEATURE [App::DocumentObjectGroupPython] P_element013  label="P_element : 002"  # scripted group (container) (typed FeaturePython)
  n = 1
  ref = P_element
FEATURE [App::DocumentObjectGroupPython] G4_P  # scripted group (container) (typed FeaturePython)
  Dunit = g/cm3
  Dvalue = 2.2
  Group = -> [P_element013]
  conduct = 2
  density = 1
  expand = 3
  formula = P
  name = G4_P
  specific = 4
FEATURE [App::DocumentObjectGroupPython] S_element023  label="S_element : 007"  # scripted group (container) (typed FeaturePython)
  n = 1
  ref = S_element
FEATURE [App::DocumentObjectGroupPython] G4_S  # scripted group (container) (typed FeaturePython)
  Dunit = g/cm3
  Dvalue = 2
  Group = -> [S_element023]
  conduct = 2
  density = 1
  expand = 3
  formula = S
  name = G4_S
  specific = 4
FEATURE [App::DocumentObjectGroupPython] Cl_element029  label="Cl_element : 015"  # scripted group (container) (typed FeaturePython)
  n = 1
  ref = Cl_element
FEATURE [App::DocumentObjectGroupPython] G4_Cl  # scripted group (container) (typed FeaturePython)
  Dunit = g/cm3
  Dvalue = 0.00299473
  Group = -> [Cl_element029]
  conduct = 2
  density = 1
  expand = 3
  formula = Cl
  name = G4_Cl
  specific = 4
FEATURE [App::DocumentObjectGroupPython] Ar_element002  label="Ar_element : 1"  # scripted group (container) (typed FeaturePython)
  n = 1
  ref = Ar_element
FEATURE [App::DocumentObjectGroupPython] G4_Ar  # scripted group (container) (typed FeaturePython)
  Dunit = g/cm3
  Dvalue = 0.00166201
  Group = -> [Ar_element002]
  conduct = 2
  density = 1
  expand = 3
  formula = Ar
  name = G4_Ar
  specific = 4
FEATURE [App::DocumentObjectGroupPython] K_element013  label="K_element : 003"  # scripted group (container) (typed FeaturePython)
  n = 1
  ref = K_element
FEATURE [App::DocumentObjectGroupPython] G4_K  # scripted group (container) (typed FeaturePython)
  Dunit = g/cm3
  Dvalue = 0.862
  Group = -> [K_element013]
  conduct = 2
  density = 1
  expand = 3
  formula = K
  name = G4_K
  specific = 4
FEATURE [App::DocumentObjectGroupPython] Ca_element014  label="Ca_element : 007"  # scripted group (container) (typed FeaturePython)
  n = 1
  ref = Ca_element
FEATURE [App::DocumentObjectGroupPython] G4_Ca  # scripted group (container) (typed FeaturePython)
  Dunit = g/cm3
  Dvalue = 1.55
  Group = -> [Ca_element014]
  conduct = 2
  density = 1
  expand = 3
  formula = Ca
  name = G4_Ca
  specific = 4
FEATURE [App::DocumentObjectGroupPython] Sc_element001  label="Sc_element : 1"  # scripted group (container) (typed FeaturePython)
  n = 1
  ref = Sc_element
FEATURE [App::DocumentObjectGroupPython] G4_Sc  # scripted group (container) (typed FeaturePython)
  Dunit = g/cm3
  Dvalue = 2.989
  Group = -> [Sc_element001]
  conduct = 2
  density = 1
  expand = 3
  formula = Sc
  name = G4_Sc
  specific = 4
FEATURE [App::DocumentObjectGroupPython] Ti_element004  label="Ti_element : 002"  # scripted group (container) (typed FeaturePython)
  n = 1
  ref = Ti_element
FEATURE [App::DocumentObjectGroupPython] G4_Ti  # scripted group (container) (typed FeaturePython)
  Dunit = g/cm3
  Dvalue = 4.54
  Group = -> [Ti_element004]
  conduct = 2
  density = 1
  expand = 3
  formula = Ti
  name = G4_Ti
  specific = 4
FEATURE [App::DocumentObjectGroupPython] V_element001  label="V_element : 1"  # scripted group (container) (typed FeaturePython)
  n = 1
  ref = V_element
FEATURE [App::DocumentObjectGroupPython] G4_V  # scripted group (container) (typed FeaturePython)
  Dunit = g/cm3
  Dvalue = 6.11
  Group = -> [V_element001]
  conduct = 2
  density = 1
  expand = 3
  formula = V
  name = G4_V
  specific = 4
FEATURE [App::DocumentObjectGroupPython] Cr_element001  label="Cr_element : 1"  # scripted group (container) (typed FeaturePython)
  n = 1
  ref = Cr_element
FEATURE [App::DocumentObjectGroupPython] G4_Cr  # scripted group (container) (typed FeaturePython)
  Dunit = g/cm3
  Dvalue = 7.18
  Group = -> [Cr_element001]
  conduct = 2
  density = 1
  expand = 3
  formula = Cr
  name = G4_Cr
  specific = 4
FEATURE [App::DocumentObjectGroupPython] Mn_element001  label="Mn_element : 1"  # scripted group (container) (typed FeaturePython)
  n = 1
  ref = Mn_element
FEATURE [App::DocumentObjectGroupPython] G4_Mn  # scripted group (container) (typed FeaturePython)
  Dunit = g/cm3
  Dvalue = 7.44
  Group = -> [Mn_element001]
  conduct = 2
  density = 1
  expand = 3
  formula = Mn
  name = G4_Mn
  specific = 4
FEATURE [App::DocumentObjectGroupPython] Fe_element007  label="Fe_element : 004"  # scripted group (container) (typed FeaturePython)
  n = 1
  ref = Fe_element
FEATURE [App::DocumentObjectGroupPython] G4_Fe  # scripted group (container) (typed FeaturePython)
  Dunit = g/cm3
  Dvalue = 7.874
  Group = -> [Fe_element007]
  conduct = 2
  density = 1
  expand = 3
  formula = Fe
  name = G4_Fe
  specific = 4
FEATURE [App::DocumentObjectGroupPython] Co_element001  label="Co_element : 1"  # scripted group (container) (typed FeaturePython)
  n = 1
  ref = Co_element
FEATURE [App::DocumentObjectGroupPython] G4_Co  # scripted group (container) (typed FeaturePython)
  Dunit = g/cm3
  Dvalue = 8.9
  Group = -> [Co_element001]
  conduct = 2
  density = 1
  expand = 3
  formula = Co
  name = G4_Co
  specific = 4
FEATURE [App::DocumentObjectGroupPython] Ni_element001  label="Ni_element : 1"  # scripted group (container) (typed FeaturePython)
  n = 1
  ref = Ni_element
FEATURE [App::DocumentObjectGroupPython] G4_Ni  # scripted group (container) (typed FeaturePython)
  Dunit = g/cm3
  Dvalue = 8.902
  Group = -> [Ni_element001]
  conduct = 2
  density = 1
  expand = 3
  formula = Ni
  name = G4_Ni
  specific = 4
FEATURE [App::DocumentObjectGroupPython] Cu_element001  label="Cu_element : 1"  # scripted group (container) (typed FeaturePython)
  n = 1
  ref = Cu_element
FEATURE [App::DocumentObjectGroupPython] G4_Cu  # scripted group (container) (typed FeaturePython)
  Dunit = g/cm3
  Dvalue = 8.96
  Group = -> [Cu_element001]
  conduct = 2
  density = 1
  expand = 3
  formula = Cu
  name = G4_Cu
  specific = 4
FEATURE [App::DocumentObjectGroupPython] Zn_element001  label="Zn_element : 1"  # scripted group (container) (typed FeaturePython)
  n = 1
  ref = Zn_element
FEATURE [App::DocumentObjectGroupPython] G4_Zn  # scripted group (container) (typed FeaturePython)
  Dunit = g/cm3
  Dvalue = 7.133
  Group = -> [Zn_element001]
  conduct = 2
  density = 1
  expand = 3
  formula = Zn
  name = G4_Zn
  specific = 4
FEATURE [App::DocumentObjectGroupPython] Ga_element002  label="Ga_element : 002"  # scripted group (container) (typed FeaturePython)
  n = 1
  ref = Ga_element
FEATURE [App::DocumentObjectGroupPython] G4_Ga  # scripted group (container) (typed FeaturePython)
  Dunit = g/cm3
  Dvalue = 5.904
  Group = -> [Ga_element002]
  conduct = 2
  density = 1
  expand = 3
  formula = Ga
  name = G4_Ga
  specific = 4
FEATURE [App::DocumentObjectGroupPython] Ge_element002  label="Ge_element : 1"  # scripted group (container) (typed FeaturePython)
  n = 1
  ref = Ge_element
FEATURE [App::DocumentObjectGroupPython] G4_Ge  # scripted group (container) (typed FeaturePython)
  Dunit = g/cm3
  Dvalue = 5.323
  Group = -> [Ge_element002]
  conduct = 2
  density = 1
  expand = 3
  formula = Ge
  name = G4_Ge
  specific = 4
FEATURE [App::DocumentObjectGroupPython] As_element003  label="As_element : 002"  # scripted group (container) (typed FeaturePython)
  n = 1
  ref = As_element
FEATURE [App::DocumentObjectGroupPython] G4_As  # scripted group (container) (typed FeaturePython)
  Dunit = g/cm3
  Dvalue = 5.73
  Group = -> [As_element003]
  conduct = 2
  density = 1
  expand = 3
  formula = As
  name = G4_As
  specific = 4
FEATURE [App::DocumentObjectGroupPython] Se_element001  label="Se_element : 1"  # scripted group (container) (typed FeaturePython)
  n = 1
  ref = Se_element
FEATURE [App::DocumentObjectGroupPython] G4_Se  # scripted group (container) (typed FeaturePython)
  Dunit = g/cm3
  Dvalue = 4.5
  Group = -> [Se_element001]
  conduct = 2
  density = 1
  expand = 3
  formula = Se
  name = G4_Se
  specific = 4
FEATURE [App::DocumentObjectGroupPython] Br_element007  label="Br_element : 004"  # scripted group (container) (typed FeaturePython)
  n = 1
  ref = Br_element
FEATURE [App::DocumentObjectGroupPython] G4_Br  # scripted group (container) (typed FeaturePython)
  Dunit = g/cm3
  Dvalue = 0.0070721
  Group = -> [Br_element007]
  conduct = 2
  density = 1
  expand = 3
  formula = Br
  name = G4_Br
  specific = 4
FEATURE [App::DocumentObjectGroupPython] Kr_element001  label="Kr_element : 1"  # scripted group (container) (typed FeaturePython)
  n = 1
  ref = Kr_element
FEATURE [App::DocumentObjectGroupPython] G4_Kr  # scripted group (container) (typed FeaturePython)
  Dunit = g/cm3
  Dvalue = 0.00347832
  Group = -> [Kr_element001]
  conduct = 2
  density = 1
  expand = 3
  formula = Kr
  name = G4_Kr
  specific = 4
FEATURE [App::DocumentObjectGroupPython] Rb_element001  label="Rb_element : 1"  # scripted group (container) (typed FeaturePython)
  n = 1
  ref = Rb_element
FEATURE [App::DocumentObjectGroupPython] G4_Rb  # scripted group (container) (typed FeaturePython)
  Dunit = g/cm3
  Dvalue = 1.532
  Group = -> [Rb_element001]
  conduct = 2
  density = 1
  expand = 3
  formula = Rb
  name = G4_Rb
  specific = 4
FEATURE [App::DocumentObjectGroupPython] Sr_element001  label="Sr_element : 1"  # scripted group (container) (typed FeaturePython)
  n = 1
  ref = Sr_element
FEATURE [App::DocumentObjectGroupPython] G4_Sr  # scripted group (container) (typed FeaturePython)
  Dunit = g/cm3
  Dvalue = 2.54
  Group = -> [Sr_element001]
  conduct = 2
  density = 1
  expand = 3
  formula = Sr
  name = G4_Sr
  specific = 4
FEATURE [App::DocumentObjectGroupPython] Y_element001  label="Y_element : 1"  # scripted group (container) (typed FeaturePython)
  n = 1
  ref = Y_element
FEATURE [App::DocumentObjectGroupPython] G4_Y  # scripted group (container) (typed FeaturePython)
  Dunit = g/cm3
  Dvalue = 4.469
  Group = -> [Y_element001]
  conduct = 2
  density = 1
  expand = 3
  formula = Y
  name = G4_Y
  specific = 4
FEATURE [App::DocumentObjectGroupPython] Zr_element001  label="Zr_element : 1"  # scripted group (container) (typed FeaturePython)
  n = 1
  ref = Zr_element
FEATURE [App::DocumentObjectGroupPython] G4_Zr  # scripted group (container) (typed FeaturePython)
  Dunit = g/cm3
  Dvalue = 6.506
  Group = -> [Zr_element001]
  conduct = 2
  density = 1
  expand = 3
  formula = Zr
  name = G4_Zr
  specific = 4
FEATURE [App::DocumentObjectGroupPython] Nb_element001  label="Nb_element : 1"  # scripted group (container) (typed FeaturePython)
  n = 1
  ref = Nb_element
FEATURE [App::DocumentObjectGroupPython] G4_Nb  # scripted group (container) (typed FeaturePython)
  Dunit = g/cm3
  Dvalue = 8.57
  Group = -> [Nb_element001]
  conduct = 2
  density = 1
  expand = 3
  formula = Nb
  name = G4_Nb
  specific = 4
FEATURE [App::DocumentObjectGroupPython] Mo_element001  label="Mo_element : 1"  # scripted group (container) (typed FeaturePython)
  n = 1
  ref = Mo_element
FEATURE [App::DocumentObjectGroupPython] G4_Mo  # scripted group (container) (typed FeaturePython)
  Dunit = g/cm3
  Dvalue = 10.22
  Group = -> [Mo_element001]
  conduct = 2
  density = 1
  expand = 3
  formula = Mo
  name = G4_Mo
  specific = 4
FEATURE [App::DocumentObjectGroupPython] Tc_element001  label="Tc_element : 1"  # scripted group (container) (typed FeaturePython)
  n = 1
  ref = Tc_element
FEATURE [App::DocumentObjectGroupPython] G4_Tc  # scripted group (container) (typed FeaturePython)
  Dunit = g/cm3
  Dvalue = 11.5
  Group = -> [Tc_element001]
  conduct = 2
  density = 1
  expand = 3
  formula = Tc
  name = G4_Tc
  specific = 4
FEATURE [App::DocumentObjectGroupPython] Ru_element001  label="Ru_element : 1"  # scripted group (container) (typed FeaturePython)
  n = 1
  ref = Ru_element
FEATURE [App::DocumentObjectGroupPython] G4_Ru  # scripted group (container) (typed FeaturePython)
  Dunit = g/cm3
  Dvalue = 12.41
  Group = -> [Ru_element001]
  conduct = 2
  density = 1
  expand = 3
  formula = Ru
  name = G4_Ru
  specific = 4
FEATURE [App::DocumentObjectGroupPython] Rh_element001  label="Rh_element : 1"  # scripted group (container) (typed FeaturePython)
  n = 1
  ref = Rh_element
FEATURE [App::DocumentObjectGroupPython] G4_Rh  # scripted group (container) (typed FeaturePython)
  Dunit = g/cm3
  Dvalue = 12.41
  Group = -> [Rh_element001]
  conduct = 2
  density = 1
  expand = 3
  formula = Rh
  name = G4_Rh
  specific = 4
FEATURE [App::DocumentObjectGroupPython] Pd_element001  label="Pd_element : 1"  # scripted group (container) (typed FeaturePython)
  n = 1
  ref = Pd_element
FEATURE [App::DocumentObjectGroupPython] G4_Pd  # scripted group (container) (typed FeaturePython)
  Dunit = g/cm3
  Dvalue = 12.02
  Group = -> [Pd_element001]
  conduct = 2
  density = 1
  expand = 3
  formula = Pd
  name = G4_Pd
  specific = 4
FEATURE [App::DocumentObjectGroupPython] Ag_element006  label="Ag_element : 004"  # scripted group (container) (typed FeaturePython)
  n = 1
  ref = Ag_element
FEATURE [App::DocumentObjectGroupPython] G4_Ag  # scripted group (container) (typed FeaturePython)
  Dunit = g/cm3
  Dvalue = 10.5
  Group = -> [Ag_element006]
  conduct = 2
  density = 1
  expand = 3
  formula = Ag
  name = G4_Ag
  specific = 4
FEATURE [App::DocumentObjectGroupPython] Cd_element003  label="Cd_element : 003"  # scripted group (container) (typed FeaturePython)
  n = 1
  ref = Cd_element
FEATURE [App::DocumentObjectGroupPython] G4_Cd  # scripted group (container) (typed FeaturePython)
  Dunit = g/cm3
  Dvalue = 8.65
  Group = -> [Cd_element003]
  conduct = 2
  density = 1
  expand = 3
  formula = Cd
  name = G4_Cd
  specific = 4
FEATURE [App::DocumentObjectGroupPython] In_element001  label="In_element : 1"  # scripted group (container) (typed FeaturePython)
  n = 1
  ref = In_element
FEATURE [App::DocumentObjectGroupPython] G4_In  # scripted group (container) (typed FeaturePython)
  Dunit = g/cm3
  Dvalue = 7.31
  Group = -> [In_element001]
  conduct = 2
  density = 1
  expand = 3
  formula = In
  name = G4_In
  specific = 4
FEATURE [App::DocumentObjectGroupPython] Sn_element001  label="Sn_element : 1"  # scripted group (container) (typed FeaturePython)
  n = 1
  ref = Sn_element
FEATURE [App::DocumentObjectGroupPython] G4_Sn  # scripted group (container) (typed FeaturePython)
  Dunit = g/cm3
  Dvalue = 7.31
  Group = -> [Sn_element001]
  conduct = 2
  density = 1
  expand = 3
  formula = Sn
  name = G4_Sn
  specific = 4
FEATURE [App::DocumentObjectGroupPython] Sb_element001  label="Sb_element : 1"  # scripted group (container) (typed FeaturePython)
  n = 1
  ref = Sb_element
FEATURE [App::DocumentObjectGroupPython] G4_Sb  # scripted group (container) (typed FeaturePython)
  Dunit = g/cm3
  Dvalue = 6.691
  Group = -> [Sb_element001]
  conduct = 2
  density = 1
  expand = 3
  formula = Sb
  name = G4_Sb
  specific = 4
FEATURE [App::DocumentObjectGroupPython] Te_element002  label="Te_element : 002"  # scripted group (container) (typed FeaturePython)
  n = 1
  ref = Te_element
FEATURE [App::DocumentObjectGroupPython] G4_Te  # scripted group (container) (typed FeaturePython)
  Dunit = g/cm3
  Dvalue = 6.24
  Group = -> [Te_element002]
  conduct = 2
  density = 1
  expand = 3
  formula = Te
  name = G4_Te
  specific = 4
FEATURE [App::DocumentObjectGroupPython] I_element010  label="I_element : 006"  # scripted group (container) (typed FeaturePython)
  n = 1
  ref = I_element
FEATURE [App::DocumentObjectGroupPython] G4_I  # scripted group (container) (typed FeaturePython)
  Dunit = g/cm3
  Dvalue = 4.93
  Group = -> [I_element010]
  conduct = 2
  density = 1
  expand = 3
  formula = I
  name = G4_I
  specific = 4
FEATURE [App::DocumentObjectGroupPython] Xe_element001  label="Xe_element : 1"  # scripted group (container) (typed FeaturePython)
  n = 1
  ref = Xe_element
FEATURE [App::DocumentObjectGroupPython] G4_Xe  # scripted group (container) (typed FeaturePython)
  Dunit = g/cm3
  Dvalue = 0.00548536
  Group = -> [Xe_element001]
  conduct = 2
  density = 1
  expand = 3
  formula = Xe
  name = G4_Xe
  specific = 4
FEATURE [App::DocumentObjectGroupPython] Cs_element003  label="Cs_element : 003"  # scripted group (container) (typed FeaturePython)
  n = 1
  ref = Cs_element
FEATURE [App::DocumentObjectGroupPython] G4_Cs  # scripted group (container) (typed FeaturePython)
  Dunit = g/cm3
  Dvalue = 1.873
  Group = -> [Cs_element003]
  conduct = 2
  density = 1
  expand = 3
  formula = Cs
  name = G4_Cs
  specific = 4
FEATURE [App::DocumentObjectGroupPython] Ba_element003  label="Ba_element : 003"  # scripted group (container) (typed FeaturePython)
  n = 1
  ref = Ba_element
FEATURE [App::DocumentObjectGroupPython] G4_Ba  # scripted group (container) (typed FeaturePython)
  Dunit = g/cm3
  Dvalue = 3.5
  Group = -> [Ba_element003]
  conduct = 2
  density = 1
  expand = 3
  formula = Ba
  name = G4_Ba
  specific = 4
FEATURE [App::DocumentObjectGroupPython] La_element003  label="La_element : 003"  # scripted group (container) (typed FeaturePython)
  n = 1
  ref = La_element
FEATURE [App::DocumentObjectGroupPython] G4_La  # scripted group (container) (typed FeaturePython)
  Dunit = g/cm3
  Dvalue = 6.154
  Group = -> [La_element003]
  conduct = 2
  density = 1
  expand = 3
  formula = La
  name = G4_La
  specific = 4
FEATURE [App::DocumentObjectGroupPython] Ce_element002  label="Ce_element : 1"  # scripted group (container) (typed FeaturePython)
  n = 1
  ref = Ce_element
FEATURE [App::DocumentObjectGroupPython] G4_Ce  # scripted group (container) (typed FeaturePython)
  Dunit = g/cm3
  Dvalue = 6.657
  Group = -> [Ce_element002]
  conduct = 2
  density = 1
  expand = 3
  formula = Ce
  name = G4_Ce
  specific = 4
FEATURE [App::DocumentObjectGroupPython] Pr_element001  label="Pr_element : 1"  # scripted group (container) (typed FeaturePython)
  n = 1
  ref = Pr_element
FEATURE [App::DocumentObjectGroupPython] G4_Pr  # scripted group (container) (typed FeaturePython)
  Dunit = g/cm3
  Dvalue = 6.71
  Group = -> [Pr_element001]
  conduct = 2
  density = 1
  expand = 3
  formula = Pr
  name = G4_Pr
  specific = 4
FEATURE [App::DocumentObjectGroupPython] Nd_element001  label="Nd_element : 1"  # scripted group (container) (typed FeaturePython)
  n = 1
  ref = Nd_element
FEATURE [App::DocumentObjectGroupPython] G4_Nd  # scripted group (container) (typed FeaturePython)
  Dunit = g/cm3
  Dvalue = 6.9
  Group = -> [Nd_element001]
  conduct = 2
  density = 1
  expand = 3
  formula = Nd
  name = G4_Nd
  specific = 4
FEATURE [App::DocumentObjectGroupPython] Pm_element001  label="Pm_element : 1"  # scripted group (container) (typed FeaturePython)
  n = 1
  ref = Pm_element
FEATURE [App::DocumentObjectGroupPython] G4_Pm  # scripted group (container) (typed FeaturePython)
  Dunit = g/cm3
  Dvalue = 7.22
  Group = -> [Pm_element001]
  conduct = 2
  density = 1
  expand = 3
  formula = Pm
  name = G4_Pm
  specific = 4
FEATURE [App::DocumentObjectGroupPython] Sm_element001  label="Sm_element : 1"  # scripted group (container) (typed FeaturePython)
  n = 1
  ref = Sm_element
FEATURE [App::DocumentObjectGroupPython] G4_Sm  # scripted group (container) (typed FeaturePython)
  Dunit = g/cm3
  Dvalue = 7.46
  Group = -> [Sm_element001]
  conduct = 2
  density = 1
  expand = 3
  formula = Sm
  name = G4_Sm
  specific = 4
FEATURE [App::DocumentObjectGroupPython] Eu_element001  label="Eu_element : 1"  # scripted group (container) (typed FeaturePython)
  n = 1
  ref = Eu_element
FEATURE [App::DocumentObjectGroupPython] G4_Eu  # scripted group (container) (typed FeaturePython)
  Dunit = g/cm3
  Dvalue = 5.243
  Group = -> [Eu_element001]
  conduct = 2
  density = 1
  expand = 3
  formula = Eu
  name = G4_Eu
  specific = 4
FEATURE [App::DocumentObjectGroupPython] Gd_element002  label="Gd_element : 1"  # scripted group (container) (typed FeaturePython)
  n = 1
  ref = Gd_element
FEATURE [App::DocumentObjectGroupPython] G4_Gd  # scripted group (container) (typed FeaturePython)
  Dunit = g/cm3
  Dvalue = 7.9004
  Group = -> [Gd_element002]
  conduct = 2
  density = 1
  expand = 3
  formula = Gd
  name = G4_Gd
  specific = 4
FEATURE [App::DocumentObjectGroupPython] Tb_element001  label="Tb_element : 1"  # scripted group (container) (typed FeaturePython)
  n = 1
  ref = Tb_element
FEATURE [App::DocumentObjectGroupPython] G4_Tb  # scripted group (container) (typed FeaturePython)
  Dunit = g/cm3
  Dvalue = 8.229
  Group = -> [Tb_element001]
  conduct = 2
  density = 1
  expand = 3
  formula = Tb
  name = G4_Tb
  specific = 4
FEATURE [App::DocumentObjectGroupPython] Dy_element001  label="Dy_element : 1"  # scripted group (container) (typed FeaturePython)
  n = 1
  ref = Dy_element
FEATURE [App::DocumentObjectGroupPython] G4_Dy  # scripted group (container) (typed FeaturePython)
  Dunit = g/cm3
  Dvalue = 8.55
  Group = -> [Dy_element001]
  conduct = 2
  density = 1
  expand = 3
  formula = Dy
  name = G4_Dy
  specific = 4
FEATURE [App::DocumentObjectGroupPython] Ho_element001  label="Ho_element : 1"  # scripted group (container) (typed FeaturePython)
  n = 1
  ref = Ho_element
FEATURE [App::DocumentObjectGroupPython] G4_Ho  # scripted group (container) (typed FeaturePython)
  Dunit = g/cm3
  Dvalue = 8.795
  Group = -> [Ho_element001]
  conduct = 2
  density = 1
  expand = 3
  formula = Ho
  name = G4_Ho
  specific = 4
FEATURE [App::DocumentObjectGroupPython] Er_element001  label="Er_element : 1"  # scripted group (container) (typed FeaturePython)
  n = 1
  ref = Er_element
FEATURE [App::DocumentObjectGroupPython] G4_Er  # scripted group (container) (typed FeaturePython)
  Dunit = g/cm3
  Dvalue = 9.066
  Group = -> [Er_element001]
  conduct = 2
  density = 1
  expand = 3
  formula = Er
  name = G4_Er
  specific = 4
FEATURE [App::DocumentObjectGroupPython] Tm_element001  label="Tm_element : 1"  # scripted group (container) (typed FeaturePython)
  n = 1
  ref = Tm_element
FEATURE [App::DocumentObjectGroupPython] G4_Tm  # scripted group (container) (typed FeaturePython)
  Dunit = g/cm3
  Dvalue = 9.321
  Group = -> [Tm_element001]
  conduct = 2
  density = 1
  expand = 3
  formula = Tm
  name = G4_Tm
  specific = 4
FEATURE [App::DocumentObjectGroupPython] Yb_element001  label="Yb_element : 1"  # scripted group (container) (typed FeaturePython)
  n = 1
  ref = Yb_element
FEATURE [App::DocumentObjectGroupPython] G4_Yb  # scripted group (container) (typed FeaturePython)
  Dunit = g/cm3
  Dvalue = 6.73
  Group = -> [Yb_element001]
  conduct = 2
  density = 1
  expand = 3
  formula = Yb
  name = G4_Yb
  specific = 4
FEATURE [App::DocumentObjectGroupPython] Lu_element001  label="Lu_element : 1"  # scripted group (container) (typed FeaturePython)
  n = 1
  ref = Lu_element
FEATURE [App::DocumentObjectGroupPython] G4_Lu  # scripted group (container) (typed FeaturePython)
  Dunit = g/cm3
  Dvalue = 9.84
  Group = -> [Lu_element001]
  conduct = 2
  density = 1
  expand = 3
  formula = Lu
  name = G4_Lu
  specific = 4
FEATURE [App::DocumentObjectGroupPython] Hf_element001  label="Hf_element : 1"  # scripted group (container) (typed FeaturePython)
  n = 1
  ref = Hf_element
FEATURE [App::DocumentObjectGroupPython] G4_Hf  # scripted group (container) (typed FeaturePython)
  Dunit = g/cm3
  Dvalue = 13.31
  Group = -> [Hf_element001]
  conduct = 2
  density = 1
  expand = 3
  formula = Hf
  name = G4_Hf
  specific = 4
FEATURE [App::DocumentObjectGroupPython] Ta_element001  label="Ta_element : 1"  # scripted group (container) (typed FeaturePython)
  n = 1
  ref = Ta_element
FEATURE [App::DocumentObjectGroupPython] G4_Ta  # scripted group (container) (typed FeaturePython)
  Dunit = g/cm3
  Dvalue = 16.654
  Group = -> [Ta_element001]
  conduct = 2
  density = 1
  expand = 3
  formula = Ta
  name = G4_Ta
  specific = 4
FEATURE [App::DocumentObjectGroupPython] W_element004  label="W_element : 004"  # scripted group (container) (typed FeaturePython)
  n = 1
  ref = W_element
FEATURE [App::DocumentObjectGroupPython] G4_W  # scripted group (container) (typed FeaturePython)
  Dunit = g/cm3
  Dvalue = 19.3
  Group = -> [W_element004]
  conduct = 2
  density = 1
  expand = 3
  formula = W
  name = G4_W
  specific = 4
FEATURE [App::DocumentObjectGroupPython] Re_element001  label="Re_element : 1"  # scripted group (container) (typed FeaturePython)
  n = 1
  ref = Re_element
FEATURE [App::DocumentObjectGroupPython] G4_Re  # scripted group (container) (typed FeaturePython)
  Dunit = g/cm3
  Dvalue = 21.02
  Group = -> [Re_element001]
  conduct = 2
  density = 1
  expand = 3
  formula = Re
  name = G4_Re
  specific = 4
FEATURE [App::DocumentObjectGroupPython] Os_element001  label="Os_element : 1"  # scripted group (container) (typed FeaturePython)
  n = 1
  ref = Os_element
FEATURE [App::DocumentObjectGroupPython] G4_Os  # scripted group (container) (typed FeaturePython)
  Dunit = g/cm3
  Dvalue = 22.57
  Group = -> [Os_element001]
  conduct = 2
  density = 1
  expand = 3
  formula = Os
  name = G4_Os
  specific = 4
FEATURE [App::DocumentObjectGroupPython] Ir_element001  label="Ir_element : 1"  # scripted group (container) (typed FeaturePython)
  n = 1
  ref = Ir_element
FEATURE [App::DocumentObjectGroupPython] G4_Ir  # scripted group (container) (typed FeaturePython)
  Dunit = g/cm3
  Dvalue = 22.42
  Group = -> [Ir_element001]
  conduct = 2
  density = 1
  expand = 3
  formula = Ir
  name = G4_Ir
  specific = 4
FEATURE [App::DocumentObjectGroupPython] Pt_element001  label="Pt_element : 1"  # scripted group (container) (typed FeaturePython)
  n = 1
  ref = Pt_element
FEATURE [App::DocumentObjectGroupPython] G4_Pt  # scripted group (container) (typed FeaturePython)
  Dunit = g/cm3
  Dvalue = 21.45
  Group = -> [Pt_element001]
  conduct = 2
  density = 1
  expand = 3
  formula = Pt
  name = G4_Pt
  specific = 4
FEATURE [App::DocumentObjectGroupPython] Au_element001  label="Au_element : 1"  # scripted group (container) (typed FeaturePython)
  n = 1
  ref = Au_element
FEATURE [App::DocumentObjectGroupPython] G4_Au  # scripted group (container) (typed FeaturePython)
  Dunit = g/cm3
  Dvalue = 19.32
  Group = -> [Au_element001]
  conduct = 2
  density = 1
  expand = 3
  formula = Au
  name = G4_Au
  specific = 4
FEATURE [App::DocumentObjectGroupPython] Hg_element002  label="Hg_element : 002"  # scripted group (container) (typed FeaturePython)
  n = 1
  ref = Hg_element
FEATURE [App::DocumentObjectGroupPython] G4_Hg  # scripted group (container) (typed FeaturePython)
  Dunit = g/cm3
  Dvalue = 13.546
  Group = -> [Hg_element002]
  conduct = 2
  density = 1
  expand = 3
  formula = Hg
  name = G4_Hg
  specific = 4
FEATURE [App::DocumentObjectGroupPython] Tl_element002  label="Tl_element : 002"  # scripted group (container) (typed FeaturePython)
  n = 1
  ref = Tl_element
FEATURE [App::DocumentObjectGroupPython] G4_Tl  # scripted group (container) (typed FeaturePython)
  Dunit = g/cm3
  Dvalue = 11.72
  Group = -> [Tl_element002]
  conduct = 2
  density = 1
  expand = 3
  formula = Tl
  name = G4_Tl
  specific = 4
FEATURE [App::DocumentObjectGroupPython] Pb_element003  label="Pb_element : 1"  # scripted group (container) (typed FeaturePython)
  n = 1
  ref = Pb_element
FEATURE [App::DocumentObjectGroupPython] G4_Pb  # scripted group (container) (typed FeaturePython)
  Dunit = g/cm3
  Dvalue = 11.35
  Group = -> [Pb_element003]
  conduct = 2
  density = 1
  expand = 3
  formula = Pb
  name = G4_Pb
  specific = 4
FEATURE [App::DocumentObjectGroupPython] Bi_element002  label="Bi_element : 1"  # scripted group (container) (typed FeaturePython)
  n = 1
  ref = Bi_element
FEATURE [App::DocumentObjectGroupPython] G4_Bi  # scripted group (container) (typed FeaturePython)
  Dunit = g/cm3
  Dvalue = 9.747
  Group = -> [Bi_element002]
  conduct = 2
  density = 1
  expand = 3
  formula = Bi
  name = G4_Bi
  specific = 4
FEATURE [App::DocumentObjectGroupPython] Po_element001  label="Po_element : 1"  # scripted group (container) (typed FeaturePython)
  n = 1
  ref = Po_element
FEATURE [App::DocumentObjectGroupPython] G4_Po  # scripted group (container) (typed FeaturePython)
  Dunit = g/cm3
  Dvalue = 9.32
  Group = -> [Po_element001]
  conduct = 2
  density = 1
  expand = 3
  formula = Po
  name = G4_Po
  specific = 4
FEATURE [App::DocumentObjectGroupPython] At_element001  label="At_element : 1"  # scripted group (container) (typed FeaturePython)
  n = 1
  ref = At_element
FEATURE [App::DocumentObjectGroupPython] G4_At  # scripted group (container) (typed FeaturePython)
  Dunit = g/cm3
  Dvalue = 9.32
  Group = -> [At_element001]
  conduct = 2
  density = 1
  expand = 3
  formula = At
  name = G4_At
  specific = 4
FEATURE [App::DocumentObjectGroupPython] Rn_element001  label="Rn_element : 1"  # scripted group (container) (typed FeaturePython)
  n = 1
  ref = Rn_element
FEATURE [App::DocumentObjectGroupPython] G4_Rn  # scripted group (container) (typed FeaturePython)
  Dunit = g/cm3
  Dvalue = 0.00900662
  Group = -> [Rn_element001]
  conduct = 2
  density = 1
  expand = 3
  formula = Rn
  name = G4_Rn
  specific = 4
FEATURE [App::DocumentObjectGroupPython] Fr_element001  label="Fr_element : 1"  # scripted group (container) (typed FeaturePython)
  n = 1
  ref = Fr_element
FEATURE [App::DocumentObjectGroupPython] G4_Fr  # scripted group (container) (typed FeaturePython)
  Dunit = g/cm3
  Dvalue = 1
  Group = -> [Fr_element001]
  conduct = 2
  density = 1
  expand = 3
  formula = Fr
  name = G4_Fr
  specific = 4
FEATURE [App::DocumentObjectGroupPython] Ra_element001  label="Ra_element : 1"  # scripted group (container) (typed FeaturePython)
  n = 1
  ref = Ra_element
FEATURE [App::DocumentObjectGroupPython] G4_Ra  # scripted group (container) (typed FeaturePython)
  Dunit = g/cm3
  Dvalue = 5
  Group = -> [Ra_element001]
  conduct = 2
  density = 1
  expand = 3
  formula = Ra
  name = G4_Ra
  specific = 4
FEATURE [App::DocumentObjectGroupPython] Ac_element001  label="Ac_element : 1"  # scripted group (container) (typed FeaturePython)
  n = 1
  ref = Ac_element
FEATURE [App::DocumentObjectGroupPython] G4_Ac  # scripted group (container) (typed FeaturePython)
  Dunit = g/cm3
  Dvalue = 10.07
  Group = -> [Ac_element001]
  conduct = 2
  density = 1
  expand = 3
  formula = Ac
  name = G4_Ac
  specific = 4
FEATURE [App::DocumentObjectGroupPython] Th_element001  label="Th_element : 1"  # scripted group (container) (typed FeaturePython)
  n = 1
  ref = Th_element
FEATURE [App::DocumentObjectGroupPython] G4_Th  # scripted group (container) (typed FeaturePython)
  Dunit = g/cm3
  Dvalue = 11.72
  Group = -> [Th_element001]
  conduct = 2
  density = 1
  expand = 3
  formula = Th
  name = G4_Th
  specific = 4
FEATURE [App::DocumentObjectGroupPython] Pa_element001  label="Pa_element : 1"  # scripted group (container) (typed FeaturePython)
  n = 1
  ref = Pa_element
FEATURE [App::DocumentObjectGroupPython] G4_Pa  # scripted group (container) (typed FeaturePython)
  Dunit = g/cm3
  Dvalue = 15.37
  Group = -> [Pa_element001]
  conduct = 2
  density = 1
  expand = 3
  formula = Pa
  name = G4_Pa
  specific = 4
FEATURE [App::DocumentObjectGroupPython] U_element004  label="U_element : 004"  # scripted group (container) (typed FeaturePython)
  n = 1
  ref = U_element
FEATURE [App::DocumentObjectGroupPython] G4_U  # scripted group (container) (typed FeaturePython)
  Dunit = g/cm3
  Dvalue = 18.95
  Group = -> [U_element004]
  conduct = 2
  density = 1
  expand = 3
  formula = U
  name = G4_U
  specific = 4
FEATURE [App::DocumentObjectGroupPython] Np_element001  label="Np_element : 1"  # scripted group (container) (typed FeaturePython)
  n = 1
  ref = Np_element
FEATURE [App::DocumentObjectGroupPython] G4_Np  # scripted group (container) (typed FeaturePython)
  Dunit = g/cm3
  Dvalue = 20.25
  Group = -> [Np_element001]
  conduct = 2
  density = 1
  expand = 3
  formula = Np
  name = G4_Np
  specific = 4
FEATURE [App::DocumentObjectGroupPython] Pu_element002  label="Pu_element : 002"  # scripted group (container) (typed FeaturePython)
  n = 1
  ref = Pu_element
FEATURE [App::DocumentObjectGroupPython] G4_Pu  # scripted group (container) (typed FeaturePython)
  Dunit = g/cm3
  Dvalue = 19.84
  Group = -> [Pu_element002]
  conduct = 2
  density = 1
  expand = 3
  formula = Pu
  name = G4_Pu
  specific = 4
FEATURE [App::DocumentObjectGroupPython] Am_element001  label="Am_element : 1"  # scripted group (container) (typed FeaturePython)
  n = 1
  ref = Am_element
FEATURE [App::DocumentObjectGroupPython] G4_Am  # scripted group (container) (typed FeaturePython)
  Dunit = g/cm3
  Dvalue = 13.67
  Group = -> [Am_element001]
  conduct = 2
  density = 1
  expand = 3
  formula = Am
  name = G4_Am
  specific = 4
FEATURE [App::DocumentObjectGroupPython] Cm_element001  label="Cm_element : 1"  # scripted group (container) (typed FeaturePython)
  n = 1
  ref = Cm_element
FEATURE [App::DocumentObjectGroupPython] G4_Cm  # scripted group (container) (typed FeaturePython)
  Dunit = g/cm3
  Dvalue = 13.51
  Group = -> [Cm_element001]
  conduct = 2
  density = 1
  expand = 3
  formula = Cm
  name = G4_Cm
  specific = 4
FEATURE [App::DocumentObjectGroupPython] Bk_element001  label="Bk_element : 1"  # scripted group (container) (typed FeaturePython)
  n = 1
  ref = Bk_element
FEATURE [App::DocumentObjectGroupPython] G4_Bk  # scripted group (container) (typed FeaturePython)
  Dunit = g/cm3
  Dvalue = 14
  Group = -> [Bk_element001]
  conduct = 2
  density = 1
  expand = 3
  formula = Bk
  name = G4_Bk
  specific = 4
FEATURE [App::DocumentObjectGroupPython] Cf_element001  label="Cf_element : 1"  # scripted group (container) (typed FeaturePython)
  n = 1
  ref = Cf_element
FEATURE [App::DocumentObjectGroupPython] G4_Cf  # scripted group (container) (typed FeaturePython)
  Dunit = g/cm3
  Dvalue = 10
  Group = -> [Cf_element001]
  conduct = 2
  density = 1
  expand = 3
  formula = Cf
  name = G4_Cf
  specific = 4
FEATURE [App::DocumentObjectGroupPython] Element  # scripted group (container) (typed FeaturePython)
  Group = -> [G4_H,G4_He,G4_Li,G4_Be,G4_B,G4_C,G4_N,G4_O,G4_F,G4_Ne,G4_Na,G4_Mg,G4_Al,G4_Si,G4_P,G4_S,G4_Cl,G4_Ar,G4_K,G4_Ca,G4_Sc,G4_Ti,G4_V,G4_Cr,G4_Mn,G4_Fe,G4_Co,G4_Ni,G4_Cu,G4_Zn,G4_Ga,G4_Ge,G4_As,G4_Se,G4_Br,G4_Kr,G4_Rb,G4_Sr,G4_Y,G4_Zr,G4_Nb,G4_Mo,G4_Tc,G4_Ru,G4_Rh,G4_Pd,G4_Ag,G4_Cd,G4_In,G4_Sn,G4_Sb,G4_Te,G4_I,G4_Xe,G4_Cs,G4_Ba,G4_La,G4_Ce,G4_Pr,G4_Nd,G4_Pm,G4_Sm,G4_Eu,G4_Gd,G4_Tb,G4_Dy,G4_Ho,G4_Er,+30 more]
FEATURE [App::DocumentObjectGroupPython] H_element114  label="H_element : 063"  # scripted group (container) (typed FeaturePython)
  n = 2
  ref = H_element
FEATURE [App::DocumentObjectGroupPython] G4_lH2  # scripted group (container) (typed FeaturePython)
  Dunit = g/cm3
  Dvalue = 0.0708
  Group = -> [H_element114]
  conduct = 2
  density = 1
  expand = 3
  formula = G4_lH2
  name = G4_lH2
  specific = 4
FEATURE [App::DocumentObjectGroupPython] N_element049  label="N_element : 022"  # scripted group (container) (typed FeaturePython)
  n = 2
  ref = N_element
FEATURE [App::DocumentObjectGroupPython] G4_lN2  # scripted group (container) (typed FeaturePython)
  Dunit = g/cm3
  Dvalue = 0.807
  Group = -> [N_element049]
  conduct = 2
  density = 1
  expand = 3
  formula = G4_lN2
  name = G4_lN2
  specific = 4
FEATURE [App::DocumentObjectGroupPython] O_element106  label="O_element : 060"  # scripted group (container) (typed FeaturePython)
  n = 2
  ref = O_element
FEATURE [App::DocumentObjectGroupPython] G4_lO2  # scripted group (container) (typed FeaturePython)
  Dunit = g/cm3
  Dvalue = 1.141
  Group = -> [O_element106]
  conduct = 2
  density = 1
  expand = 3
  formula = G4_lO2
  name = G4_lO2
  specific = 4
FEATURE [App::DocumentObjectGroupPython] Ar  label="Ar : 1"  # scripted group (container) (typed FeaturePython)
  n = 1
  ref = Ar
FEATURE [App::DocumentObjectGroupPython] G4_lAr  # scripted group (container) (typed FeaturePython)
  Dunit = g/cm3
  Dvalue = 1.396
  Group = -> [Ar]
  conduct = 2
  density = 1
  expand = 3
  formula = G4_lAr
  name = G4_lAr
  specific = 4
FEATURE [App::DocumentObjectGroupPython] Br  label="Br : 1"  # scripted group (container) (typed FeaturePython)
  n = 1
  ref = Br
FEATURE [App::DocumentObjectGroupPython] G4_lBr  # scripted group (container) (typed FeaturePython)
  Dunit = g/cm3
  Dvalue = 3.1028
  Group = -> [Br]
  conduct = 2
  density = 1
  expand = 3
  formula = G4_lBr
  name = G4_lBr
  specific = 4
FEATURE [App::DocumentObjectGroupPython] Kr  label="Kr : 1"  # scripted group (container) (typed FeaturePython)
  n = 1
  ref = Kr
FEATURE [App::DocumentObjectGroupPython] G4_lKr  # scripted group (container) (typed FeaturePython)
  Dunit = g/cm3
  Dvalue = 2.418
  Group = -> [Kr]
  conduct = 2
  density = 1
  expand = 3
  formula = G4_lKr
  name = G4_lKr
  specific = 4
FEATURE [App::DocumentObjectGroupPython] Xe  label="Xe : 1"  # scripted group (container) (typed FeaturePython)
  n = 1
  ref = Xe
FEATURE [App::DocumentObjectGroupPython] G4_lXe  # scripted group (container) (typed FeaturePython)
  Dunit = g/cm3
  Dvalue = 2.953
  Group = -> [Xe]
  conduct = 2
  density = 1
  expand = 3
  formula = G4_lXe
  name = G4_lXe
  specific = 4
FEATURE [App::DocumentObjectGroupPython] O_element107  label="O_element : 061"  # scripted group (container) (typed FeaturePython)
  n = 4
  ref = O_element
FEATURE [App::DocumentObjectGroupPython] Pb_element004  label="Pb_element : 002"  # scripted group (container) (typed FeaturePython)
  n = 1
  ref = Pb_element
FEATURE [App::DocumentObjectGroupPython] W_element005  label="W_element : 005"  # scripted group (container) (typed FeaturePython)
  n = 1
  ref = W_element
FEATURE [App::DocumentObjectGroupPython] G4_PbWO4  # scripted group (container) (typed FeaturePython)
  Dunit = g/cm3
  Dvalue = 8.28
  Group = -> [O_element107,Pb_element004,W_element005]
  conduct = 2
  density = 1
  expand = 3
  formula = G4_PbWO4
  name = G4_PbWO4
  specific = 4
FEATURE [App::DocumentObjectGroupPython] alactic  label="alactic : 1"  # scripted group (container) (typed FeaturePython)
  n = 1
  ref = alactic
FEATURE [App::DocumentObjectGroupPython] G4_Galactic  # scripted group (container) (typed FeaturePython)
  Dunit = g/cm3
  Dvalue = 0
  Group = -> [alactic]
  conduct = 2
  density = 1
  expand = 3
  formula = G4_Galactic
  name = G4_Galactic
  specific = 4
FEATURE [App::DocumentObjectGroupPython] RAPHITE_POROUS  label="RAPHITE_POROUS : 1"  # scripted group (container) (typed FeaturePython)
  n = 1
  ref = RAPHITE_POROUS
FEATURE [App::DocumentObjectGroupPython] G4_GRAPHITE_POROUS  # scripted group (container) (typed FeaturePython)
  Dunit = g/cm3
  Dvalue = 1.7
  Group = -> [RAPHITE_POROUS]
  conduct = 2
  density = 1
  expand = 3
  formula = G4_GRAPHITE_POROUS
  name = G4_GRAPHITE_POROUS
  specific = 4
FEATURE [App::DocumentObjectGroupPython] H_element115  label="H_element : 0.150"  # scripted group (container) (typed FeaturePython)
  n = 0.080538
FEATURE [App::DocumentObjectGroupPython] C_element125  label="C_element : 0.600"  # scripted group (container) (typed FeaturePython)
  n = 0.599848
FEATURE [App::DocumentObjectGroupPython] O_element108  label="O_element : 0.320"  # scripted group (container) (typed FeaturePython)
  n = 0.319614
FEATURE [App::DocumentObjectGroupPython] G4_LUCITE  # scripted group (container) (typed FeaturePython)
  Dunit = g/cm3
  Dvalue = 1.19
  Group = -> [H_element115,C_element125,O_element108]
  conduct = 2
  density = 1
  expand = 3
  formula = G4_LUCITE
  name = G4_LUCITE
  specific = 4
FEATURE [App::DocumentObjectGroupPython] Cu_element002  label="Cu_element : 62"  # scripted group (container) (typed FeaturePython)
  n = 62
  ref = Cu_element
FEATURE [App::DocumentObjectGroupPython] Zn_element002  label="Zn_element : 35"  # scripted group (container) (typed FeaturePython)
  n = 35
  ref = Zn_element
FEATURE [App::DocumentObjectGroupPython] Pb_element005  label="Pb_element : 3"  # scripted group (container) (typed FeaturePython)
  n = 3
  ref = Pb_element
FEATURE [App::DocumentObjectGroupPython] G4_BRASS  # scripted group (container) (typed FeaturePython)
  Dunit = g/cm3
  Dvalue = 8.52
  Group = -> [Cu_element002,Zn_element002,Pb_element005]
  conduct = 2
  density = 1
  expand = 3
  formula = G4_BRASS
  name = G4_BRASS
  specific = 4
FEATURE [App::DocumentObjectGroupPython] Cu_element003  label="Cu_element : 89"  # scripted group (container) (typed FeaturePython)
  n = 89
  ref = Cu_element
FEATURE [App::DocumentObjectGroupPython] Zn_element003  label="Zn_element : 9"  # scripted group (container) (typed FeaturePython)
  n = 9
  ref = Zn_element
FEATURE [App::DocumentObjectGroupPython] Pb_element006  label="Pb_element : 2"  # scripted group (container) (typed FeaturePython)
  n = 2
  ref = Pb_element
FEATURE [App::DocumentObjectGroupPython] G4_BRONZE  # scripted group (container) (typed FeaturePython)
  Dunit = g/cm3
  Dvalue = 8.82
  Group = -> [Cu_element003,Zn_element003,Pb_element006]
  conduct = 2
  density = 1
  expand = 3
  formula = G4_BRONZE
  name = G4_BRONZE
  specific = 4
FEATURE [App::DocumentObjectGroupPython] Fe_element008  label="Fe_element : 74"  # scripted group (container) (typed FeaturePython)
  n = 74
  ref = Fe_element
FEATURE [App::DocumentObjectGroupPython] Cr_element002  label="Cr_element : 18"  # scripted group (container) (typed FeaturePython)
  n = 18
  ref = Cr_element
FEATURE [App::DocumentObjectGroupPython] Ni_element002  label="Ni_element : 8"  # scripted group (container) (typed FeaturePython)
  n = 8
  ref = Ni_element
FEATURE [App::DocumentObjectGroupPython] G4_STAINLESS_STEEL  label="G4_STAINLESS-STEEL"  # scripted group (container) (typed FeaturePython)
  Dunit = g/cm3
  Dvalue = 8
  Group = -> [Fe_element008,Cr_element002,Ni_element002]
  conduct = 2
  density = 1
  expand = 3
  formula = G4_STAINLESS-STEEL
  name = G4_STAINLESS-STEEL
  specific = 4
FEATURE [App::DocumentObjectGroupPython] H_element116  label="H_element : 064"  # scripted group (container) (typed FeaturePython)
  n = 18
  ref = H_element
FEATURE [App::DocumentObjectGroupPython] C_element126  label="C_element : 071"  # scripted group (container) (typed FeaturePython)
  n = 12
  ref = C_element
FEATURE [App::DocumentObjectGroupPython] O_element109  label="O_element : 062"  # scripted group (container) (typed FeaturePython)
  n = 7
  ref = O_element
FEATURE [App::DocumentObjectGroupPython] G4_CR39  # scripted group (container) (typed FeaturePython)
  Dunit = g/cm3
  Dvalue = 1.32
  Group = -> [H_element116,C_element126,O_element109]
  conduct = 2
  density = 1
  expand = 3
  formula = G4_CR39
  name = G4_CR39
  specific = 4
FEATURE [App::DocumentObjectGroupPython] H_element117  label="H_element : 38"  # scripted group (container) (typed FeaturePython)
  n = 38
  ref = H_element
FEATURE [App::DocumentObjectGroupPython] C_element127  label="C_element : 072"  # scripted group (container) (typed FeaturePython)
  n = 18
  ref = C_element
FEATURE [App::DocumentObjectGroupPython] O_element110  label="O_element : 063"  # scripted group (container) (typed FeaturePython)
  n = 1
  ref = O_element
FEATURE [App::DocumentObjectGroupPython] G4_OCTADECANOL  # scripted group (container) (typed FeaturePython)
  Dunit = g/cm3
  Dvalue = 0.812
  Group = -> [H_element117,C_element127,O_element110]
  conduct = 2
  density = 1
  expand = 3
  formula = G4_OCTADECANOL
  name = G4_OCTADECANOL
  specific = 4
FEATURE [App::DocumentObjectGroupPython] HEP  # scripted group (container) (typed FeaturePython)
  Group = -> [G4_lH2,G4_lN2,G4_lO2,G4_lAr,G4_lBr,G4_lKr,G4_lXe,G4_PbWO4,G4_Galactic,G4_GRAPHITE_POROUS,G4_LUCITE,G4_BRASS,G4_BRONZE,G4_STAINLESS_STEEL,G4_CR39,G4_OCTADECANOL]
FEATURE [App::DocumentObjectGroupPython] C_element128  label="C_element : 073"  # scripted group (container) (typed FeaturePython)
  n = 14
  ref = C_element
FEATURE [App::DocumentObjectGroupPython] H_element118  label="H_element : 065"  # scripted group (container) (typed FeaturePython)
  n = 10
  ref = H_element
FEATURE [App::DocumentObjectGroupPython] O_element111  label="O_element : 064"  # scripted group (container) (typed FeaturePython)
  n = 2
  ref = O_element
FEATURE [App::DocumentObjectGroupPython] N_element050  label="N_element : 023"  # scripted group (container) (typed FeaturePython)
  n = 2
  ref = N_element
FEATURE [App::DocumentObjectGroupPython] G4_KEVLAR  # scripted group (container) (typed FeaturePython)
  Dunit = g/cm3
  Dvalue = 1.44
  Group = -> [C_element128,H_element118,O_element111,N_element050]
  conduct = 2
  density = 1
  expand = 3
  formula = G4_KEVLAR
  name = G4_KEVLAR
  specific = 4
FEATURE [App::DocumentObjectGroupPython] C_element129  label="C_element : 074"  # scripted group (container) (typed FeaturePython)
  n = 10
  ref = C_element
FEATURE [App::DocumentObjectGroupPython] H_element119  label="H_element : 066"  # scripted group (container) (typed FeaturePython)
  n = 8
  ref = H_element
FEATURE [App::DocumentObjectGroupPython] O_element112  label="O_element : 065"  # scripted group (container) (typed FeaturePython)
  n = 4
  ref = O_element
FEATURE [App::DocumentObjectGroupPython] G4_DACRON  # scripted group (container) (typed FeaturePython)
  Dunit = g/cm3
  Dvalue = 1.4
  Group = -> [C_element129,H_element119,O_element112]
  conduct = 2
  density = 1
  expand = 3
  formula = G4_DACRON
  name = G4_DACRON
  specific = 4
FEATURE [App::DocumentObjectGroupPython] C_element130  label="C_element : 075"  # scripted group (container) (typed FeaturePython)
  n = 4
  ref = C_element
FEATURE [App::DocumentObjectGroupPython] H_element120  label="H_element : 067"  # scripted group (container) (typed FeaturePython)
  n = 5
  ref = H_element
FEATURE [App::DocumentObjectGroupPython] Cl_element030  label="Cl_element : 016"  # scripted group (container) (typed FeaturePython)
  n = 1
  ref = Cl_element
FEATURE [App::DocumentObjectGroupPython] G4_NEOPRENE  # scripted group (container) (typed FeaturePython)
  Dunit = g/cm3
  Dvalue = 1.23
  Group = -> [C_element130,H_element120,Cl_element030]
  conduct = 2
  density = 1
  expand = 3
  formula = G4_NEOPRENE
  name = G4_NEOPRENE
  specific = 4
FEATURE [App::DocumentObjectGroupPython] Space  # scripted group (container) (typed FeaturePython)
  Group = -> [G4_KEVLAR,G4_DACRON,G4_NEOPRENE]
FEATURE [App::DocumentObjectGroupPython] H_element121  label="H_element : 068"  # scripted group (container) (typed FeaturePython)
  n = 5
  ref = H_element
FEATURE [App::DocumentObjectGroupPython] C_element131  label="C_element : 076"  # scripted group (container) (typed FeaturePython)
  n = 4
  ref = C_element
FEATURE [App::DocumentObjectGroupPython] N_element051  label="N_element : 3"  # scripted group (container) (typed FeaturePython)
  n = 3
  ref = N_element
FEATURE [App::DocumentObjectGroupPython] O_element113  label="O_element : 066"  # scripted group (container) (typed FeaturePython)
  n = 1
  ref = O_element
FEATURE [App::DocumentObjectGroupPython] G4_CYTOSINE  # scripted group (container) (typed FeaturePython)
  Dunit = g/cm3
  Dvalue = 1.55
  Group = -> [H_element121,C_element131,N_element051,O_element113]
  conduct = 2
  density = 1
  expand = 3
  formula = G4_CYTOSINE
  name = G4_CYTOSINE
  specific = 4
FEATURE [App::DocumentObjectGroupPython] H_element122  label="H_element : 069"  # scripted group (container) (typed FeaturePython)
  n = 6
  ref = H_element
FEATURE [App::DocumentObjectGroupPython] C_element132  label="C_element : 077"  # scripted group (container) (typed FeaturePython)
  n = 5
  ref = C_element
FEATURE [App::DocumentObjectGroupPython] N_element052  label="N_element : 024"  # scripted group (container) (typed FeaturePython)
  n = 2
  ref = N_element
FEATURE [App::DocumentObjectGroupPython] O_element114  label="O_element : 067"  # scripted group (container) (typed FeaturePython)
  n = 2
  ref = O_element
FEATURE [App::DocumentObjectGroupPython] G4_THYMINE  # scripted group (container) (typed FeaturePython)
  Dunit = g/cm3
  Dvalue = 1.23
  Group = -> [H_element122,C_element132,N_element052,O_element114]
  conduct = 2
  density = 1
  expand = 3
  formula = G4_THYMINE
  name = G4_THYMINE
  specific = 4
FEATURE [App::DocumentObjectGroupPython] H_element123  label="H_element : 070"  # scripted group (container) (typed FeaturePython)
  n = 4
  ref = H_element
FEATURE [App::DocumentObjectGroupPython] C_element133  label="C_element : 078"  # scripted group (container) (typed FeaturePython)
  n = 4
  ref = C_element
FEATURE [App::DocumentObjectGroupPython] N_element053  label="N_element : 025"  # scripted group (container) (typed FeaturePython)
  n = 2
  ref = N_element
FEATURE [App::DocumentObjectGroupPython] O_element115  label="O_element : 068"  # scripted group (container) (typed FeaturePython)
  n = 2
  ref = O_element
FEATURE [App::DocumentObjectGroupPython] G4_URACIL  # scripted group (container) (typed FeaturePython)
  Dunit = g/cm3
  Dvalue = 1.32
  Group = -> [H_element123,C_element133,N_element053,O_element115]
  conduct = 2
  density = 1
  expand = 3
  formula = G4_URACIL
  name = G4_URACIL
  specific = 4
FEATURE [App::DocumentObjectGroupPython] H_element124  label="H_element : 071"  # scripted group (container) (typed FeaturePython)
  n = 4
  ref = H_element
FEATURE [App::DocumentObjectGroupPython] C_element134  label="C_element : 079"  # scripted group (container) (typed FeaturePython)
  n = 5
  ref = C_element
FEATURE [App::DocumentObjectGroupPython] N_element054  label="N_element : 026"  # scripted group (container) (typed FeaturePython)
  n = 5
  ref = N_element
FEATURE [App::DocumentObjectGroupPython] G4_DNA_ADENINE  # scripted group (container) (typed FeaturePython)
  Dunit = g/cm3
  Dvalue = 1
  Group = -> [H_element124,C_element134,N_element054]
  conduct = 2
  density = 1
  expand = 3
  formula = G4_DNA_ADENINE
  name = G4_DNA_ADENINE
  specific = 4
FEATURE [App::DocumentObjectGroupPython] H_element125  label="H_element : 072"  # scripted group (container) (typed FeaturePython)
  n = 4
  ref = H_element
FEATURE [App::DocumentObjectGroupPython] C_element135  label="C_element : 080"  # scripted group (container) (typed FeaturePython)
  n = 5
  ref = C_element
FEATURE [App::DocumentObjectGroupPython] N_element055  label="N_element : 027"  # scripted group (container) (typed FeaturePython)
  n = 5
  ref = N_element
FEATURE [App::DocumentObjectGroupPython] O_element116  label="O_element : 069"  # scripted group (container) (typed FeaturePython)
  n = 1
  ref = O_element
FEATURE [App::DocumentObjectGroupPython] G4_DNA_GUANINE  # scripted group (container) (typed FeaturePython)
  Dunit = g/cm3
  Dvalue = 1
  Group = -> [H_element125,C_element135,N_element055,O_element116]
  conduct = 2
  density = 1
  expand = 3
  formula = G4_DNA_GUANINE
  name = G4_DNA_GUANINE
  specific = 4
FEATURE [App::DocumentObjectGroupPython] H_element126  label="H_element : 073"  # scripted group (container) (typed FeaturePython)
  n = 4
  ref = H_element
FEATURE [App::DocumentObjectGroupPython] C_element136  label="C_element : 081"  # scripted group (container) (typed FeaturePython)
  n = 4
  ref = C_element
FEATURE [App::DocumentObjectGroupPython] N_element056  label="N_element : 028"  # scripted group (container) (typed FeaturePython)
  n = 3
  ref = N_element
FEATURE [App::DocumentObjectGroupPython] O_element117  label="O_element : 070"  # scripted group (container) (typed FeaturePython)
  n = 1
  ref = O_element
FEATURE [App::DocumentObjectGroupPython] G4_DNA_CYTOSINE  # scripted group (container) (typed FeaturePython)
  Dunit = g/cm3
  Dvalue = 1
  Group = -> [H_element126,C_element136,N_element056,O_element117]
  conduct = 2
  density = 1
  expand = 3
  formula = G4_DNA_CYTOSINE
  name = G4_DNA_CYTOSINE
  specific = 4
FEATURE [App::DocumentObjectGroupPython] H_element127  label="H_element : 074"  # scripted group (container) (typed FeaturePython)
  n = 5
  ref = H_element
FEATURE [App::DocumentObjectGroupPython] C_element137  label="C_element : 082"  # scripted group (container) (typed FeaturePython)
  n = 5
  ref = C_element
FEATURE [App::DocumentObjectGroupPython] N_element057  label="N_element : 029"  # scripted group (container) (typed FeaturePython)
  n = 2
  ref = N_element
FEATURE [App::DocumentObjectGroupPython] O_element118  label="O_element : 071"  # scripted group (container) (typed FeaturePython)
  n = 2
  ref = O_element
FEATURE [App::DocumentObjectGroupPython] G4_DNA_THYMINE  # scripted group (container) (typed FeaturePython)
  Dunit = g/cm3
  Dvalue = 1
  Group = -> [H_element127,C_element137,N_element057,O_element118]
  conduct = 2
  density = 1
  expand = 3
  formula = G4_DNA_THYMINE
  name = G4_DNA_THYMINE
  specific = 4
FEATURE [App::DocumentObjectGroupPython] H_element128  label="H_element : 075"  # scripted group (container) (typed FeaturePython)
  n = 3
  ref = H_element
FEATURE [App::DocumentObjectGroupPython] C_element138  label="C_element : 083"  # scripted group (container) (typed FeaturePython)
  n = 4
  ref = C_element
FEATURE [App::DocumentObjectGroupPython] N_element058  label="N_element : 030"  # scripted group (container) (typed FeaturePython)
  n = 2
  ref = N_element
FEATURE [App::DocumentObjectGroupPython] O_element119  label="O_element : 072"  # scripted group (container) (typed FeaturePython)
  n = 2
  ref = O_element
FEATURE [App::DocumentObjectGroupPython] G4_DNA_URACIL  # scripted group (container) (typed FeaturePython)
  Dunit = g/cm3
  Dvalue = 1
  Group = -> [H_element128,C_element138,N_element058,O_element119]
  conduct = 2
  density = 1
  expand = 3
  formula = G4_DNA_URACIL
  name = G4_DNA_URACIL
  specific = 4
FEATURE [App::DocumentObjectGroupPython] H_element129  label="H_element : 076"  # scripted group (container) (typed FeaturePython)
  n = 10
  ref = H_element
FEATURE [App::DocumentObjectGroupPython] C_element139  label="C_element : 084"  # scripted group (container) (typed FeaturePython)
  n = 10
  ref = C_element
FEATURE [App::DocumentObjectGroupPython] N_element059  label="N_element : 031"  # scripted group (container) (typed FeaturePython)
  n = 5
  ref = N_element
FEATURE [App::DocumentObjectGroupPython] O_element120  label="O_element : 073"  # scripted group (container) (typed FeaturePython)
  n = 4
  ref = O_element
FEATURE [App::DocumentObjectGroupPython] G4_DNA_ADENOSINE  # scripted group (container) (typed FeaturePython)
  Dunit = g/cm3
  Dvalue = 1
  Group = -> [H_element129,C_element139,N_element059,O_element120]
  conduct = 2
  density = 1
  expand = 3
  formula = G4_DNA_ADENOSINE
  name = G4_DNA_ADENOSINE
  specific = 4
FEATURE [App::DocumentObjectGroupPython] H_element130  label="H_element : 077"  # scripted group (container) (typed FeaturePython)
  n = 10
  ref = H_element
FEATURE [App::DocumentObjectGroupPython] C_element140  label="C_element : 085"  # scripted group (container) (typed FeaturePython)
  n = 10
  ref = C_element
FEATURE [App::DocumentObjectGroupPython] N_element060  label="N_element : 032"  # scripted group (container) (typed FeaturePython)
  n = 5
  ref = N_element
FEATURE [App::DocumentObjectGroupPython] O_element121  label="O_element : 074"  # scripted group (container) (typed FeaturePython)
  n = 5
  ref = O_element
FEATURE [App::DocumentObjectGroupPython] G4_DNA_GUANOSINE  # scripted group (container) (typed FeaturePython)
  Dunit = g/cm3
  Dvalue = 1
  Group = -> [H_element130,C_element140,N_element060,O_element121]
  conduct = 2
  density = 1
  expand = 3
  formula = G4_DNA_GUANOSINE
  name = G4_DNA_GUANOSINE
  specific = 4
FEATURE [App::DocumentObjectGroupPython] H_element131  label="H_element : 078"  # scripted group (container) (typed FeaturePython)
  n = 10
  ref = H_element
FEATURE [App::DocumentObjectGroupPython] C_element141  label="C_element : 086"  # scripted group (container) (typed FeaturePython)
  n = 9
  ref = C_element
FEATURE [App::DocumentObjectGroupPython] N_element061  label="N_element : 033"  # scripted group (container) (typed FeaturePython)
  n = 3
  ref = N_element
FEATURE [App::DocumentObjectGroupPython] O_element122  label="O_element : 075"  # scripted group (container) (typed FeaturePython)
  n = 5
  ref = O_element
FEATURE [App::DocumentObjectGroupPython] G4_DNA_CYTIDINE  # scripted group (container) (typed FeaturePython)
  Dunit = g/cm3
  Dvalue = 1
  Group = -> [H_element131,C_element141,N_element061,O_element122]
  conduct = 2
  density = 1
  expand = 3
  formula = G4_DNA_CYTIDINE
  name = G4_DNA_CYTIDINE
  specific = 4
FEATURE [App::DocumentObjectGroupPython] H_element132  label="H_element : 079"  # scripted group (container) (typed FeaturePython)
  n = 9
  ref = H_element
FEATURE [App::DocumentObjectGroupPython] C_element142  label="C_element : 087"  # scripted group (container) (typed FeaturePython)
  n = 9
  ref = C_element
FEATURE [App::DocumentObjectGroupPython] N_element062  label="N_element : 034"  # scripted group (container) (typed FeaturePython)
  n = 2
  ref = N_element
FEATURE [App::DocumentObjectGroupPython] O_element123  label="O_element : 076"  # scripted group (container) (typed FeaturePython)
  n = 6
  ref = O_element
FEATURE [App::DocumentObjectGroupPython] G4_DNA_URIDINE  # scripted group (container) (typed FeaturePython)
  Dunit = g/cm3
  Dvalue = 1
  Group = -> [H_element132,C_element142,N_element062,O_element123]
  conduct = 2
  density = 1
  expand = 3
  formula = G4_DNA_URIDINE
  name = G4_DNA_URIDINE
  specific = 4
FEATURE [App::DocumentObjectGroupPython] H_element133  label="H_element : 080"  # scripted group (container) (typed FeaturePython)
  n = 11
  ref = H_element
FEATURE [App::DocumentObjectGroupPython] C_element143  label="C_element : 088"  # scripted group (container) (typed FeaturePython)
  n = 10
  ref = C_element
FEATURE [App::DocumentObjectGroupPython] N_element063  label="N_element : 035"  # scripted group (container) (typed FeaturePython)
  n = 2
  ref = N_element
FEATURE [App::DocumentObjectGroupPython] O_element124  label="O_element : 077"  # scripted group (container) (typed FeaturePython)
  n = 6
  ref = O_element
FEATURE [App::DocumentObjectGroupPython] G4_DNA_METHYLURIDINE  # scripted group (container) (typed FeaturePython)
  Dunit = g/cm3
  Dvalue = 1
  Group = -> [H_element133,C_element143,N_element063,O_element124]
  conduct = 2
  density = 1
  expand = 3
  formula = G4_DNA_METHYLURIDINE
  name = G4_DNA_METHYLURIDINE
  specific = 4
FEATURE [App::DocumentObjectGroupPython] P_element014  label="P_element : 003"  # scripted group (container) (typed FeaturePython)
  n = 1
  ref = P_element
FEATURE [App::DocumentObjectGroupPython] O_element125  label="O_element : 078"  # scripted group (container) (typed FeaturePython)
  n = 3
  ref = O_element
FEATURE [App::DocumentObjectGroupPython] G4_DNA_MONOPHOSPHATE  # scripted group (container) (typed FeaturePython)
  Dunit = g/cm3
  Dvalue = 1
  Group = -> [P_element014,O_element125]
  conduct = 2
  density = 1
  expand = 3
  formula = G4_DNA_MONOPHOSPHATE
  name = G4_DNA_MONOPHOSPHATE
  specific = 4
FEATURE [App::DocumentObjectGroupPython] H_element134  label="H_element : 081"  # scripted group (container) (typed FeaturePython)
  n = 10
  ref = H_element
FEATURE [App::DocumentObjectGroupPython] C_element144  label="C_element : 089"  # scripted group (container) (typed FeaturePython)
  n = 10
  ref = C_element
FEATURE [App::DocumentObjectGroupPython] N_element064  label="N_element : 036"  # scripted group (container) (typed FeaturePython)
  n = 5
  ref = N_element
FEATURE [App::DocumentObjectGroupPython] O_element126  label="O_element : 079"  # scripted group (container) (typed FeaturePython)
  n = 7
  ref = O_element
FEATURE [App::DocumentObjectGroupPython] P_element015  label="P_element : 004"  # scripted group (container) (typed FeaturePython)
  n = 1
  ref = P_element
FEATURE [App::DocumentObjectGroupPython] G4_DNA_A  # scripted group (container) (typed FeaturePython)
  Dunit = g/cm3
  Dvalue = 1
  Group = -> [H_element134,C_element144,N_element064,O_element126,P_element015]
  conduct = 2
  density = 1
  expand = 3
  formula = G4_DNA_A
  name = G4_DNA_A
  specific = 4
FEATURE [App::DocumentObjectGroupPython] H_element135  label="H_element : 082"  # scripted group (container) (typed FeaturePython)
  n = 10
  ref = H_element
FEATURE [App::DocumentObjectGroupPython] C_element145  label="C_element : 090"  # scripted group (container) (typed FeaturePython)
  n = 10
  ref = C_element
FEATURE [App::DocumentObjectGroupPython] N_element065  label="N_element : 037"  # scripted group (container) (typed FeaturePython)
  n = 5
  ref = N_element
FEATURE [App::DocumentObjectGroupPython] O_element127  label="O_element : 8"  # scripted group (container) (typed FeaturePython)
  n = 8
  ref = O_element
FEATURE [App::DocumentObjectGroupPython] P_element016  label="P_element : 005"  # scripted group (container) (typed FeaturePython)
  n = 1
  ref = P_element
FEATURE [App::DocumentObjectGroupPython] G4_DNA_G  # scripted group (container) (typed FeaturePython)
  Dunit = g/cm3
  Dvalue = 1
  Group = -> [H_element135,C_element145,N_element065,O_element127,P_element016]
  conduct = 2
  density = 1
  expand = 3
  formula = G4_DNA_G
  name = G4_DNA_G
  specific = 4
FEATURE [App::DocumentObjectGroupPython] H_element136  label="H_element : 083"  # scripted group (container) (typed FeaturePython)
  n = 10
  ref = H_element
FEATURE [App::DocumentObjectGroupPython] C_element146  label="C_element : 091"  # scripted group (container) (typed FeaturePython)
  n = 9
  ref = C_element
FEATURE [App::DocumentObjectGroupPython] N_element066  label="N_element : 038"  # scripted group (container) (typed FeaturePython)
  n = 3
  ref = N_element
FEATURE [App::DocumentObjectGroupPython] O_element128  label="O_element : 080"  # scripted group (container) (typed FeaturePython)
  n = 8
  ref = O_element
FEATURE [App::DocumentObjectGroupPython] P_element017  label="P_element : 006"  # scripted group (container) (typed FeaturePython)
  n = 1
  ref = P_element
FEATURE [App::DocumentObjectGroupPython] G4_DNA_C  # scripted group (container) (typed FeaturePython)
  Dunit = g/cm3
  Dvalue = 1
  Group = -> [H_element136,C_element146,N_element066,O_element128,P_element017]
  conduct = 2
  density = 1
  expand = 3
  formula = G4_DNA_C
  name = G4_DNA_C
  specific = 4
FEATURE [App::DocumentObjectGroupPython] H_element137  label="H_element : 084"  # scripted group (container) (typed FeaturePython)
  n = 9
  ref = H_element
FEATURE [App::DocumentObjectGroupPython] C_element147  label="C_element : 092"  # scripted group (container) (typed FeaturePython)
  n = 9
  ref = C_element
FEATURE [App::DocumentObjectGroupPython] N_element067  label="N_element : 039"  # scripted group (container) (typed FeaturePython)
  n = 2
  ref = N_element
FEATURE [App::DocumentObjectGroupPython] O_element129  label="O_element : 9"  # scripted group (container) (typed FeaturePython)
  n = 9
  ref = O_element
FEATURE [App::DocumentObjectGroupPython] P_element018  label="P_element : 007"  # scripted group (container) (typed FeaturePython)
  n = 1
  ref = P_element
FEATURE [App::DocumentObjectGroupPython] G4_DNA_U  # scripted group (container) (typed FeaturePython)
  Dunit = g/cm3
  Dvalue = 1
  Group = -> [H_element137,C_element147,N_element067,O_element129,P_element018]
  conduct = 2
  density = 1
  expand = 3
  formula = G4_DNA_U
  name = G4_DNA_U
  specific = 4
FEATURE [App::DocumentObjectGroupPython] H_element138  label="H_element : 085"  # scripted group (container) (typed FeaturePython)
  n = 11
  ref = H_element
FEATURE [App::DocumentObjectGroupPython] C_element148  label="C_element : 093"  # scripted group (container) (typed FeaturePython)
  n = 10
  ref = C_element
FEATURE [App::DocumentObjectGroupPython] N_element068  label="N_element : 040"  # scripted group (container) (typed FeaturePython)
  n = 2
  ref = N_element
FEATURE [App::DocumentObjectGroupPython] O_element130  label="O_element : 081"  # scripted group (container) (typed FeaturePython)
  n = 9
  ref = O_element
FEATURE [App::DocumentObjectGroupPython] P_element019  label="P_element : 008"  # scripted group (container) (typed FeaturePython)
  n = 1
  ref = P_element
FEATURE [App::DocumentObjectGroupPython] G4_DNA_MU  # scripted group (container) (typed FeaturePython)
  Dunit = g/cm3
  Dvalue = 1
  Group = -> [H_element138,C_element148,N_element068,O_element130,P_element019]
  conduct = 2
  density = 1
  expand = 3
  formula = G4_DNA_MU
  name = G4_DNA_MU
  specific = 4
FEATURE [App::DocumentObjectGroupPython] BioChemical  # scripted group (container) (typed FeaturePython)
  Group = -> [G4_CYTOSINE,G4_THYMINE,G4_URACIL,G4_DNA_ADENINE,G4_DNA_GUANINE,G4_DNA_CYTOSINE,G4_DNA_THYMINE,G4_DNA_URACIL,G4_DNA_ADENOSINE,G4_DNA_GUANOSINE,G4_DNA_CYTIDINE,G4_DNA_URIDINE,G4_DNA_METHYLURIDINE,G4_DNA_MONOPHOSPHATE,G4_DNA_A,G4_DNA_G,G4_DNA_C,G4_DNA_U,G4_DNA_MU]
FEATURE [App::DocumentObjectGroupPython] G4Materials  # scripted group (container) (typed FeaturePython)
  Group = -> [NIST,Element,HEP,Space,BioChemical]
  version = 1
FEATURE [App::DocumentObjectGroupPython] Geant4  # scripted group (container) (typed FeaturePython)
  Group = -> [G4Isotopes,G4Elements,G4Materials]
FEATURE [App::DocumentObjectGroupPython] Materials  # scripted group (container) (typed FeaturePython)
  Group = -> [Geant4]
FEATURE [Part::FeaturePython] GDMLBox_WorldBox  # WARN: FeaturePython — macro-defined, semantics opaque (R4)
  lunit = 2
  material = 5
  x = 200
  y = 200
  z = 200
FEATURE [Sketcher::SketchObject] Sketch
  ArcFitTolerance = 0
  FullyConstrained = false
  MakeInternals = false
  sketch-geometry (5):
    g0: ArcOfParabola CenterX=25.5233 CenterY=-14.8036 CenterZ=0 NormalX=0 NormalY=0 NormalZ=1 Focal=15.7547 AngleXU=-2.61216 StartAngle=-26.5589 EndAngle=30.7535
    g1: GeomPoint [constr] X=11.9255 Y=-22.7604 Z=0
    g2: LineSegment [constr] StartX=25.5233 StartY=-14.8036 StartZ=0 EndX=11.9255 EndY=-22.7604 EndZ=0
    g3: LineSegment StartX=2.44918 StartY=2.46618 StartZ=0 EndX=19.9697 EndY=-18.0533 EndZ=0
    g4: LineSegment StartX=19.9697 StartY=-18.0533 StartZ=0 EndX=28.1021 EndY=-48.9263 EndZ=0
  constraints (6):
    c: InternalAlignment(g1,g0)
    c: InternalAlignment(g2,g0)
    c: Coincident(g3,g0)
    c: PointOnObject(g3,g2)
    c: Coincident(g3,g4)
    c: Coincident(g4,g0)
FEATURE [Part::Extrusion] Extrude
  Base = -> Sketch
  Dir = (0,0,1)
  DirMode = 2
  FaceMakerClass = Part::FaceMakerBullseye
  FaceMakerMode = 3
  LengthFwd = 10
  LengthRev = 0
  Solid = true
  Symmetric = false
FEATURE [App::Part] Part
  Group = -> [Sketch,Extrude]
  Origin = -> Origin001
  material = 5
FEATURE [App::Part] worldVOL
  Group = -> [GDMLBox_WorldBox,Part]
  Origin = -> Origin
